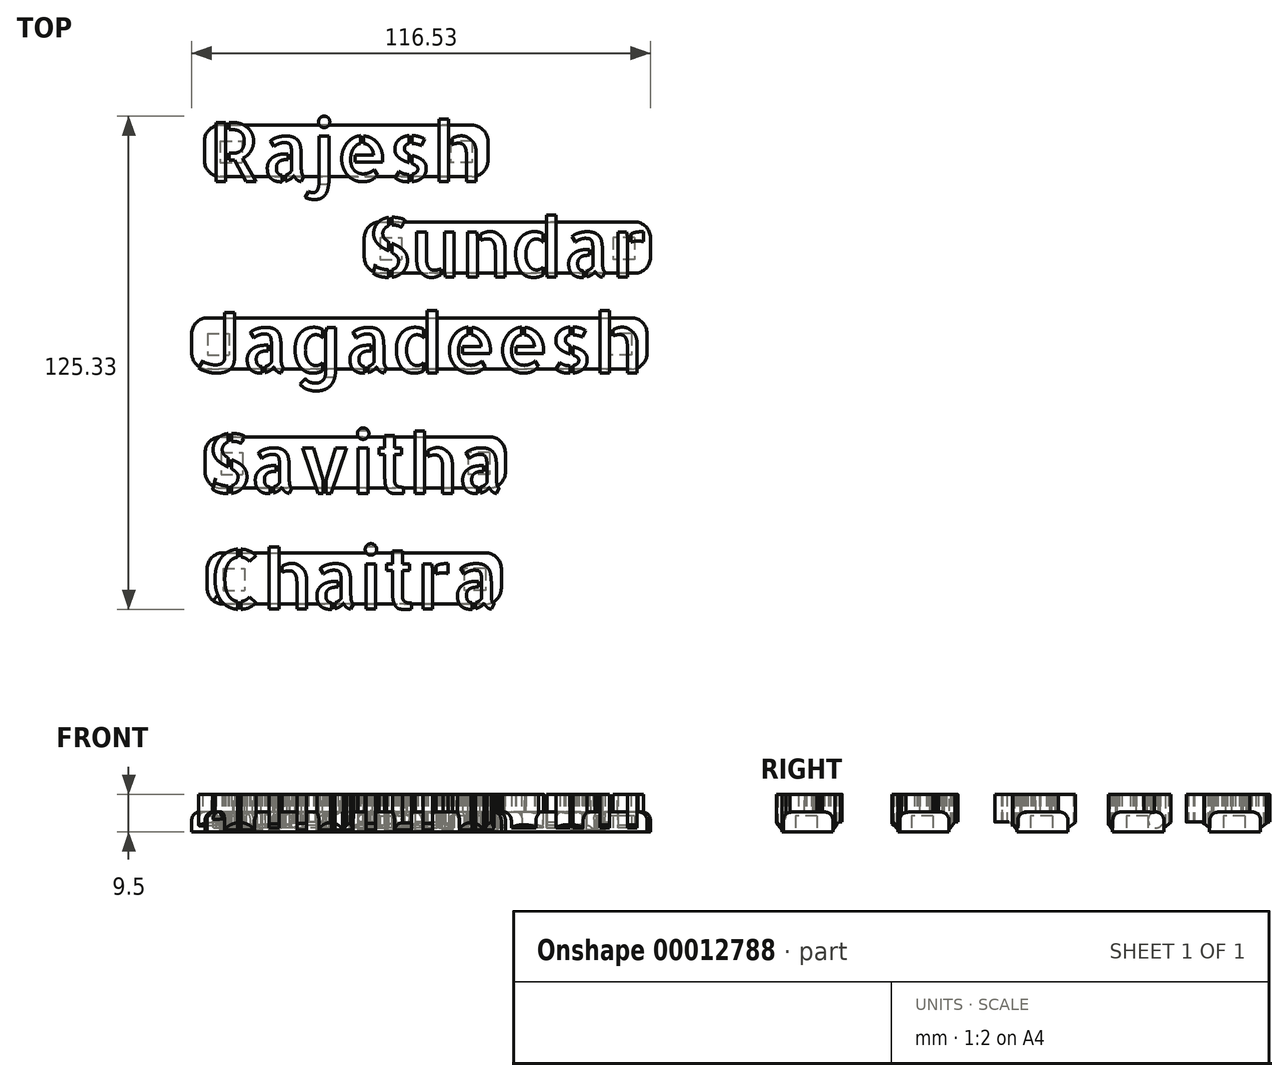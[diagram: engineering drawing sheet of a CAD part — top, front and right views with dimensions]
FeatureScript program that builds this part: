
annotation { "Feature Type Name" : "Feature", "Feature Type Description" : "" }
export const myFeature = defineFeature(function(context is Context, id is Id, definition is map)
    precondition{}
    {
        {
            var Q0;
            Q0=qCreatedBy(makeId("Top.planeOp"),FACE);
            var sketch = newSketch(context, id + "F0", { "sketchPlane" : qUnion([Q0])});
            skText(sketch, "E0", { "text": "Rajesh", "fontName": "AllertaStencil-Regular.ttf"});
            skText(sketch, "E1", { "text": "Sundar", "fontName": "AllertaStencil-Regular.ttf"});
            skText(sketch, "E2", { "text": "Jagadeesh", "fontName": "AllertaStencil-Regular.ttf"});
            skText(sketch, "E3", { "text": "Savitha", "fontName": "AllertaStencil-Regular.ttf"});
            skText(sketch, "E4", { "text": "Chaitra", "fontName": "AllertaStencil-Regular.ttf"});
            const initialGuessF0  = {"E0": [-0.06447, 0.04937, 1, 0, 0.015], "E1": [-0.02434, 0.02506, 1, 0, 0.015], "E2": [-0.06765, 0.00075, 1, 0, 0.015], "E3": [-0.06512, -0.02985, 1, 0, 0.015], "E4": [-0.0645, -0.05926, 1, 0, 0.015]};
            skSetInitialGuess(sketch, initialGuessF0);
            skSolve(sketch);
        }
        {
            var Q0;
            Q0 = qSketchRegion(id + "F0", true);
            extrude(context, id + "F1", {"entities" : qUnion([Q0]), "depth" : 7 * mm});
        }
        {
            var Q0;
            Q0=qCreatedBy(makeId("Top.planeOp"),FACE);
            var sketch = newSketch(context, id + "F2", { "sketchPlane" : qUnion([Q0])});
            skLineSegment(sketch, "E5.bottom", {"start": v(-65.56, 63.64) * mm, "end": v(6.44, 63.64) * mm});
            skLineSegment(sketch, "E5.top", {"start": v(-65.56, 50.64) * mm, "end": v(6.44, 50.64) * mm});
            skLineSegment(sketch, "E5.left", {"start": v(-65.56, 63.64) * mm, "end": v(-65.56, 50.64) * mm});
            skLineSegment(sketch, "E5.right", {"start": v(6.44, 63.64) * mm, "end": v(6.44, 50.64) * mm});
            skLineSegment(sketch, "E6.bottom", {"start": v(-24.95, 39.07) * mm, "end": v(47.73, 39.07) * mm});
            skLineSegment(sketch, "E6.top", {"start": v(-24.95, 26.07) * mm, "end": v(47.73, 26.07) * mm});
            skLineSegment(sketch, "E6.left", {"start": v(-24.95, 39.07) * mm, "end": v(-24.95, 26.07) * mm});
            skLineSegment(sketch, "E6.right", {"start": v(47.73, 39.07) * mm, "end": v(47.73, 26.07) * mm});
            skLineSegment(sketch, "E7.bottom", {"start": v(-68.8, 14.71) * mm, "end": v(46.87, 14.71) * mm});
            skLineSegment(sketch, "E7.top", {"start": v(-68.8, 1.71) * mm, "end": v(46.87, 1.71) * mm});
            skLineSegment(sketch, "E7.left", {"start": v(-68.8, 14.71) * mm, "end": v(-68.8, 1.71) * mm});
            skLineSegment(sketch, "E7.right", {"start": v(46.87, 14.71) * mm, "end": v(46.87, 1.71) * mm});
            skLineSegment(sketch, "E8.bottom", {"start": v(-65.39, -15.52) * mm, "end": v(10.87, -15.52) * mm});
            skLineSegment(sketch, "E8.top", {"start": v(-65.39, -28.52) * mm, "end": v(10.87, -28.52) * mm});
            skLineSegment(sketch, "E8.left", {"start": v(-65.39, -15.52) * mm, "end": v(-65.39, -28.52) * mm});
            skLineSegment(sketch, "E8.right", {"start": v(10.87, -15.52) * mm, "end": v(10.87, -28.52) * mm});
            skLineSegment(sketch, "E9.bottom", {"start": v(-64.88, -45) * mm, "end": v(9.85, -45) * mm});
            skLineSegment(sketch, "E9.top", {"start": v(-64.88, -58) * mm, "end": v(9.85, -58) * mm});
            skLineSegment(sketch, "E9.left", {"start": v(-64.88, -45) * mm, "end": v(-64.88, -58) * mm});
            skLineSegment(sketch, "E9.right", {"start": v(9.85, -45) * mm, "end": v(9.85, -58) * mm});
            skSolve(sketch);
        }
        {
            var Q0;
            Q0=qCreatedBy(makeId("Top.planeOp"),FACE);
            cPlane(context, id + "F3", {"entities" : qUnion([Q0]), "cplaneType" : CPlaneType.OFFSET, "offset" : 2.5 * mm, "width" : 150 * mm, "height" : 150 * mm});
        }
        {
            var Q0;
            Q0=qCreatedBy(id+"F3.planeOp",FACE);
            var sketch = newSketch(context, id + "F4", { "sketchPlane" : qUnion([Q0])});
            skLineSegment(sketch, "E10.0.0", {"start": v(6.44, 63.64) * mm, "end": v(-65.56, 63.64) * mm});
            skLineSegment(sketch, "E10.0.1", {"start": v(-65.56, 63.64) * mm, "end": v(-65.56, 50.64) * mm});
            skLineSegment(sketch, "E10.0.2", {"start": v(-65.56, 50.64) * mm, "end": v(6.44, 50.64) * mm});
            skLineSegment(sketch, "E10.0.3", {"start": v(6.44, 50.64) * mm, "end": v(6.44, 63.64) * mm});
            skLineSegment(sketch, "E11.0.0", {"start": v(47.73, 39.07) * mm, "end": v(-24.95, 39.07) * mm});
            skLineSegment(sketch, "E11.0.1", {"start": v(-24.95, 39.07) * mm, "end": v(-24.95, 26.07) * mm});
            skLineSegment(sketch, "E11.0.2", {"start": v(-24.95, 26.07) * mm, "end": v(47.73, 26.07) * mm});
            skLineSegment(sketch, "E11.0.3", {"start": v(47.73, 26.07) * mm, "end": v(47.73, 39.07) * mm});
            skLineSegment(sketch, "E12.0.0", {"start": v(46.87, 14.71) * mm, "end": v(-68.8, 14.71) * mm});
            skLineSegment(sketch, "E12.0.1", {"start": v(-68.8, 14.71) * mm, "end": v(-68.8, 1.71) * mm});
            skLineSegment(sketch, "E12.0.2", {"start": v(-68.8, 1.71) * mm, "end": v(46.87, 1.71) * mm});
            skLineSegment(sketch, "E12.0.3", {"start": v(46.87, 1.71) * mm, "end": v(46.87, 14.71) * mm});
            skLineSegment(sketch, "E13.0.0", {"start": v(10.87, -15.52) * mm, "end": v(-65.39, -15.52) * mm});
            skLineSegment(sketch, "E13.0.1", {"start": v(-65.39, -15.52) * mm, "end": v(-65.39, -28.52) * mm});
            skLineSegment(sketch, "E13.0.2", {"start": v(-65.39, -28.52) * mm, "end": v(10.87, -28.52) * mm});
            skLineSegment(sketch, "E13.0.3", {"start": v(10.87, -28.52) * mm, "end": v(10.87, -15.52) * mm});
            skLineSegment(sketch, "E14.0.0", {"start": v(9.85, -45) * mm, "end": v(-64.88, -45) * mm});
            skLineSegment(sketch, "E14.0.1", {"start": v(-64.88, -45) * mm, "end": v(-64.88, -58) * mm});
            skLineSegment(sketch, "E14.0.2", {"start": v(-64.88, -58) * mm, "end": v(9.85, -58) * mm});
            skLineSegment(sketch, "E14.0.3", {"start": v(9.85, -58) * mm, "end": v(9.85, -45) * mm});
            skSolve(sketch);
        }
        {
            var Q0;
            Q0 = qSketchRegion(id + "F4", true);
            extrude(context, id + "F5", {"entities" : qUnion([Q0]), "oppositeDirection" : true, "depth" : 5 * mm});
        }
        {
            var Q0;
            Q0=makeQuery(id+"F5.opExtrude","SWEPT_EDGE",EDGE,{"disambiguationData":[OSD([sQuery(id+"F4.wireOp",EDGE,"E10.0.0"),sQuery(id+"F4.wireOp",EDGE,"E10.0.3")])]});
            var Q1;
            Q1=makeQuery(id+"F5.opExtrude","SWEPT_EDGE",EDGE,{"disambiguationData":[OSD([sQuery(id+"F4.wireOp",EDGE,"E10.0.2"),sQuery(id+"F4.wireOp",EDGE,"E10.0.3")])]});
            var Q2;
            Q2=makeQuery(id+"F5.opExtrude","SWEPT_EDGE",EDGE,{"disambiguationData":[OSD([sQuery(id+"F4.wireOp",EDGE,"E11.0.0"),sQuery(id+"F4.wireOp",EDGE,"E11.0.3")])]});
            var Q3;
            Q3=makeQuery(id+"F5.opExtrude","SWEPT_EDGE",EDGE,{"disambiguationData":[OSD([sQuery(id+"F4.wireOp",EDGE,"E12.0.0"),sQuery(id+"F4.wireOp",EDGE,"E12.0.3")])]});
            var Q4;
            Q4=makeQuery(id+"F5.opExtrude","SWEPT_EDGE",EDGE,{"disambiguationData":[OSD([sQuery(id+"F4.wireOp",EDGE,"E12.0.2"),sQuery(id+"F4.wireOp",EDGE,"E12.0.3")])]});
            var Q5;
            Q5=makeQuery(id+"F5.opExtrude","SWEPT_EDGE",EDGE,{"disambiguationData":[OSD([sQuery(id+"F4.wireOp",EDGE,"E13.0.0"),sQuery(id+"F4.wireOp",EDGE,"E13.0.3")])]});
            var Q6;
            Q6=makeQuery(id+"F5.opExtrude","SWEPT_EDGE",EDGE,{"disambiguationData":[OSD([sQuery(id+"F4.wireOp",EDGE,"E13.0.2"),sQuery(id+"F4.wireOp",EDGE,"E13.0.3")])]});
            var Q7;
            Q7=makeQuery(id+"F5.opExtrude","SWEPT_EDGE",EDGE,{"disambiguationData":[OSD([sQuery(id+"F4.wireOp",EDGE,"E14.0.0"),sQuery(id+"F4.wireOp",EDGE,"E14.0.3")])]});
            var Q8;
            Q8=makeQuery(id+"F5.opExtrude","SWEPT_EDGE",EDGE,{"disambiguationData":[OSD([sQuery(id+"F4.wireOp",EDGE,"E14.0.2"),sQuery(id+"F4.wireOp",EDGE,"E14.0.3")])]});
            var Q9;
            Q9=makeQuery(id+"F5.opExtrude","SWEPT_EDGE",EDGE,{"disambiguationData":[OSD([sQuery(id+"F4.wireOp",EDGE,"E14.0.1"),sQuery(id+"F4.wireOp",EDGE,"E14.0.2")])]});
            var Q10;
            Q10=makeQuery(id+"F5.opExtrude","SWEPT_EDGE",EDGE,{"disambiguationData":[OSD([sQuery(id+"F4.wireOp",EDGE,"E13.0.1"),sQuery(id+"F4.wireOp",EDGE,"E13.0.2")])]});
            var Q11;
            Q11=makeQuery(id+"F5.opExtrude","SWEPT_EDGE",EDGE,{"disambiguationData":[OSD([sQuery(id+"F4.wireOp",EDGE,"E13.0.0"),sQuery(id+"F4.wireOp",EDGE,"E13.0.1")])]});
            var Q12;
            Q12=makeQuery(id+"F5.opExtrude","SWEPT_EDGE",EDGE,{"disambiguationData":[OSD([sQuery(id+"F4.wireOp",EDGE,"E14.0.0"),sQuery(id+"F4.wireOp",EDGE,"E14.0.1")])]});
            var Q13;
            Q13=makeQuery(id+"F5.opExtrude","SWEPT_EDGE",EDGE,{"disambiguationData":[OSD([sQuery(id+"F4.wireOp",EDGE,"E12.0.1"),sQuery(id+"F4.wireOp",EDGE,"E12.0.2")])]});
            var Q14;
            Q14=makeQuery(id+"F5.opExtrude","SWEPT_EDGE",EDGE,{"disambiguationData":[OSD([sQuery(id+"F4.wireOp",EDGE,"E12.0.0"),sQuery(id+"F4.wireOp",EDGE,"E12.0.1")])]});
            var Q15;
            Q15=makeQuery(id+"F5.opExtrude","SWEPT_EDGE",EDGE,{"disambiguationData":[OSD([sQuery(id+"F4.wireOp",EDGE,"E10.0.1"),sQuery(id+"F4.wireOp",EDGE,"E10.0.2")])]});
            var Q16;
            Q16=makeQuery(id+"F5.opExtrude","SWEPT_EDGE",EDGE,{"disambiguationData":[OSD([sQuery(id+"F4.wireOp",EDGE,"E10.0.0"),sQuery(id+"F4.wireOp",EDGE,"E10.0.1")])]});
            var Q17;
            Q17=makeQuery(id+"F5.opExtrude","SWEPT_EDGE",EDGE,{"disambiguationData":[OSD([sQuery(id+"F4.wireOp",EDGE,"E11.0.1"),sQuery(id+"F4.wireOp",EDGE,"E11.0.2")])]});
            var Q18;
            Q18=makeQuery(id+"F5.opExtrude","SWEPT_EDGE",EDGE,{"disambiguationData":[OSD([sQuery(id+"F4.wireOp",EDGE,"E11.0.0"),sQuery(id+"F4.wireOp",EDGE,"E11.0.1")])]});
            var Q19;
            Q19=makeQuery(id+"F5.opExtrude","SWEPT_EDGE",EDGE,{"disambiguationData":[OSD([sQuery(id+"F4.wireOp",EDGE,"E11.0.2"),sQuery(id+"F4.wireOp",EDGE,"E11.0.3")])]});
            fillet(context, id + "F6", {"entities" : qUnion([Q0, Q1, Q2, Q3, Q4, Q5, Q6, Q7, Q8, Q9, Q10, Q11, Q12, Q13, Q14, Q15, Q16, Q17, Q18, Q19]), "radius" : 4 * mm, "tangentPropagation" : true, "allowEdgeOverflow" : false});
        }
        {
            var Q0;
            Q0=makeQuery(id+"F5.opExtrude","SWEPT_BODY",BODY,{"disambiguationData":[OSD([sQuery(id+"F4.wireOp",EDGE,"E10.0.0"),sQuery(id+"F4.wireOp",EDGE,"E10.0.1"),sQuery(id+"F4.wireOp",EDGE,"E10.0.2"),sQuery(id+"F4.wireOp",EDGE,"E10.0.3")])]});
            var Q1;
            Q1=makeQuery(id+"F1.opExtrude","SWEPT_BODY",BODY,{"disambiguationData":[OSD([sQuery(id+"F0.wireOp",EDGE,"E0.sketch_text.stroke-0"),sQuery(id+"F0.wireOp",EDGE,"E0.sketch_text.stroke-1"),sQuery(id+"F0.wireOp",EDGE,"E0.sketch_text.stroke-2"),sQuery(id+"F0.wireOp",EDGE,"E0.sketch_text.stroke-3")])]});
            var Q2;
            Q2=makeQuery(id+"F1.opExtrude","SWEPT_BODY",BODY,{"disambiguationData":[OSD([sQuery(id+"F0.wireOp",EDGE,"E0.sketch_text.stroke-4"),sQuery(id+"F0.wireOp",EDGE,"E0.sketch_text.stroke-5"),sQuery(id+"F0.wireOp",EDGE,"E0.sketch_text.stroke-6"),sQuery(id+"F0.wireOp",EDGE,"E0.sketch_text.stroke-7"),sQuery(id+"F0.wireOp",EDGE,"E0.sketch_text.stroke-8"),sQuery(id+"F0.wireOp",EDGE,"E0.sketch_text.stroke-9"),sQuery(id+"F0.wireOp",EDGE,"E0.sketch_text.stroke-10"),sQuery(id+"F0.wireOp",EDGE,"E0.sketch_text.stroke-11"),sQuery(id+"F0.wireOp",EDGE,"E0.sketch_text.stroke-12"),sQuery(id+"F0.wireOp",EDGE,"E0.sketch_text.stroke-13"),sQuery(id+"F0.wireOp",EDGE,"E0.sketch_text.stroke-14"),sQuery(id+"F0.wireOp",EDGE,"E0.sketch_text.stroke-15"),sQuery(id+"F0.wireOp",EDGE,"E0.sketch_text.stroke-16"),sQuery(id+"F0.wireOp",EDGE,"E0.sketch_text.stroke-17"),sQuery(id+"F0.wireOp",EDGE,"E0.sketch_text.stroke-18"),sQuery(id+"F0.wireOp",EDGE,"E0.sketch_text.stroke-19"),sQuery(id+"F0.wireOp",EDGE,"E0.sketch_text.stroke-20"),sQuery(id+"F0.wireOp",EDGE,"E0.sketch_text.stroke-21"),sQuery(id+"F0.wireOp",EDGE,"E0.sketch_text.stroke-22"),sQuery(id+"F0.wireOp",EDGE,"E0.sketch_text.stroke-23"),sQuery(id+"F0.wireOp",EDGE,"E0.sketch_text.stroke-24"),sQuery(id+"F0.wireOp",EDGE,"E0.sketch_text.stroke-25"),sQuery(id+"F0.wireOp",EDGE,"E0.sketch_text.stroke-26"),sQuery(id+"F0.wireOp",EDGE,"E0.sketch_text.stroke-27"),sQuery(id+"F0.wireOp",EDGE,"E0.sketch_text.stroke-28"),sQuery(id+"F0.wireOp",EDGE,"E0.sketch_text.stroke-29")])]});
            var Q3;
            Q3=makeQuery(id+"F1.opExtrude","SWEPT_BODY",BODY,{"disambiguationData":[OSD([sQuery(id+"F0.wireOp",EDGE,"E0.sketch_text.stroke-124"),sQuery(id+"F0.wireOp",EDGE,"E0.sketch_text.stroke-125"),sQuery(id+"F0.wireOp",EDGE,"E0.sketch_text.stroke-126"),sQuery(id+"F0.wireOp",EDGE,"E0.sketch_text.stroke-127"),sQuery(id+"F0.wireOp",EDGE,"E0.sketch_text.stroke-128"),sQuery(id+"F0.wireOp",EDGE,"E0.sketch_text.stroke-129"),sQuery(id+"F0.wireOp",EDGE,"E0.sketch_text.stroke-130"),sQuery(id+"F0.wireOp",EDGE,"E0.sketch_text.stroke-131"),sQuery(id+"F0.wireOp",EDGE,"E0.sketch_text.stroke-132"),sQuery(id+"F0.wireOp",EDGE,"E0.sketch_text.stroke-133"),sQuery(id+"F0.wireOp",EDGE,"E0.sketch_text.stroke-134"),sQuery(id+"F0.wireOp",EDGE,"E0.sketch_text.stroke-135"),sQuery(id+"F0.wireOp",EDGE,"E0.sketch_text.stroke-136"),sQuery(id+"F0.wireOp",EDGE,"E0.sketch_text.stroke-137"),sQuery(id+"F0.wireOp",EDGE,"E0.sketch_text.stroke-138"),sQuery(id+"F0.wireOp",EDGE,"E0.sketch_text.stroke-139"),sQuery(id+"F0.wireOp",EDGE,"E0.sketch_text.stroke-140"),sQuery(id+"F0.wireOp",EDGE,"E0.sketch_text.stroke-141"),sQuery(id+"F0.wireOp",EDGE,"E0.sketch_text.stroke-142"),sQuery(id+"F0.wireOp",EDGE,"E0.sketch_text.stroke-143"),sQuery(id+"F0.wireOp",EDGE,"E0.sketch_text.stroke-144"),sQuery(id+"F0.wireOp",EDGE,"E0.sketch_text.stroke-145"),sQuery(id+"F0.wireOp",EDGE,"E0.sketch_text.stroke-146"),sQuery(id+"F0.wireOp",EDGE,"E0.sketch_text.stroke-147")])]});
            var Q4;
            Q4=makeQuery(id+"F1.opExtrude","SWEPT_BODY",BODY,{"disambiguationData":[OSD([sQuery(id+"F0.wireOp",EDGE,"E0.sketch_text.stroke-148"),sQuery(id+"F0.wireOp",EDGE,"E0.sketch_text.stroke-149"),sQuery(id+"F0.wireOp",EDGE,"E0.sketch_text.stroke-150"),sQuery(id+"F0.wireOp",EDGE,"E0.sketch_text.stroke-151"),sQuery(id+"F0.wireOp",EDGE,"E0.sketch_text.stroke-152"),sQuery(id+"F0.wireOp",EDGE,"E0.sketch_text.stroke-153"),sQuery(id+"F0.wireOp",EDGE,"E0.sketch_text.stroke-154"),sQuery(id+"F0.wireOp",EDGE,"E0.sketch_text.stroke-155"),sQuery(id+"F0.wireOp",EDGE,"E0.sketch_text.stroke-156"),sQuery(id+"F0.wireOp",EDGE,"E0.sketch_text.stroke-157"),sQuery(id+"F0.wireOp",EDGE,"E0.sketch_text.stroke-158"),sQuery(id+"F0.wireOp",EDGE,"E0.sketch_text.stroke-159"),sQuery(id+"F0.wireOp",EDGE,"E0.sketch_text.stroke-160"),sQuery(id+"F0.wireOp",EDGE,"E0.sketch_text.stroke-161")])]});
            var Q5;
            Q5=makeQuery(id+"F1.opExtrude","SWEPT_BODY",BODY,{"disambiguationData":[OSD([sQuery(id+"F0.wireOp",EDGE,"E0.sketch_text.stroke-111"),sQuery(id+"F0.wireOp",EDGE,"E0.sketch_text.stroke-112"),sQuery(id+"F0.wireOp",EDGE,"E0.sketch_text.stroke-113"),sQuery(id+"F0.wireOp",EDGE,"E0.sketch_text.stroke-114"),sQuery(id+"F0.wireOp",EDGE,"E0.sketch_text.stroke-115"),sQuery(id+"F0.wireOp",EDGE,"E0.sketch_text.stroke-116"),sQuery(id+"F0.wireOp",EDGE,"E0.sketch_text.stroke-117"),sQuery(id+"F0.wireOp",EDGE,"E0.sketch_text.stroke-118"),sQuery(id+"F0.wireOp",EDGE,"E0.sketch_text.stroke-119"),sQuery(id+"F0.wireOp",EDGE,"E0.sketch_text.stroke-120"),sQuery(id+"F0.wireOp",EDGE,"E0.sketch_text.stroke-121"),sQuery(id+"F0.wireOp",EDGE,"E0.sketch_text.stroke-122"),sQuery(id+"F0.wireOp",EDGE,"E0.sketch_text.stroke-123")])]});
            var Q6;
            Q6=makeQuery(id+"F1.opExtrude","SWEPT_BODY",BODY,{"disambiguationData":[OSD([sQuery(id+"F0.wireOp",EDGE,"E0.sketch_text.stroke-191"),sQuery(id+"F0.wireOp",EDGE,"E0.sketch_text.stroke-192"),sQuery(id+"F0.wireOp",EDGE,"E0.sketch_text.stroke-193"),sQuery(id+"F0.wireOp",EDGE,"E0.sketch_text.stroke-194")])]});
            var Q7;
            Q7=makeQuery(id+"F1.opExtrude","SWEPT_BODY",BODY,{"disambiguationData":[OSD([sQuery(id+"F0.wireOp",EDGE,"E0.sketch_text.stroke-30"),sQuery(id+"F0.wireOp",EDGE,"E0.sketch_text.stroke-31"),sQuery(id+"F0.wireOp",EDGE,"E0.sketch_text.stroke-32"),sQuery(id+"F0.wireOp",EDGE,"E0.sketch_text.stroke-33"),sQuery(id+"F0.wireOp",EDGE,"E0.sketch_text.stroke-34"),sQuery(id+"F0.wireOp",EDGE,"E0.sketch_text.stroke-35"),sQuery(id+"F0.wireOp",EDGE,"E0.sketch_text.stroke-36"),sQuery(id+"F0.wireOp",EDGE,"E0.sketch_text.stroke-37"),sQuery(id+"F0.wireOp",EDGE,"E0.sketch_text.stroke-38"),sQuery(id+"F0.wireOp",EDGE,"E0.sketch_text.stroke-39"),sQuery(id+"F0.wireOp",EDGE,"E0.sketch_text.stroke-40"),sQuery(id+"F0.wireOp",EDGE,"E0.sketch_text.stroke-41"),sQuery(id+"F0.wireOp",EDGE,"E0.sketch_text.stroke-42"),sQuery(id+"F0.wireOp",EDGE,"E0.sketch_text.stroke-43"),sQuery(id+"F0.wireOp",EDGE,"E0.sketch_text.stroke-44"),sQuery(id+"F0.wireOp",EDGE,"E0.sketch_text.stroke-45"),sQuery(id+"F0.wireOp",EDGE,"E0.sketch_text.stroke-46"),sQuery(id+"F0.wireOp",EDGE,"E0.sketch_text.stroke-47"),sQuery(id+"F0.wireOp",EDGE,"E0.sketch_text.stroke-48")])]});
            var Q8;
            Q8=makeQuery(id+"F1.opExtrude","SWEPT_BODY",BODY,{"disambiguationData":[OSD([sQuery(id+"F0.wireOp",EDGE,"E0.sketch_text.stroke-49"),sQuery(id+"F0.wireOp",EDGE,"E0.sketch_text.stroke-50"),sQuery(id+"F0.wireOp",EDGE,"E0.sketch_text.stroke-51"),sQuery(id+"F0.wireOp",EDGE,"E0.sketch_text.stroke-52"),sQuery(id+"F0.wireOp",EDGE,"E0.sketch_text.stroke-53"),sQuery(id+"F0.wireOp",EDGE,"E0.sketch_text.stroke-54"),sQuery(id+"F0.wireOp",EDGE,"E0.sketch_text.stroke-55"),sQuery(id+"F0.wireOp",EDGE,"E0.sketch_text.stroke-56"),sQuery(id+"F0.wireOp",EDGE,"E0.sketch_text.stroke-57"),sQuery(id+"F0.wireOp",EDGE,"E0.sketch_text.stroke-58"),sQuery(id+"F0.wireOp",EDGE,"E0.sketch_text.stroke-59"),sQuery(id+"F0.wireOp",EDGE,"E0.sketch_text.stroke-60"),sQuery(id+"F0.wireOp",EDGE,"E0.sketch_text.stroke-61"),sQuery(id+"F0.wireOp",EDGE,"E0.sketch_text.stroke-62"),sQuery(id+"F0.wireOp",EDGE,"E0.sketch_text.stroke-63"),sQuery(id+"F0.wireOp",EDGE,"E0.sketch_text.stroke-64"),sQuery(id+"F0.wireOp",EDGE,"E0.sketch_text.stroke-65"),sQuery(id+"F0.wireOp",EDGE,"E0.sketch_text.stroke-66"),sQuery(id+"F0.wireOp",EDGE,"E0.sketch_text.stroke-67"),sQuery(id+"F0.wireOp",EDGE,"E0.sketch_text.stroke-68"),sQuery(id+"F0.wireOp",EDGE,"E0.sketch_text.stroke-69"),sQuery(id+"F0.wireOp",EDGE,"E0.sketch_text.stroke-70"),sQuery(id+"F0.wireOp",EDGE,"E0.sketch_text.stroke-71"),sQuery(id+"F0.wireOp",EDGE,"E0.sketch_text.stroke-72"),sQuery(id+"F0.wireOp",EDGE,"E0.sketch_text.stroke-73"),sQuery(id+"F0.wireOp",EDGE,"E0.sketch_text.stroke-74"),sQuery(id+"F0.wireOp",EDGE,"E0.sketch_text.stroke-75"),sQuery(id+"F0.wireOp",EDGE,"E0.sketch_text.stroke-76"),sQuery(id+"F0.wireOp",EDGE,"E0.sketch_text.stroke-77"),sQuery(id+"F0.wireOp",EDGE,"E0.sketch_text.stroke-78"),sQuery(id+"F0.wireOp",EDGE,"E0.sketch_text.stroke-79"),sQuery(id+"F0.wireOp",EDGE,"E0.sketch_text.stroke-80"),sQuery(id+"F0.wireOp",EDGE,"E0.sketch_text.stroke-81"),sQuery(id+"F0.wireOp",EDGE,"E0.sketch_text.stroke-82"),sQuery(id+"F0.wireOp",EDGE,"E0.sketch_text.stroke-83"),sQuery(id+"F0.wireOp",EDGE,"E0.sketch_text.stroke-84")])]});
            var Q9;
            Q9=makeQuery(id+"F1.opExtrude","SWEPT_BODY",BODY,{"disambiguationData":[OSD([sQuery(id+"F0.wireOp",EDGE,"E0.sketch_text.stroke-162"),sQuery(id+"F0.wireOp",EDGE,"E0.sketch_text.stroke-163"),sQuery(id+"F0.wireOp",EDGE,"E0.sketch_text.stroke-164"),sQuery(id+"F0.wireOp",EDGE,"E0.sketch_text.stroke-165"),sQuery(id+"F0.wireOp",EDGE,"E0.sketch_text.stroke-166"),sQuery(id+"F0.wireOp",EDGE,"E0.sketch_text.stroke-167")])]});
            var Q10;
            Q10=makeQuery(id+"F1.opExtrude","SWEPT_BODY",BODY,{"disambiguationData":[OSD([sQuery(id+"F0.wireOp",EDGE,"E0.sketch_text.stroke-177"),sQuery(id+"F0.wireOp",EDGE,"E0.sketch_text.stroke-178"),sQuery(id+"F0.wireOp",EDGE,"E0.sketch_text.stroke-179"),sQuery(id+"F0.wireOp",EDGE,"E0.sketch_text.stroke-180"),sQuery(id+"F0.wireOp",EDGE,"E0.sketch_text.stroke-181"),sQuery(id+"F0.wireOp",EDGE,"E0.sketch_text.stroke-182"),sQuery(id+"F0.wireOp",EDGE,"E0.sketch_text.stroke-183"),sQuery(id+"F0.wireOp",EDGE,"E0.sketch_text.stroke-184"),sQuery(id+"F0.wireOp",EDGE,"E0.sketch_text.stroke-185"),sQuery(id+"F0.wireOp",EDGE,"E0.sketch_text.stroke-186"),sQuery(id+"F0.wireOp",EDGE,"E0.sketch_text.stroke-187"),sQuery(id+"F0.wireOp",EDGE,"E0.sketch_text.stroke-188"),sQuery(id+"F0.wireOp",EDGE,"E0.sketch_text.stroke-189"),sQuery(id+"F0.wireOp",EDGE,"E0.sketch_text.stroke-190")])]});
            var Q11;
            Q11=makeQuery(id+"F1.opExtrude","SWEPT_BODY",BODY,{"disambiguationData":[OSD([sQuery(id+"F0.wireOp",EDGE,"E0.sketch_text.stroke-85"),sQuery(id+"F0.wireOp",EDGE,"E0.sketch_text.stroke-86"),sQuery(id+"F0.wireOp",EDGE,"E0.sketch_text.stroke-87"),sQuery(id+"F0.wireOp",EDGE,"E0.sketch_text.stroke-88"),sQuery(id+"F0.wireOp",EDGE,"E0.sketch_text.stroke-89"),sQuery(id+"F0.wireOp",EDGE,"E0.sketch_text.stroke-90"),sQuery(id+"F0.wireOp",EDGE,"E0.sketch_text.stroke-91"),sQuery(id+"F0.wireOp",EDGE,"E0.sketch_text.stroke-92"),sQuery(id+"F0.wireOp",EDGE,"E0.sketch_text.stroke-93"),sQuery(id+"F0.wireOp",EDGE,"E0.sketch_text.stroke-94"),sQuery(id+"F0.wireOp",EDGE,"E0.sketch_text.stroke-95"),sQuery(id+"F0.wireOp",EDGE,"E0.sketch_text.stroke-96"),sQuery(id+"F0.wireOp",EDGE,"E0.sketch_text.stroke-97"),sQuery(id+"F0.wireOp",EDGE,"E0.sketch_text.stroke-98"),sQuery(id+"F0.wireOp",EDGE,"E0.sketch_text.stroke-99"),sQuery(id+"F0.wireOp",EDGE,"E0.sketch_text.stroke-100"),sQuery(id+"F0.wireOp",EDGE,"E0.sketch_text.stroke-101"),sQuery(id+"F0.wireOp",EDGE,"E0.sketch_text.stroke-102")])]});
            var Q12;
            Q12=makeQuery(id+"F1.opExtrude","SWEPT_BODY",BODY,{"disambiguationData":[OSD([sQuery(id+"F0.wireOp",EDGE,"E0.sketch_text.stroke-195"),sQuery(id+"F0.wireOp",EDGE,"E0.sketch_text.stroke-196"),sQuery(id+"F0.wireOp",EDGE,"E0.sketch_text.stroke-197"),sQuery(id+"F0.wireOp",EDGE,"E0.sketch_text.stroke-198"),sQuery(id+"F0.wireOp",EDGE,"E0.sketch_text.stroke-199"),sQuery(id+"F0.wireOp",EDGE,"E0.sketch_text.stroke-200"),sQuery(id+"F0.wireOp",EDGE,"E0.sketch_text.stroke-201"),sQuery(id+"F0.wireOp",EDGE,"E0.sketch_text.stroke-202"),sQuery(id+"F0.wireOp",EDGE,"E0.sketch_text.stroke-203"),sQuery(id+"F0.wireOp",EDGE,"E0.sketch_text.stroke-204"),sQuery(id+"F0.wireOp",EDGE,"E0.sketch_text.stroke-205"),sQuery(id+"F0.wireOp",EDGE,"E0.sketch_text.stroke-206"),sQuery(id+"F0.wireOp",EDGE,"E0.sketch_text.stroke-207"),sQuery(id+"F0.wireOp",EDGE,"E0.sketch_text.stroke-208"),sQuery(id+"F0.wireOp",EDGE,"E0.sketch_text.stroke-209"),sQuery(id+"F0.wireOp",EDGE,"E0.sketch_text.stroke-210"),sQuery(id+"F0.wireOp",EDGE,"E0.sketch_text.stroke-211"),sQuery(id+"F0.wireOp",EDGE,"E0.sketch_text.stroke-212"),sQuery(id+"F0.wireOp",EDGE,"E0.sketch_text.stroke-213")])]});
            var Q13;
            Q13=makeQuery(id+"F1.opExtrude","SWEPT_BODY",BODY,{"disambiguationData":[OSD([sQuery(id+"F0.wireOp",EDGE,"E0.sketch_text.stroke-168"),sQuery(id+"F0.wireOp",EDGE,"E0.sketch_text.stroke-169"),sQuery(id+"F0.wireOp",EDGE,"E0.sketch_text.stroke-170"),sQuery(id+"F0.wireOp",EDGE,"E0.sketch_text.stroke-171"),sQuery(id+"F0.wireOp",EDGE,"E0.sketch_text.stroke-172"),sQuery(id+"F0.wireOp",EDGE,"E0.sketch_text.stroke-173"),sQuery(id+"F0.wireOp",EDGE,"E0.sketch_text.stroke-174"),sQuery(id+"F0.wireOp",EDGE,"E0.sketch_text.stroke-175"),sQuery(id+"F0.wireOp",EDGE,"E0.sketch_text.stroke-176")])]});
            var Q14;
            Q14=makeQuery(id+"F1.opExtrude","SWEPT_BODY",BODY,{"disambiguationData":[OSD([sQuery(id+"F0.wireOp",EDGE,"E0.sketch_text.stroke-103"),sQuery(id+"F0.wireOp",EDGE,"E0.sketch_text.stroke-104"),sQuery(id+"F0.wireOp",EDGE,"E0.sketch_text.stroke-105"),sQuery(id+"F0.wireOp",EDGE,"E0.sketch_text.stroke-106"),sQuery(id+"F0.wireOp",EDGE,"E0.sketch_text.stroke-107"),sQuery(id+"F0.wireOp",EDGE,"E0.sketch_text.stroke-108"),sQuery(id+"F0.wireOp",EDGE,"E0.sketch_text.stroke-109"),sQuery(id+"F0.wireOp",EDGE,"E0.sketch_text.stroke-110")])]});
            booleanBodies(context, id + "F7", {"operationType" : BooleanOperationType.UNION, "tools" : qUnion([Q0, Q1, Q2, Q3, Q4, Q5, Q6, Q7, Q8, Q9, Q10, Q11, Q12, Q13, Q14])});
        }
        {
            var Q0;
            Q0=makeQuery(id+"F1.opExtrude","SWEPT_BODY",BODY,{"disambiguationData":[OSD([sQuery(id+"F0.wireOp",EDGE,"E1.sketch_text.stroke-129"),sQuery(id+"F0.wireOp",EDGE,"E1.sketch_text.stroke-130"),sQuery(id+"F0.wireOp",EDGE,"E1.sketch_text.stroke-131"),sQuery(id+"F0.wireOp",EDGE,"E1.sketch_text.stroke-132"),sQuery(id+"F0.wireOp",EDGE,"E1.sketch_text.stroke-133"),sQuery(id+"F0.wireOp",EDGE,"E1.sketch_text.stroke-134"),sQuery(id+"F0.wireOp",EDGE,"E1.sketch_text.stroke-135"),sQuery(id+"F0.wireOp",EDGE,"E1.sketch_text.stroke-136"),sQuery(id+"F0.wireOp",EDGE,"E1.sketch_text.stroke-137"),sQuery(id+"F0.wireOp",EDGE,"E1.sketch_text.stroke-138"),sQuery(id+"F0.wireOp",EDGE,"E1.sketch_text.stroke-139"),sQuery(id+"F0.wireOp",EDGE,"E1.sketch_text.stroke-140"),sQuery(id+"F0.wireOp",EDGE,"E1.sketch_text.stroke-141"),sQuery(id+"F0.wireOp",EDGE,"E1.sketch_text.stroke-142"),sQuery(id+"F0.wireOp",EDGE,"E1.sketch_text.stroke-143"),sQuery(id+"F0.wireOp",EDGE,"E1.sketch_text.stroke-144"),sQuery(id+"F0.wireOp",EDGE,"E1.sketch_text.stroke-145"),sQuery(id+"F0.wireOp",EDGE,"E1.sketch_text.stroke-146"),sQuery(id+"F0.wireOp",EDGE,"E1.sketch_text.stroke-147")])]});
            var Q1;
            Q1=makeQuery(id+"F1.opExtrude","SWEPT_BODY",BODY,{"disambiguationData":[OSD([sQuery(id+"F0.wireOp",EDGE,"E1.sketch_text.stroke-148"),sQuery(id+"F0.wireOp",EDGE,"E1.sketch_text.stroke-149"),sQuery(id+"F0.wireOp",EDGE,"E1.sketch_text.stroke-150"),sQuery(id+"F0.wireOp",EDGE,"E1.sketch_text.stroke-151"),sQuery(id+"F0.wireOp",EDGE,"E1.sketch_text.stroke-152"),sQuery(id+"F0.wireOp",EDGE,"E1.sketch_text.stroke-153"),sQuery(id+"F0.wireOp",EDGE,"E1.sketch_text.stroke-154"),sQuery(id+"F0.wireOp",EDGE,"E1.sketch_text.stroke-155"),sQuery(id+"F0.wireOp",EDGE,"E1.sketch_text.stroke-156"),sQuery(id+"F0.wireOp",EDGE,"E1.sketch_text.stroke-157"),sQuery(id+"F0.wireOp",EDGE,"E1.sketch_text.stroke-158"),sQuery(id+"F0.wireOp",EDGE,"E1.sketch_text.stroke-159"),sQuery(id+"F0.wireOp",EDGE,"E1.sketch_text.stroke-160"),sQuery(id+"F0.wireOp",EDGE,"E1.sketch_text.stroke-161"),sQuery(id+"F0.wireOp",EDGE,"E1.sketch_text.stroke-162"),sQuery(id+"F0.wireOp",EDGE,"E1.sketch_text.stroke-163"),sQuery(id+"F0.wireOp",EDGE,"E1.sketch_text.stroke-164"),sQuery(id+"F0.wireOp",EDGE,"E1.sketch_text.stroke-165"),sQuery(id+"F0.wireOp",EDGE,"E1.sketch_text.stroke-166"),sQuery(id+"F0.wireOp",EDGE,"E1.sketch_text.stroke-167"),sQuery(id+"F0.wireOp",EDGE,"E1.sketch_text.stroke-168"),sQuery(id+"F0.wireOp",EDGE,"E1.sketch_text.stroke-169"),sQuery(id+"F0.wireOp",EDGE,"E1.sketch_text.stroke-170"),sQuery(id+"F0.wireOp",EDGE,"E1.sketch_text.stroke-171"),sQuery(id+"F0.wireOp",EDGE,"E1.sketch_text.stroke-172"),sQuery(id+"F0.wireOp",EDGE,"E1.sketch_text.stroke-173"),sQuery(id+"F0.wireOp",EDGE,"E1.sketch_text.stroke-174"),sQuery(id+"F0.wireOp",EDGE,"E1.sketch_text.stroke-175"),sQuery(id+"F0.wireOp",EDGE,"E1.sketch_text.stroke-176"),sQuery(id+"F0.wireOp",EDGE,"E1.sketch_text.stroke-177"),sQuery(id+"F0.wireOp",EDGE,"E1.sketch_text.stroke-178"),sQuery(id+"F0.wireOp",EDGE,"E1.sketch_text.stroke-179"),sQuery(id+"F0.wireOp",EDGE,"E1.sketch_text.stroke-180"),sQuery(id+"F0.wireOp",EDGE,"E1.sketch_text.stroke-181"),sQuery(id+"F0.wireOp",EDGE,"E1.sketch_text.stroke-182"),sQuery(id+"F0.wireOp",EDGE,"E1.sketch_text.stroke-183")])]});
            var Q2;
            Q2=makeQuery(id+"F1.opExtrude","SWEPT_BODY",BODY,{"disambiguationData":[OSD([sQuery(id+"F0.wireOp",EDGE,"E1.sketch_text.stroke-191"),sQuery(id+"F0.wireOp",EDGE,"E1.sketch_text.stroke-192"),sQuery(id+"F0.wireOp",EDGE,"E1.sketch_text.stroke-193"),sQuery(id+"F0.wireOp",EDGE,"E1.sketch_text.stroke-194"),sQuery(id+"F0.wireOp",EDGE,"E1.sketch_text.stroke-195"),sQuery(id+"F0.wireOp",EDGE,"E1.sketch_text.stroke-196"),sQuery(id+"F0.wireOp",EDGE,"E1.sketch_text.stroke-197")])]});
            var Q3;
            Q3=makeQuery(id+"F5.opExtrude","SWEPT_BODY",BODY,{"disambiguationData":[OSD([sQuery(id+"F4.wireOp",EDGE,"E11.0.0"),sQuery(id+"F4.wireOp",EDGE,"E11.0.1"),sQuery(id+"F4.wireOp",EDGE,"E11.0.2"),sQuery(id+"F4.wireOp",EDGE,"E11.0.3")])]});
            var Q4;
            Q4=makeQuery(id+"F1.opExtrude","SWEPT_BODY",BODY,{"disambiguationData":[OSD([sQuery(id+"F0.wireOp",EDGE,"E1.sketch_text.stroke-37"),sQuery(id+"F0.wireOp",EDGE,"E1.sketch_text.stroke-38"),sQuery(id+"F0.wireOp",EDGE,"E1.sketch_text.stroke-39"),sQuery(id+"F0.wireOp",EDGE,"E1.sketch_text.stroke-40"),sQuery(id+"F0.wireOp",EDGE,"E1.sketch_text.stroke-41"),sQuery(id+"F0.wireOp",EDGE,"E1.sketch_text.stroke-42"),sQuery(id+"F0.wireOp",EDGE,"E1.sketch_text.stroke-43"),sQuery(id+"F0.wireOp",EDGE,"E1.sketch_text.stroke-44"),sQuery(id+"F0.wireOp",EDGE,"E1.sketch_text.stroke-45"),sQuery(id+"F0.wireOp",EDGE,"E1.sketch_text.stroke-46"),sQuery(id+"F0.wireOp",EDGE,"E1.sketch_text.stroke-47"),sQuery(id+"F0.wireOp",EDGE,"E1.sketch_text.stroke-48"),sQuery(id+"F0.wireOp",EDGE,"E1.sketch_text.stroke-49")])]});
            var Q5;
            Q5=makeQuery(id+"F1.opExtrude","SWEPT_BODY",BODY,{"disambiguationData":[OSD([sQuery(id+"F0.wireOp",EDGE,"E1.sketch_text.stroke-50"),sQuery(id+"F0.wireOp",EDGE,"E1.sketch_text.stroke-51"),sQuery(id+"F0.wireOp",EDGE,"E1.sketch_text.stroke-52"),sQuery(id+"F0.wireOp",EDGE,"E1.sketch_text.stroke-53"),sQuery(id+"F0.wireOp",EDGE,"E1.sketch_text.stroke-54"),sQuery(id+"F0.wireOp",EDGE,"E1.sketch_text.stroke-55"),sQuery(id+"F0.wireOp",EDGE,"E1.sketch_text.stroke-56"),sQuery(id+"F0.wireOp",EDGE,"E1.sketch_text.stroke-57"),sQuery(id+"F0.wireOp",EDGE,"E1.sketch_text.stroke-58"),sQuery(id+"F0.wireOp",EDGE,"E1.sketch_text.stroke-59"),sQuery(id+"F0.wireOp",EDGE,"E1.sketch_text.stroke-60"),sQuery(id+"F0.wireOp",EDGE,"E1.sketch_text.stroke-61"),sQuery(id+"F0.wireOp",EDGE,"E1.sketch_text.stroke-62"),sQuery(id+"F0.wireOp",EDGE,"E1.sketch_text.stroke-63"),sQuery(id+"F0.wireOp",EDGE,"E1.sketch_text.stroke-64"),sQuery(id+"F0.wireOp",EDGE,"E1.sketch_text.stroke-65"),sQuery(id+"F0.wireOp",EDGE,"E1.sketch_text.stroke-66"),sQuery(id+"F0.wireOp",EDGE,"E1.sketch_text.stroke-67"),sQuery(id+"F0.wireOp",EDGE,"E1.sketch_text.stroke-68"),sQuery(id+"F0.wireOp",EDGE,"E1.sketch_text.stroke-69")])]});
            var Q6;
            Q6=makeQuery(id+"F1.opExtrude","SWEPT_BODY",BODY,{"disambiguationData":[OSD([sQuery(id+"F0.wireOp",EDGE,"E1.sketch_text.stroke-75"),sQuery(id+"F0.wireOp",EDGE,"E1.sketch_text.stroke-76"),sQuery(id+"F0.wireOp",EDGE,"E1.sketch_text.stroke-77"),sQuery(id+"F0.wireOp",EDGE,"E1.sketch_text.stroke-78"),sQuery(id+"F0.wireOp",EDGE,"E1.sketch_text.stroke-79")])]});
            var Q7;
            Q7=makeQuery(id+"F1.opExtrude","SWEPT_BODY",BODY,{"disambiguationData":[OSD([sQuery(id+"F0.wireOp",EDGE,"E1.sketch_text.stroke-11"),sQuery(id+"F0.wireOp",EDGE,"E1.sketch_text.stroke-12"),sQuery(id+"F0.wireOp",EDGE,"E1.sketch_text.stroke-13"),sQuery(id+"F0.wireOp",EDGE,"E1.sketch_text.stroke-14"),sQuery(id+"F0.wireOp",EDGE,"E1.sketch_text.stroke-15"),sQuery(id+"F0.wireOp",EDGE,"E1.sketch_text.stroke-16"),sQuery(id+"F0.wireOp",EDGE,"E1.sketch_text.stroke-17"),sQuery(id+"F0.wireOp",EDGE,"E1.sketch_text.stroke-18"),sQuery(id+"F0.wireOp",EDGE,"E1.sketch_text.stroke-19"),sQuery(id+"F0.wireOp",EDGE,"E1.sketch_text.stroke-20"),sQuery(id+"F0.wireOp",EDGE,"E1.sketch_text.stroke-21"),sQuery(id+"F0.wireOp",EDGE,"E1.sketch_text.stroke-22"),sQuery(id+"F0.wireOp",EDGE,"E1.sketch_text.stroke-23"),sQuery(id+"F0.wireOp",EDGE,"E1.sketch_text.stroke-24")])]});
            var Q8;
            Q8=makeQuery(id+"F1.opExtrude","SWEPT_BODY",BODY,{"disambiguationData":[OSD([sQuery(id+"F0.wireOp",EDGE,"E1.sketch_text.stroke-70"),sQuery(id+"F0.wireOp",EDGE,"E1.sketch_text.stroke-71"),sQuery(id+"F0.wireOp",EDGE,"E1.sketch_text.stroke-72"),sQuery(id+"F0.wireOp",EDGE,"E1.sketch_text.stroke-73"),sQuery(id+"F0.wireOp",EDGE,"E1.sketch_text.stroke-74")])]});
            var Q9;
            Q9=makeQuery(id+"F1.opExtrude","SWEPT_BODY",BODY,{"disambiguationData":[OSD([sQuery(id+"F0.wireOp",EDGE,"E1.sketch_text.stroke-80"),sQuery(id+"F0.wireOp",EDGE,"E1.sketch_text.stroke-81"),sQuery(id+"F0.wireOp",EDGE,"E1.sketch_text.stroke-82"),sQuery(id+"F0.wireOp",EDGE,"E1.sketch_text.stroke-83"),sQuery(id+"F0.wireOp",EDGE,"E1.sketch_text.stroke-84"),sQuery(id+"F0.wireOp",EDGE,"E1.sketch_text.stroke-85"),sQuery(id+"F0.wireOp",EDGE,"E1.sketch_text.stroke-86"),sQuery(id+"F0.wireOp",EDGE,"E1.sketch_text.stroke-87"),sQuery(id+"F0.wireOp",EDGE,"E1.sketch_text.stroke-88"),sQuery(id+"F0.wireOp",EDGE,"E1.sketch_text.stroke-89"),sQuery(id+"F0.wireOp",EDGE,"E1.sketch_text.stroke-90"),sQuery(id+"F0.wireOp",EDGE,"E1.sketch_text.stroke-91"),sQuery(id+"F0.wireOp",EDGE,"E1.sketch_text.stroke-92"),sQuery(id+"F0.wireOp",EDGE,"E1.sketch_text.stroke-93"),sQuery(id+"F0.wireOp",EDGE,"E1.sketch_text.stroke-94"),sQuery(id+"F0.wireOp",EDGE,"E1.sketch_text.stroke-95"),sQuery(id+"F0.wireOp",EDGE,"E1.sketch_text.stroke-96"),sQuery(id+"F0.wireOp",EDGE,"E1.sketch_text.stroke-97"),sQuery(id+"F0.wireOp",EDGE,"E1.sketch_text.stroke-98")])]});
            var Q10;
            Q10=makeQuery(id+"F1.opExtrude","SWEPT_BODY",BODY,{"disambiguationData":[OSD([sQuery(id+"F0.wireOp",EDGE,"E1.sketch_text.stroke-104"),sQuery(id+"F0.wireOp",EDGE,"E1.sketch_text.stroke-105"),sQuery(id+"F0.wireOp",EDGE,"E1.sketch_text.stroke-106"),sQuery(id+"F0.wireOp",EDGE,"E1.sketch_text.stroke-107"),sQuery(id+"F0.wireOp",EDGE,"E1.sketch_text.stroke-108"),sQuery(id+"F0.wireOp",EDGE,"E1.sketch_text.stroke-109"),sQuery(id+"F0.wireOp",EDGE,"E1.sketch_text.stroke-110"),sQuery(id+"F0.wireOp",EDGE,"E1.sketch_text.stroke-111"),sQuery(id+"F0.wireOp",EDGE,"E1.sketch_text.stroke-112"),sQuery(id+"F0.wireOp",EDGE,"E1.sketch_text.stroke-113"),sQuery(id+"F0.wireOp",EDGE,"E1.sketch_text.stroke-114"),sQuery(id+"F0.wireOp",EDGE,"E1.sketch_text.stroke-115"),sQuery(id+"F0.wireOp",EDGE,"E1.sketch_text.stroke-116"),sQuery(id+"F0.wireOp",EDGE,"E1.sketch_text.stroke-117"),sQuery(id+"F0.wireOp",EDGE,"E1.sketch_text.stroke-118"),sQuery(id+"F0.wireOp",EDGE,"E1.sketch_text.stroke-119"),sQuery(id+"F0.wireOp",EDGE,"E1.sketch_text.stroke-120"),sQuery(id+"F0.wireOp",EDGE,"E1.sketch_text.stroke-121"),sQuery(id+"F0.wireOp",EDGE,"E1.sketch_text.stroke-122"),sQuery(id+"F0.wireOp",EDGE,"E1.sketch_text.stroke-123"),sQuery(id+"F0.wireOp",EDGE,"E1.sketch_text.stroke-124"),sQuery(id+"F0.wireOp",EDGE,"E1.sketch_text.stroke-125"),sQuery(id+"F0.wireOp",EDGE,"E1.sketch_text.stroke-126"),sQuery(id+"F0.wireOp",EDGE,"E1.sketch_text.stroke-127"),sQuery(id+"F0.wireOp",EDGE,"E1.sketch_text.stroke-128")])]});
            var Q11;
            Q11=makeQuery(id+"F1.opExtrude","SWEPT_BODY",BODY,{"disambiguationData":[OSD([sQuery(id+"F0.wireOp",EDGE,"E1.sketch_text.stroke-99"),sQuery(id+"F0.wireOp",EDGE,"E1.sketch_text.stroke-100"),sQuery(id+"F0.wireOp",EDGE,"E1.sketch_text.stroke-101"),sQuery(id+"F0.wireOp",EDGE,"E1.sketch_text.stroke-102"),sQuery(id+"F0.wireOp",EDGE,"E1.sketch_text.stroke-103")])]});
            var Q12;
            Q12=makeQuery(id+"F1.opExtrude","SWEPT_BODY",BODY,{"disambiguationData":[OSD([sQuery(id+"F0.wireOp",EDGE,"E1.sketch_text.stroke-184"),sQuery(id+"F0.wireOp",EDGE,"E1.sketch_text.stroke-185"),sQuery(id+"F0.wireOp",EDGE,"E1.sketch_text.stroke-186"),sQuery(id+"F0.wireOp",EDGE,"E1.sketch_text.stroke-187"),sQuery(id+"F0.wireOp",EDGE,"E1.sketch_text.stroke-188"),sQuery(id+"F0.wireOp",EDGE,"E1.sketch_text.stroke-189"),sQuery(id+"F0.wireOp",EDGE,"E1.sketch_text.stroke-190")])]});
            var Q13;
            Q13=makeQuery(id+"F1.opExtrude","SWEPT_BODY",BODY,{"disambiguationData":[OSD([sQuery(id+"F0.wireOp",EDGE,"E1.sketch_text.stroke-25"),sQuery(id+"F0.wireOp",EDGE,"E1.sketch_text.stroke-26"),sQuery(id+"F0.wireOp",EDGE,"E1.sketch_text.stroke-27"),sQuery(id+"F0.wireOp",EDGE,"E1.sketch_text.stroke-28"),sQuery(id+"F0.wireOp",EDGE,"E1.sketch_text.stroke-29"),sQuery(id+"F0.wireOp",EDGE,"E1.sketch_text.stroke-30"),sQuery(id+"F0.wireOp",EDGE,"E1.sketch_text.stroke-31"),sQuery(id+"F0.wireOp",EDGE,"E1.sketch_text.stroke-32"),sQuery(id+"F0.wireOp",EDGE,"E1.sketch_text.stroke-33"),sQuery(id+"F0.wireOp",EDGE,"E1.sketch_text.stroke-34"),sQuery(id+"F0.wireOp",EDGE,"E1.sketch_text.stroke-35"),sQuery(id+"F0.wireOp",EDGE,"E1.sketch_text.stroke-36")])]});
            var Q14;
            Q14=makeQuery(id+"F1.opExtrude","SWEPT_BODY",BODY,{"disambiguationData":[OSD([sQuery(id+"F0.wireOp",EDGE,"E1.sketch_text.stroke-0"),sQuery(id+"F0.wireOp",EDGE,"E1.sketch_text.stroke-1"),sQuery(id+"F0.wireOp",EDGE,"E1.sketch_text.stroke-2"),sQuery(id+"F0.wireOp",EDGE,"E1.sketch_text.stroke-3"),sQuery(id+"F0.wireOp",EDGE,"E1.sketch_text.stroke-4"),sQuery(id+"F0.wireOp",EDGE,"E1.sketch_text.stroke-5"),sQuery(id+"F0.wireOp",EDGE,"E1.sketch_text.stroke-6"),sQuery(id+"F0.wireOp",EDGE,"E1.sketch_text.stroke-7"),sQuery(id+"F0.wireOp",EDGE,"E1.sketch_text.stroke-8"),sQuery(id+"F0.wireOp",EDGE,"E1.sketch_text.stroke-9"),sQuery(id+"F0.wireOp",EDGE,"E1.sketch_text.stroke-10")])]});
            booleanBodies(context, id + "F8", {"operationType" : BooleanOperationType.UNION, "tools" : qUnion([Q0, Q1, Q2, Q3, Q4, Q5, Q6, Q7, Q8, Q9, Q10, Q11, Q12, Q13, Q14])});
        }
        {
            var Q0;
            Q0=makeQuery(id+"F1.opExtrude","SWEPT_BODY",BODY,{"disambiguationData":[OSD([sQuery(id+"F0.wireOp",EDGE,"E2.sketch_text.stroke-0"),sQuery(id+"F0.wireOp",EDGE,"E2.sketch_text.stroke-1"),sQuery(id+"F0.wireOp",EDGE,"E2.sketch_text.stroke-2"),sQuery(id+"F0.wireOp",EDGE,"E2.sketch_text.stroke-3"),sQuery(id+"F0.wireOp",EDGE,"E2.sketch_text.stroke-4"),sQuery(id+"F0.wireOp",EDGE,"E2.sketch_text.stroke-5"),sQuery(id+"F0.wireOp",EDGE,"E2.sketch_text.stroke-6"),sQuery(id+"F0.wireOp",EDGE,"E2.sketch_text.stroke-7"),sQuery(id+"F0.wireOp",EDGE,"E2.sketch_text.stroke-8"),sQuery(id+"F0.wireOp",EDGE,"E2.sketch_text.stroke-9"),sQuery(id+"F0.wireOp",EDGE,"E2.sketch_text.stroke-10"),sQuery(id+"F0.wireOp",EDGE,"E2.sketch_text.stroke-11"),sQuery(id+"F0.wireOp",EDGE,"E2.sketch_text.stroke-12"),sQuery(id+"F0.wireOp",EDGE,"E2.sketch_text.stroke-13"),sQuery(id+"F0.wireOp",EDGE,"E2.sketch_text.stroke-14"),sQuery(id+"F0.wireOp",EDGE,"E2.sketch_text.stroke-15"),sQuery(id+"F0.wireOp",EDGE,"E2.sketch_text.stroke-16"),sQuery(id+"F0.wireOp",EDGE,"E2.sketch_text.stroke-17")])]});
            var Q1;
            Q1=makeQuery(id+"F1.opExtrude","SWEPT_BODY",BODY,{"disambiguationData":[OSD([sQuery(id+"F0.wireOp",EDGE,"E2.sketch_text.stroke-18"),sQuery(id+"F0.wireOp",EDGE,"E2.sketch_text.stroke-19"),sQuery(id+"F0.wireOp",EDGE,"E2.sketch_text.stroke-20"),sQuery(id+"F0.wireOp",EDGE,"E2.sketch_text.stroke-21"),sQuery(id+"F0.wireOp",EDGE,"E2.sketch_text.stroke-22"),sQuery(id+"F0.wireOp",EDGE,"E2.sketch_text.stroke-23"),sQuery(id+"F0.wireOp",EDGE,"E2.sketch_text.stroke-24"),sQuery(id+"F0.wireOp",EDGE,"E2.sketch_text.stroke-25"),sQuery(id+"F0.wireOp",EDGE,"E2.sketch_text.stroke-26"),sQuery(id+"F0.wireOp",EDGE,"E2.sketch_text.stroke-27"),sQuery(id+"F0.wireOp",EDGE,"E2.sketch_text.stroke-28"),sQuery(id+"F0.wireOp",EDGE,"E2.sketch_text.stroke-29"),sQuery(id+"F0.wireOp",EDGE,"E2.sketch_text.stroke-30"),sQuery(id+"F0.wireOp",EDGE,"E2.sketch_text.stroke-31"),sQuery(id+"F0.wireOp",EDGE,"E2.sketch_text.stroke-32"),sQuery(id+"F0.wireOp",EDGE,"E2.sketch_text.stroke-33"),sQuery(id+"F0.wireOp",EDGE,"E2.sketch_text.stroke-34"),sQuery(id+"F0.wireOp",EDGE,"E2.sketch_text.stroke-35"),sQuery(id+"F0.wireOp",EDGE,"E2.sketch_text.stroke-36")])]});
            var Q2;
            Q2=makeQuery(id+"F5.opExtrude","SWEPT_BODY",BODY,{"disambiguationData":[OSD([sQuery(id+"F4.wireOp",EDGE,"E12.0.0"),sQuery(id+"F4.wireOp",EDGE,"E12.0.1"),sQuery(id+"F4.wireOp",EDGE,"E12.0.2"),sQuery(id+"F4.wireOp",EDGE,"E12.0.3")])]});
            var Q3;
            Q3=makeQuery(id+"F1.opExtrude","SWEPT_BODY",BODY,{"disambiguationData":[OSD([sQuery(id+"F0.wireOp",EDGE,"E2.sketch_text.stroke-238"),sQuery(id+"F0.wireOp",EDGE,"E2.sketch_text.stroke-239"),sQuery(id+"F0.wireOp",EDGE,"E2.sketch_text.stroke-240"),sQuery(id+"F0.wireOp",EDGE,"E2.sketch_text.stroke-241"),sQuery(id+"F0.wireOp",EDGE,"E2.sketch_text.stroke-242"),sQuery(id+"F0.wireOp",EDGE,"E2.sketch_text.stroke-243"),sQuery(id+"F0.wireOp",EDGE,"E2.sketch_text.stroke-244"),sQuery(id+"F0.wireOp",EDGE,"E2.sketch_text.stroke-245"),sQuery(id+"F0.wireOp",EDGE,"E2.sketch_text.stroke-246"),sQuery(id+"F0.wireOp",EDGE,"E2.sketch_text.stroke-247"),sQuery(id+"F0.wireOp",EDGE,"E2.sketch_text.stroke-248"),sQuery(id+"F0.wireOp",EDGE,"E2.sketch_text.stroke-249"),sQuery(id+"F0.wireOp",EDGE,"E2.sketch_text.stroke-250")])]});
            var Q4;
            Q4=makeQuery(id+"F1.opExtrude","SWEPT_BODY",BODY,{"disambiguationData":[OSD([sQuery(id+"F0.wireOp",EDGE,"E2.sketch_text.stroke-251"),sQuery(id+"F0.wireOp",EDGE,"E2.sketch_text.stroke-252"),sQuery(id+"F0.wireOp",EDGE,"E2.sketch_text.stroke-253"),sQuery(id+"F0.wireOp",EDGE,"E2.sketch_text.stroke-254"),sQuery(id+"F0.wireOp",EDGE,"E2.sketch_text.stroke-255"),sQuery(id+"F0.wireOp",EDGE,"E2.sketch_text.stroke-256"),sQuery(id+"F0.wireOp",EDGE,"E2.sketch_text.stroke-257"),sQuery(id+"F0.wireOp",EDGE,"E2.sketch_text.stroke-258"),sQuery(id+"F0.wireOp",EDGE,"E2.sketch_text.stroke-259"),sQuery(id+"F0.wireOp",EDGE,"E2.sketch_text.stroke-260"),sQuery(id+"F0.wireOp",EDGE,"E2.sketch_text.stroke-261"),sQuery(id+"F0.wireOp",EDGE,"E2.sketch_text.stroke-262"),sQuery(id+"F0.wireOp",EDGE,"E2.sketch_text.stroke-263"),sQuery(id+"F0.wireOp",EDGE,"E2.sketch_text.stroke-264"),sQuery(id+"F0.wireOp",EDGE,"E2.sketch_text.stroke-265"),sQuery(id+"F0.wireOp",EDGE,"E2.sketch_text.stroke-266"),sQuery(id+"F0.wireOp",EDGE,"E2.sketch_text.stroke-267"),sQuery(id+"F0.wireOp",EDGE,"E2.sketch_text.stroke-268"),sQuery(id+"F0.wireOp",EDGE,"E2.sketch_text.stroke-269"),sQuery(id+"F0.wireOp",EDGE,"E2.sketch_text.stroke-270"),sQuery(id+"F0.wireOp",EDGE,"E2.sketch_text.stroke-271"),sQuery(id+"F0.wireOp",EDGE,"E2.sketch_text.stroke-272"),sQuery(id+"F0.wireOp",EDGE,"E2.sketch_text.stroke-273"),sQuery(id+"F0.wireOp",EDGE,"E2.sketch_text.stroke-274")])]});
            var Q5;
            Q5=makeQuery(id+"F1.opExtrude","SWEPT_BODY",BODY,{"disambiguationData":[OSD([sQuery(id+"F0.wireOp",EDGE,"E2.sketch_text.stroke-275"),sQuery(id+"F0.wireOp",EDGE,"E2.sketch_text.stroke-276"),sQuery(id+"F0.wireOp",EDGE,"E2.sketch_text.stroke-277"),sQuery(id+"F0.wireOp",EDGE,"E2.sketch_text.stroke-278"),sQuery(id+"F0.wireOp",EDGE,"E2.sketch_text.stroke-279"),sQuery(id+"F0.wireOp",EDGE,"E2.sketch_text.stroke-280"),sQuery(id+"F0.wireOp",EDGE,"E2.sketch_text.stroke-281"),sQuery(id+"F0.wireOp",EDGE,"E2.sketch_text.stroke-282"),sQuery(id+"F0.wireOp",EDGE,"E2.sketch_text.stroke-283"),sQuery(id+"F0.wireOp",EDGE,"E2.sketch_text.stroke-284"),sQuery(id+"F0.wireOp",EDGE,"E2.sketch_text.stroke-285"),sQuery(id+"F0.wireOp",EDGE,"E2.sketch_text.stroke-286"),sQuery(id+"F0.wireOp",EDGE,"E2.sketch_text.stroke-287"),sQuery(id+"F0.wireOp",EDGE,"E2.sketch_text.stroke-288")])]});
            var Q6;
            Q6=makeQuery(id+"F1.opExtrude","SWEPT_BODY",BODY,{"disambiguationData":[OSD([sQuery(id+"F0.wireOp",EDGE,"E2.sketch_text.stroke-201"),sQuery(id+"F0.wireOp",EDGE,"E2.sketch_text.stroke-202"),sQuery(id+"F0.wireOp",EDGE,"E2.sketch_text.stroke-203"),sQuery(id+"F0.wireOp",EDGE,"E2.sketch_text.stroke-204"),sQuery(id+"F0.wireOp",EDGE,"E2.sketch_text.stroke-205"),sQuery(id+"F0.wireOp",EDGE,"E2.sketch_text.stroke-206"),sQuery(id+"F0.wireOp",EDGE,"E2.sketch_text.stroke-207"),sQuery(id+"F0.wireOp",EDGE,"E2.sketch_text.stroke-208"),sQuery(id+"F0.wireOp",EDGE,"E2.sketch_text.stroke-209"),sQuery(id+"F0.wireOp",EDGE,"E2.sketch_text.stroke-210"),sQuery(id+"F0.wireOp",EDGE,"E2.sketch_text.stroke-211"),sQuery(id+"F0.wireOp",EDGE,"E2.sketch_text.stroke-212"),sQuery(id+"F0.wireOp",EDGE,"E2.sketch_text.stroke-213")])]});
            var Q7;
            Q7=makeQuery(id+"F1.opExtrude","SWEPT_BODY",BODY,{"disambiguationData":[OSD([sQuery(id+"F0.wireOp",EDGE,"E2.sketch_text.stroke-214"),sQuery(id+"F0.wireOp",EDGE,"E2.sketch_text.stroke-215"),sQuery(id+"F0.wireOp",EDGE,"E2.sketch_text.stroke-216"),sQuery(id+"F0.wireOp",EDGE,"E2.sketch_text.stroke-217"),sQuery(id+"F0.wireOp",EDGE,"E2.sketch_text.stroke-218"),sQuery(id+"F0.wireOp",EDGE,"E2.sketch_text.stroke-219"),sQuery(id+"F0.wireOp",EDGE,"E2.sketch_text.stroke-220"),sQuery(id+"F0.wireOp",EDGE,"E2.sketch_text.stroke-221"),sQuery(id+"F0.wireOp",EDGE,"E2.sketch_text.stroke-222"),sQuery(id+"F0.wireOp",EDGE,"E2.sketch_text.stroke-223"),sQuery(id+"F0.wireOp",EDGE,"E2.sketch_text.stroke-224"),sQuery(id+"F0.wireOp",EDGE,"E2.sketch_text.stroke-225"),sQuery(id+"F0.wireOp",EDGE,"E2.sketch_text.stroke-226"),sQuery(id+"F0.wireOp",EDGE,"E2.sketch_text.stroke-227"),sQuery(id+"F0.wireOp",EDGE,"E2.sketch_text.stroke-228"),sQuery(id+"F0.wireOp",EDGE,"E2.sketch_text.stroke-229"),sQuery(id+"F0.wireOp",EDGE,"E2.sketch_text.stroke-230"),sQuery(id+"F0.wireOp",EDGE,"E2.sketch_text.stroke-231"),sQuery(id+"F0.wireOp",EDGE,"E2.sketch_text.stroke-232"),sQuery(id+"F0.wireOp",EDGE,"E2.sketch_text.stroke-233"),sQuery(id+"F0.wireOp",EDGE,"E2.sketch_text.stroke-234"),sQuery(id+"F0.wireOp",EDGE,"E2.sketch_text.stroke-235"),sQuery(id+"F0.wireOp",EDGE,"E2.sketch_text.stroke-236"),sQuery(id+"F0.wireOp",EDGE,"E2.sketch_text.stroke-237")])]});
            var Q8;
            Q8=makeQuery(id+"F1.opExtrude","SWEPT_BODY",BODY,{"disambiguationData":[OSD([sQuery(id+"F0.wireOp",EDGE,"E2.sketch_text.stroke-322"),sQuery(id+"F0.wireOp",EDGE,"E2.sketch_text.stroke-323"),sQuery(id+"F0.wireOp",EDGE,"E2.sketch_text.stroke-324"),sQuery(id+"F0.wireOp",EDGE,"E2.sketch_text.stroke-325"),sQuery(id+"F0.wireOp",EDGE,"E2.sketch_text.stroke-326"),sQuery(id+"F0.wireOp",EDGE,"E2.sketch_text.stroke-327"),sQuery(id+"F0.wireOp",EDGE,"E2.sketch_text.stroke-328"),sQuery(id+"F0.wireOp",EDGE,"E2.sketch_text.stroke-329"),sQuery(id+"F0.wireOp",EDGE,"E2.sketch_text.stroke-330"),sQuery(id+"F0.wireOp",EDGE,"E2.sketch_text.stroke-331"),sQuery(id+"F0.wireOp",EDGE,"E2.sketch_text.stroke-332"),sQuery(id+"F0.wireOp",EDGE,"E2.sketch_text.stroke-333"),sQuery(id+"F0.wireOp",EDGE,"E2.sketch_text.stroke-334"),sQuery(id+"F0.wireOp",EDGE,"E2.sketch_text.stroke-335"),sQuery(id+"F0.wireOp",EDGE,"E2.sketch_text.stroke-336"),sQuery(id+"F0.wireOp",EDGE,"E2.sketch_text.stroke-337"),sQuery(id+"F0.wireOp",EDGE,"E2.sketch_text.stroke-338"),sQuery(id+"F0.wireOp",EDGE,"E2.sketch_text.stroke-339"),sQuery(id+"F0.wireOp",EDGE,"E2.sketch_text.stroke-340")])]});
            var Q9;
            Q9=makeQuery(id+"F1.opExtrude","SWEPT_BODY",BODY,{"disambiguationData":[OSD([sQuery(id+"F0.wireOp",EDGE,"E2.sketch_text.stroke-37"),sQuery(id+"F0.wireOp",EDGE,"E2.sketch_text.stroke-38"),sQuery(id+"F0.wireOp",EDGE,"E2.sketch_text.stroke-39"),sQuery(id+"F0.wireOp",EDGE,"E2.sketch_text.stroke-40"),sQuery(id+"F0.wireOp",EDGE,"E2.sketch_text.stroke-41"),sQuery(id+"F0.wireOp",EDGE,"E2.sketch_text.stroke-42"),sQuery(id+"F0.wireOp",EDGE,"E2.sketch_text.stroke-43"),sQuery(id+"F0.wireOp",EDGE,"E2.sketch_text.stroke-44"),sQuery(id+"F0.wireOp",EDGE,"E2.sketch_text.stroke-45"),sQuery(id+"F0.wireOp",EDGE,"E2.sketch_text.stroke-46"),sQuery(id+"F0.wireOp",EDGE,"E2.sketch_text.stroke-47"),sQuery(id+"F0.wireOp",EDGE,"E2.sketch_text.stroke-48"),sQuery(id+"F0.wireOp",EDGE,"E2.sketch_text.stroke-49"),sQuery(id+"F0.wireOp",EDGE,"E2.sketch_text.stroke-50"),sQuery(id+"F0.wireOp",EDGE,"E2.sketch_text.stroke-51"),sQuery(id+"F0.wireOp",EDGE,"E2.sketch_text.stroke-52"),sQuery(id+"F0.wireOp",EDGE,"E2.sketch_text.stroke-53"),sQuery(id+"F0.wireOp",EDGE,"E2.sketch_text.stroke-54"),sQuery(id+"F0.wireOp",EDGE,"E2.sketch_text.stroke-55"),sQuery(id+"F0.wireOp",EDGE,"E2.sketch_text.stroke-56"),sQuery(id+"F0.wireOp",EDGE,"E2.sketch_text.stroke-57"),sQuery(id+"F0.wireOp",EDGE,"E2.sketch_text.stroke-58"),sQuery(id+"F0.wireOp",EDGE,"E2.sketch_text.stroke-59"),sQuery(id+"F0.wireOp",EDGE,"E2.sketch_text.stroke-60"),sQuery(id+"F0.wireOp",EDGE,"E2.sketch_text.stroke-61"),sQuery(id+"F0.wireOp",EDGE,"E2.sketch_text.stroke-62"),sQuery(id+"F0.wireOp",EDGE,"E2.sketch_text.stroke-63"),sQuery(id+"F0.wireOp",EDGE,"E2.sketch_text.stroke-64"),sQuery(id+"F0.wireOp",EDGE,"E2.sketch_text.stroke-65"),sQuery(id+"F0.wireOp",EDGE,"E2.sketch_text.stroke-66"),sQuery(id+"F0.wireOp",EDGE,"E2.sketch_text.stroke-67"),sQuery(id+"F0.wireOp",EDGE,"E2.sketch_text.stroke-68"),sQuery(id+"F0.wireOp",EDGE,"E2.sketch_text.stroke-69"),sQuery(id+"F0.wireOp",EDGE,"E2.sketch_text.stroke-70"),sQuery(id+"F0.wireOp",EDGE,"E2.sketch_text.stroke-71"),sQuery(id+"F0.wireOp",EDGE,"E2.sketch_text.stroke-72")])]});
            var Q10;
            Q10=makeQuery(id+"F1.opExtrude","SWEPT_BODY",BODY,{"disambiguationData":[OSD([sQuery(id+"F0.wireOp",EDGE,"E2.sketch_text.stroke-176"),sQuery(id+"F0.wireOp",EDGE,"E2.sketch_text.stroke-177"),sQuery(id+"F0.wireOp",EDGE,"E2.sketch_text.stroke-178"),sQuery(id+"F0.wireOp",EDGE,"E2.sketch_text.stroke-179"),sQuery(id+"F0.wireOp",EDGE,"E2.sketch_text.stroke-180"),sQuery(id+"F0.wireOp",EDGE,"E2.sketch_text.stroke-181"),sQuery(id+"F0.wireOp",EDGE,"E2.sketch_text.stroke-182"),sQuery(id+"F0.wireOp",EDGE,"E2.sketch_text.stroke-183"),sQuery(id+"F0.wireOp",EDGE,"E2.sketch_text.stroke-184"),sQuery(id+"F0.wireOp",EDGE,"E2.sketch_text.stroke-185"),sQuery(id+"F0.wireOp",EDGE,"E2.sketch_text.stroke-186"),sQuery(id+"F0.wireOp",EDGE,"E2.sketch_text.stroke-187"),sQuery(id+"F0.wireOp",EDGE,"E2.sketch_text.stroke-188"),sQuery(id+"F0.wireOp",EDGE,"E2.sketch_text.stroke-189"),sQuery(id+"F0.wireOp",EDGE,"E2.sketch_text.stroke-190"),sQuery(id+"F0.wireOp",EDGE,"E2.sketch_text.stroke-191"),sQuery(id+"F0.wireOp",EDGE,"E2.sketch_text.stroke-192"),sQuery(id+"F0.wireOp",EDGE,"E2.sketch_text.stroke-193"),sQuery(id+"F0.wireOp",EDGE,"E2.sketch_text.stroke-194"),sQuery(id+"F0.wireOp",EDGE,"E2.sketch_text.stroke-195"),sQuery(id+"F0.wireOp",EDGE,"E2.sketch_text.stroke-196"),sQuery(id+"F0.wireOp",EDGE,"E2.sketch_text.stroke-197"),sQuery(id+"F0.wireOp",EDGE,"E2.sketch_text.stroke-198"),sQuery(id+"F0.wireOp",EDGE,"E2.sketch_text.stroke-199"),sQuery(id+"F0.wireOp",EDGE,"E2.sketch_text.stroke-200")])]});
            var Q11;
            Q11=makeQuery(id+"F1.opExtrude","SWEPT_BODY",BODY,{"disambiguationData":[OSD([sQuery(id+"F0.wireOp",EDGE,"E2.sketch_text.stroke-171"),sQuery(id+"F0.wireOp",EDGE,"E2.sketch_text.stroke-172"),sQuery(id+"F0.wireOp",EDGE,"E2.sketch_text.stroke-173"),sQuery(id+"F0.wireOp",EDGE,"E2.sketch_text.stroke-174"),sQuery(id+"F0.wireOp",EDGE,"E2.sketch_text.stroke-175")])]});
            var Q12;
            Q12=makeQuery(id+"F1.opExtrude","SWEPT_BODY",BODY,{"disambiguationData":[OSD([sQuery(id+"F0.wireOp",EDGE,"E2.sketch_text.stroke-135"),sQuery(id+"F0.wireOp",EDGE,"E2.sketch_text.stroke-136"),sQuery(id+"F0.wireOp",EDGE,"E2.sketch_text.stroke-137"),sQuery(id+"F0.wireOp",EDGE,"E2.sketch_text.stroke-138"),sQuery(id+"F0.wireOp",EDGE,"E2.sketch_text.stroke-139"),sQuery(id+"F0.wireOp",EDGE,"E2.sketch_text.stroke-140"),sQuery(id+"F0.wireOp",EDGE,"E2.sketch_text.stroke-141"),sQuery(id+"F0.wireOp",EDGE,"E2.sketch_text.stroke-142"),sQuery(id+"F0.wireOp",EDGE,"E2.sketch_text.stroke-143"),sQuery(id+"F0.wireOp",EDGE,"E2.sketch_text.stroke-144"),sQuery(id+"F0.wireOp",EDGE,"E2.sketch_text.stroke-145"),sQuery(id+"F0.wireOp",EDGE,"E2.sketch_text.stroke-146"),sQuery(id+"F0.wireOp",EDGE,"E2.sketch_text.stroke-147"),sQuery(id+"F0.wireOp",EDGE,"E2.sketch_text.stroke-148"),sQuery(id+"F0.wireOp",EDGE,"E2.sketch_text.stroke-149"),sQuery(id+"F0.wireOp",EDGE,"E2.sketch_text.stroke-150"),sQuery(id+"F0.wireOp",EDGE,"E2.sketch_text.stroke-151"),sQuery(id+"F0.wireOp",EDGE,"E2.sketch_text.stroke-152"),sQuery(id+"F0.wireOp",EDGE,"E2.sketch_text.stroke-153"),sQuery(id+"F0.wireOp",EDGE,"E2.sketch_text.stroke-154"),sQuery(id+"F0.wireOp",EDGE,"E2.sketch_text.stroke-155"),sQuery(id+"F0.wireOp",EDGE,"E2.sketch_text.stroke-156"),sQuery(id+"F0.wireOp",EDGE,"E2.sketch_text.stroke-157"),sQuery(id+"F0.wireOp",EDGE,"E2.sketch_text.stroke-158"),sQuery(id+"F0.wireOp",EDGE,"E2.sketch_text.stroke-159"),sQuery(id+"F0.wireOp",EDGE,"E2.sketch_text.stroke-160"),sQuery(id+"F0.wireOp",EDGE,"E2.sketch_text.stroke-161"),sQuery(id+"F0.wireOp",EDGE,"E2.sketch_text.stroke-162"),sQuery(id+"F0.wireOp",EDGE,"E2.sketch_text.stroke-163"),sQuery(id+"F0.wireOp",EDGE,"E2.sketch_text.stroke-164"),sQuery(id+"F0.wireOp",EDGE,"E2.sketch_text.stroke-165"),sQuery(id+"F0.wireOp",EDGE,"E2.sketch_text.stroke-166"),sQuery(id+"F0.wireOp",EDGE,"E2.sketch_text.stroke-167"),sQuery(id+"F0.wireOp",EDGE,"E2.sketch_text.stroke-168"),sQuery(id+"F0.wireOp",EDGE,"E2.sketch_text.stroke-169"),sQuery(id+"F0.wireOp",EDGE,"E2.sketch_text.stroke-170")])]});
            var Q13;
            Q13=makeQuery(id+"F1.opExtrude","SWEPT_BODY",BODY,{"disambiguationData":[OSD([sQuery(id+"F0.wireOp",EDGE,"E2.sketch_text.stroke-73"),sQuery(id+"F0.wireOp",EDGE,"E2.sketch_text.stroke-74"),sQuery(id+"F0.wireOp",EDGE,"E2.sketch_text.stroke-75"),sQuery(id+"F0.wireOp",EDGE,"E2.sketch_text.stroke-76"),sQuery(id+"F0.wireOp",EDGE,"E2.sketch_text.stroke-77"),sQuery(id+"F0.wireOp",EDGE,"E2.sketch_text.stroke-78"),sQuery(id+"F0.wireOp",EDGE,"E2.sketch_text.stroke-79"),sQuery(id+"F0.wireOp",EDGE,"E2.sketch_text.stroke-80"),sQuery(id+"F0.wireOp",EDGE,"E2.sketch_text.stroke-81"),sQuery(id+"F0.wireOp",EDGE,"E2.sketch_text.stroke-82"),sQuery(id+"F0.wireOp",EDGE,"E2.sketch_text.stroke-83"),sQuery(id+"F0.wireOp",EDGE,"E2.sketch_text.stroke-84"),sQuery(id+"F0.wireOp",EDGE,"E2.sketch_text.stroke-85"),sQuery(id+"F0.wireOp",EDGE,"E2.sketch_text.stroke-86"),sQuery(id+"F0.wireOp",EDGE,"E2.sketch_text.stroke-87"),sQuery(id+"F0.wireOp",EDGE,"E2.sketch_text.stroke-88"),sQuery(id+"F0.wireOp",EDGE,"E2.sketch_text.stroke-89"),sQuery(id+"F0.wireOp",EDGE,"E2.sketch_text.stroke-90"),sQuery(id+"F0.wireOp",EDGE,"E2.sketch_text.stroke-91"),sQuery(id+"F0.wireOp",EDGE,"E2.sketch_text.stroke-92"),sQuery(id+"F0.wireOp",EDGE,"E2.sketch_text.stroke-93"),sQuery(id+"F0.wireOp",EDGE,"E2.sketch_text.stroke-94"),sQuery(id+"F0.wireOp",EDGE,"E2.sketch_text.stroke-95"),sQuery(id+"F0.wireOp",EDGE,"E2.sketch_text.stroke-96"),sQuery(id+"F0.wireOp",EDGE,"E2.sketch_text.stroke-97"),sQuery(id+"F0.wireOp",EDGE,"E2.sketch_text.stroke-98")])]});
            var Q14;
            Q14=makeQuery(id+"F1.opExtrude","SWEPT_BODY",BODY,{"disambiguationData":[OSD([sQuery(id+"F0.wireOp",EDGE,"E2.sketch_text.stroke-116"),sQuery(id+"F0.wireOp",EDGE,"E2.sketch_text.stroke-117"),sQuery(id+"F0.wireOp",EDGE,"E2.sketch_text.stroke-118"),sQuery(id+"F0.wireOp",EDGE,"E2.sketch_text.stroke-119"),sQuery(id+"F0.wireOp",EDGE,"E2.sketch_text.stroke-120"),sQuery(id+"F0.wireOp",EDGE,"E2.sketch_text.stroke-121"),sQuery(id+"F0.wireOp",EDGE,"E2.sketch_text.stroke-122"),sQuery(id+"F0.wireOp",EDGE,"E2.sketch_text.stroke-123"),sQuery(id+"F0.wireOp",EDGE,"E2.sketch_text.stroke-124"),sQuery(id+"F0.wireOp",EDGE,"E2.sketch_text.stroke-125"),sQuery(id+"F0.wireOp",EDGE,"E2.sketch_text.stroke-126"),sQuery(id+"F0.wireOp",EDGE,"E2.sketch_text.stroke-127"),sQuery(id+"F0.wireOp",EDGE,"E2.sketch_text.stroke-128"),sQuery(id+"F0.wireOp",EDGE,"E2.sketch_text.stroke-129"),sQuery(id+"F0.wireOp",EDGE,"E2.sketch_text.stroke-130"),sQuery(id+"F0.wireOp",EDGE,"E2.sketch_text.stroke-131"),sQuery(id+"F0.wireOp",EDGE,"E2.sketch_text.stroke-132"),sQuery(id+"F0.wireOp",EDGE,"E2.sketch_text.stroke-133"),sQuery(id+"F0.wireOp",EDGE,"E2.sketch_text.stroke-134")])]});
            var Q15;
            Q15=makeQuery(id+"F1.opExtrude","SWEPT_BODY",BODY,{"disambiguationData":[OSD([sQuery(id+"F0.wireOp",EDGE,"E2.sketch_text.stroke-99"),sQuery(id+"F0.wireOp",EDGE,"E2.sketch_text.stroke-100"),sQuery(id+"F0.wireOp",EDGE,"E2.sketch_text.stroke-101"),sQuery(id+"F0.wireOp",EDGE,"E2.sketch_text.stroke-102"),sQuery(id+"F0.wireOp",EDGE,"E2.sketch_text.stroke-103"),sQuery(id+"F0.wireOp",EDGE,"E2.sketch_text.stroke-104"),sQuery(id+"F0.wireOp",EDGE,"E2.sketch_text.stroke-105"),sQuery(id+"F0.wireOp",EDGE,"E2.sketch_text.stroke-106"),sQuery(id+"F0.wireOp",EDGE,"E2.sketch_text.stroke-107"),sQuery(id+"F0.wireOp",EDGE,"E2.sketch_text.stroke-108"),sQuery(id+"F0.wireOp",EDGE,"E2.sketch_text.stroke-109"),sQuery(id+"F0.wireOp",EDGE,"E2.sketch_text.stroke-110"),sQuery(id+"F0.wireOp",EDGE,"E2.sketch_text.stroke-111"),sQuery(id+"F0.wireOp",EDGE,"E2.sketch_text.stroke-112"),sQuery(id+"F0.wireOp",EDGE,"E2.sketch_text.stroke-113"),sQuery(id+"F0.wireOp",EDGE,"E2.sketch_text.stroke-114"),sQuery(id+"F0.wireOp",EDGE,"E2.sketch_text.stroke-115")])]});
            var Q16;
            Q16=makeQuery(id+"F1.opExtrude","SWEPT_BODY",BODY,{"disambiguationData":[OSD([sQuery(id+"F0.wireOp",EDGE,"E2.sketch_text.stroke-318"),sQuery(id+"F0.wireOp",EDGE,"E2.sketch_text.stroke-319"),sQuery(id+"F0.wireOp",EDGE,"E2.sketch_text.stroke-320"),sQuery(id+"F0.wireOp",EDGE,"E2.sketch_text.stroke-321")])]});
            var Q17;
            Q17=makeQuery(id+"F1.opExtrude","SWEPT_BODY",BODY,{"disambiguationData":[OSD([sQuery(id+"F0.wireOp",EDGE,"E2.sketch_text.stroke-295"),sQuery(id+"F0.wireOp",EDGE,"E2.sketch_text.stroke-296"),sQuery(id+"F0.wireOp",EDGE,"E2.sketch_text.stroke-297"),sQuery(id+"F0.wireOp",EDGE,"E2.sketch_text.stroke-298"),sQuery(id+"F0.wireOp",EDGE,"E2.sketch_text.stroke-299"),sQuery(id+"F0.wireOp",EDGE,"E2.sketch_text.stroke-300"),sQuery(id+"F0.wireOp",EDGE,"E2.sketch_text.stroke-301"),sQuery(id+"F0.wireOp",EDGE,"E2.sketch_text.stroke-302"),sQuery(id+"F0.wireOp",EDGE,"E2.sketch_text.stroke-303")])]});
            var Q18;
            Q18=makeQuery(id+"F1.opExtrude","SWEPT_BODY",BODY,{"disambiguationData":[OSD([sQuery(id+"F0.wireOp",EDGE,"E2.sketch_text.stroke-289"),sQuery(id+"F0.wireOp",EDGE,"E2.sketch_text.stroke-290"),sQuery(id+"F0.wireOp",EDGE,"E2.sketch_text.stroke-291"),sQuery(id+"F0.wireOp",EDGE,"E2.sketch_text.stroke-292"),sQuery(id+"F0.wireOp",EDGE,"E2.sketch_text.stroke-293"),sQuery(id+"F0.wireOp",EDGE,"E2.sketch_text.stroke-294")])]});
            var Q19;
            Q19=makeQuery(id+"F1.opExtrude","SWEPT_BODY",BODY,{"disambiguationData":[OSD([sQuery(id+"F0.wireOp",EDGE,"E2.sketch_text.stroke-304"),sQuery(id+"F0.wireOp",EDGE,"E2.sketch_text.stroke-305"),sQuery(id+"F0.wireOp",EDGE,"E2.sketch_text.stroke-306"),sQuery(id+"F0.wireOp",EDGE,"E2.sketch_text.stroke-307"),sQuery(id+"F0.wireOp",EDGE,"E2.sketch_text.stroke-308"),sQuery(id+"F0.wireOp",EDGE,"E2.sketch_text.stroke-309"),sQuery(id+"F0.wireOp",EDGE,"E2.sketch_text.stroke-310"),sQuery(id+"F0.wireOp",EDGE,"E2.sketch_text.stroke-311"),sQuery(id+"F0.wireOp",EDGE,"E2.sketch_text.stroke-312"),sQuery(id+"F0.wireOp",EDGE,"E2.sketch_text.stroke-313"),sQuery(id+"F0.wireOp",EDGE,"E2.sketch_text.stroke-314"),sQuery(id+"F0.wireOp",EDGE,"E2.sketch_text.stroke-315"),sQuery(id+"F0.wireOp",EDGE,"E2.sketch_text.stroke-316"),sQuery(id+"F0.wireOp",EDGE,"E2.sketch_text.stroke-317")])]});
            booleanBodies(context, id + "F9", {"operationType" : BooleanOperationType.UNION, "tools" : qUnion([Q0, Q1, Q2, Q3, Q4, Q5, Q6, Q7, Q8, Q9, Q10, Q11, Q12, Q13, Q14, Q15, Q16, Q17, Q18, Q19])});
        }
        {
            var Q0;
            Q0=makeQuery(id+"F1.opExtrude","SWEPT_BODY",BODY,{"disambiguationData":[OSD([sQuery(id+"F0.wireOp",EDGE,"E3.sketch_text.stroke-105"),sQuery(id+"F0.wireOp",EDGE,"E3.sketch_text.stroke-106"),sQuery(id+"F0.wireOp",EDGE,"E3.sketch_text.stroke-107"),sQuery(id+"F0.wireOp",EDGE,"E3.sketch_text.stroke-108"),sQuery(id+"F0.wireOp",EDGE,"E3.sketch_text.stroke-109")])]});
            var Q1;
            Q1=makeQuery(id+"F1.opExtrude","SWEPT_BODY",BODY,{"disambiguationData":[OSD([sQuery(id+"F0.wireOp",EDGE,"E3.sketch_text.stroke-175"),sQuery(id+"F0.wireOp",EDGE,"E3.sketch_text.stroke-176"),sQuery(id+"F0.wireOp",EDGE,"E3.sketch_text.stroke-177"),sQuery(id+"F0.wireOp",EDGE,"E3.sketch_text.stroke-178"),sQuery(id+"F0.wireOp",EDGE,"E3.sketch_text.stroke-179"),sQuery(id+"F0.wireOp",EDGE,"E3.sketch_text.stroke-180"),sQuery(id+"F0.wireOp",EDGE,"E3.sketch_text.stroke-181"),sQuery(id+"F0.wireOp",EDGE,"E3.sketch_text.stroke-182"),sQuery(id+"F0.wireOp",EDGE,"E3.sketch_text.stroke-183"),sQuery(id+"F0.wireOp",EDGE,"E3.sketch_text.stroke-184"),sQuery(id+"F0.wireOp",EDGE,"E3.sketch_text.stroke-185"),sQuery(id+"F0.wireOp",EDGE,"E3.sketch_text.stroke-186"),sQuery(id+"F0.wireOp",EDGE,"E3.sketch_text.stroke-187"),sQuery(id+"F0.wireOp",EDGE,"E3.sketch_text.stroke-188"),sQuery(id+"F0.wireOp",EDGE,"E3.sketch_text.stroke-189"),sQuery(id+"F0.wireOp",EDGE,"E3.sketch_text.stroke-190"),sQuery(id+"F0.wireOp",EDGE,"E3.sketch_text.stroke-191"),sQuery(id+"F0.wireOp",EDGE,"E3.sketch_text.stroke-192"),sQuery(id+"F0.wireOp",EDGE,"E3.sketch_text.stroke-193")])]});
            var Q2;
            Q2=makeQuery(id+"F1.opExtrude","SWEPT_BODY",BODY,{"disambiguationData":[OSD([sQuery(id+"F0.wireOp",EDGE,"E3.sketch_text.stroke-156"),sQuery(id+"F0.wireOp",EDGE,"E3.sketch_text.stroke-157"),sQuery(id+"F0.wireOp",EDGE,"E3.sketch_text.stroke-158"),sQuery(id+"F0.wireOp",EDGE,"E3.sketch_text.stroke-159"),sQuery(id+"F0.wireOp",EDGE,"E3.sketch_text.stroke-160"),sQuery(id+"F0.wireOp",EDGE,"E3.sketch_text.stroke-161"),sQuery(id+"F0.wireOp",EDGE,"E3.sketch_text.stroke-162"),sQuery(id+"F0.wireOp",EDGE,"E3.sketch_text.stroke-163"),sQuery(id+"F0.wireOp",EDGE,"E3.sketch_text.stroke-164"),sQuery(id+"F0.wireOp",EDGE,"E3.sketch_text.stroke-165"),sQuery(id+"F0.wireOp",EDGE,"E3.sketch_text.stroke-166"),sQuery(id+"F0.wireOp",EDGE,"E3.sketch_text.stroke-167"),sQuery(id+"F0.wireOp",EDGE,"E3.sketch_text.stroke-168"),sQuery(id+"F0.wireOp",EDGE,"E3.sketch_text.stroke-169"),sQuery(id+"F0.wireOp",EDGE,"E3.sketch_text.stroke-170"),sQuery(id+"F0.wireOp",EDGE,"E3.sketch_text.stroke-171"),sQuery(id+"F0.wireOp",EDGE,"E3.sketch_text.stroke-172"),sQuery(id+"F0.wireOp",EDGE,"E3.sketch_text.stroke-173"),sQuery(id+"F0.wireOp",EDGE,"E3.sketch_text.stroke-174")])]});
            var Q3;
            Q3=makeQuery(id+"F1.opExtrude","SWEPT_BODY",BODY,{"disambiguationData":[OSD([sQuery(id+"F0.wireOp",EDGE,"E3.sketch_text.stroke-194"),sQuery(id+"F0.wireOp",EDGE,"E3.sketch_text.stroke-195"),sQuery(id+"F0.wireOp",EDGE,"E3.sketch_text.stroke-196"),sQuery(id+"F0.wireOp",EDGE,"E3.sketch_text.stroke-197"),sQuery(id+"F0.wireOp",EDGE,"E3.sketch_text.stroke-198"),sQuery(id+"F0.wireOp",EDGE,"E3.sketch_text.stroke-199"),sQuery(id+"F0.wireOp",EDGE,"E3.sketch_text.stroke-200"),sQuery(id+"F0.wireOp",EDGE,"E3.sketch_text.stroke-201"),sQuery(id+"F0.wireOp",EDGE,"E3.sketch_text.stroke-202"),sQuery(id+"F0.wireOp",EDGE,"E3.sketch_text.stroke-203"),sQuery(id+"F0.wireOp",EDGE,"E3.sketch_text.stroke-204"),sQuery(id+"F0.wireOp",EDGE,"E3.sketch_text.stroke-205"),sQuery(id+"F0.wireOp",EDGE,"E3.sketch_text.stroke-206"),sQuery(id+"F0.wireOp",EDGE,"E3.sketch_text.stroke-207"),sQuery(id+"F0.wireOp",EDGE,"E3.sketch_text.stroke-208"),sQuery(id+"F0.wireOp",EDGE,"E3.sketch_text.stroke-209"),sQuery(id+"F0.wireOp",EDGE,"E3.sketch_text.stroke-210"),sQuery(id+"F0.wireOp",EDGE,"E3.sketch_text.stroke-211"),sQuery(id+"F0.wireOp",EDGE,"E3.sketch_text.stroke-212"),sQuery(id+"F0.wireOp",EDGE,"E3.sketch_text.stroke-213"),sQuery(id+"F0.wireOp",EDGE,"E3.sketch_text.stroke-214"),sQuery(id+"F0.wireOp",EDGE,"E3.sketch_text.stroke-215"),sQuery(id+"F0.wireOp",EDGE,"E3.sketch_text.stroke-216"),sQuery(id+"F0.wireOp",EDGE,"E3.sketch_text.stroke-217"),sQuery(id+"F0.wireOp",EDGE,"E3.sketch_text.stroke-218"),sQuery(id+"F0.wireOp",EDGE,"E3.sketch_text.stroke-219"),sQuery(id+"F0.wireOp",EDGE,"E3.sketch_text.stroke-220"),sQuery(id+"F0.wireOp",EDGE,"E3.sketch_text.stroke-221"),sQuery(id+"F0.wireOp",EDGE,"E3.sketch_text.stroke-222"),sQuery(id+"F0.wireOp",EDGE,"E3.sketch_text.stroke-223"),sQuery(id+"F0.wireOp",EDGE,"E3.sketch_text.stroke-224"),sQuery(id+"F0.wireOp",EDGE,"E3.sketch_text.stroke-225"),sQuery(id+"F0.wireOp",EDGE,"E3.sketch_text.stroke-226"),sQuery(id+"F0.wireOp",EDGE,"E3.sketch_text.stroke-227"),sQuery(id+"F0.wireOp",EDGE,"E3.sketch_text.stroke-228"),sQuery(id+"F0.wireOp",EDGE,"E3.sketch_text.stroke-229")])]});
            var Q4;
            Q4=makeQuery(id+"F1.opExtrude","SWEPT_BODY",BODY,{"disambiguationData":[OSD([sQuery(id+"F0.wireOp",EDGE,"E3.sketch_text.stroke-119"),sQuery(id+"F0.wireOp",EDGE,"E3.sketch_text.stroke-120"),sQuery(id+"F0.wireOp",EDGE,"E3.sketch_text.stroke-121"),sQuery(id+"F0.wireOp",EDGE,"E3.sketch_text.stroke-122"),sQuery(id+"F0.wireOp",EDGE,"E3.sketch_text.stroke-123"),sQuery(id+"F0.wireOp",EDGE,"E3.sketch_text.stroke-124"),sQuery(id+"F0.wireOp",EDGE,"E3.sketch_text.stroke-125"),sQuery(id+"F0.wireOp",EDGE,"E3.sketch_text.stroke-126")])]});
            var Q5;
            Q5=makeQuery(id+"F1.opExtrude","SWEPT_BODY",BODY,{"disambiguationData":[OSD([sQuery(id+"F0.wireOp",EDGE,"E3.sketch_text.stroke-115"),sQuery(id+"F0.wireOp",EDGE,"E3.sketch_text.stroke-116"),sQuery(id+"F0.wireOp",EDGE,"E3.sketch_text.stroke-117"),sQuery(id+"F0.wireOp",EDGE,"E3.sketch_text.stroke-118")])]});
            var Q6;
            Q6=makeQuery(id+"F1.opExtrude","SWEPT_BODY",BODY,{"disambiguationData":[OSD([sQuery(id+"F0.wireOp",EDGE,"E3.sketch_text.stroke-127"),sQuery(id+"F0.wireOp",EDGE,"E3.sketch_text.stroke-128"),sQuery(id+"F0.wireOp",EDGE,"E3.sketch_text.stroke-129"),sQuery(id+"F0.wireOp",EDGE,"E3.sketch_text.stroke-130"),sQuery(id+"F0.wireOp",EDGE,"E3.sketch_text.stroke-131"),sQuery(id+"F0.wireOp",EDGE,"E3.sketch_text.stroke-132"),sQuery(id+"F0.wireOp",EDGE,"E3.sketch_text.stroke-133"),sQuery(id+"F0.wireOp",EDGE,"E3.sketch_text.stroke-134"),sQuery(id+"F0.wireOp",EDGE,"E3.sketch_text.stroke-135"),sQuery(id+"F0.wireOp",EDGE,"E3.sketch_text.stroke-136"),sQuery(id+"F0.wireOp",EDGE,"E3.sketch_text.stroke-137"),sQuery(id+"F0.wireOp",EDGE,"E3.sketch_text.stroke-138"),sQuery(id+"F0.wireOp",EDGE,"E3.sketch_text.stroke-139"),sQuery(id+"F0.wireOp",EDGE,"E3.sketch_text.stroke-140"),sQuery(id+"F0.wireOp",EDGE,"E3.sketch_text.stroke-141"),sQuery(id+"F0.wireOp",EDGE,"E3.sketch_text.stroke-142"),sQuery(id+"F0.wireOp",EDGE,"E3.sketch_text.stroke-143"),sQuery(id+"F0.wireOp",EDGE,"E3.sketch_text.stroke-144"),sQuery(id+"F0.wireOp",EDGE,"E3.sketch_text.stroke-145"),sQuery(id+"F0.wireOp",EDGE,"E3.sketch_text.stroke-146"),sQuery(id+"F0.wireOp",EDGE,"E3.sketch_text.stroke-147"),sQuery(id+"F0.wireOp",EDGE,"E3.sketch_text.stroke-148"),sQuery(id+"F0.wireOp",EDGE,"E3.sketch_text.stroke-149"),sQuery(id+"F0.wireOp",EDGE,"E3.sketch_text.stroke-150"),sQuery(id+"F0.wireOp",EDGE,"E3.sketch_text.stroke-151")])]});
            var Q7;
            Q7=makeQuery(id+"F1.opExtrude","SWEPT_BODY",BODY,{"disambiguationData":[OSD([sQuery(id+"F0.wireOp",EDGE,"E3.sketch_text.stroke-152"),sQuery(id+"F0.wireOp",EDGE,"E3.sketch_text.stroke-153"),sQuery(id+"F0.wireOp",EDGE,"E3.sketch_text.stroke-154"),sQuery(id+"F0.wireOp",EDGE,"E3.sketch_text.stroke-155")])]});
            var Q8;
            Q8=makeQuery(id+"F5.opExtrude","SWEPT_BODY",BODY,{"disambiguationData":[OSD([sQuery(id+"F4.wireOp",EDGE,"E13.0.0"),sQuery(id+"F4.wireOp",EDGE,"E13.0.1"),sQuery(id+"F4.wireOp",EDGE,"E13.0.2"),sQuery(id+"F4.wireOp",EDGE,"E13.0.3")])]});
            var Q9;
            Q9=makeQuery(id+"F1.opExtrude","SWEPT_BODY",BODY,{"disambiguationData":[OSD([sQuery(id+"F0.wireOp",EDGE,"E3.sketch_text.stroke-11"),sQuery(id+"F0.wireOp",EDGE,"E3.sketch_text.stroke-12"),sQuery(id+"F0.wireOp",EDGE,"E3.sketch_text.stroke-13"),sQuery(id+"F0.wireOp",EDGE,"E3.sketch_text.stroke-14"),sQuery(id+"F0.wireOp",EDGE,"E3.sketch_text.stroke-15"),sQuery(id+"F0.wireOp",EDGE,"E3.sketch_text.stroke-16"),sQuery(id+"F0.wireOp",EDGE,"E3.sketch_text.stroke-17"),sQuery(id+"F0.wireOp",EDGE,"E3.sketch_text.stroke-18"),sQuery(id+"F0.wireOp",EDGE,"E3.sketch_text.stroke-19"),sQuery(id+"F0.wireOp",EDGE,"E3.sketch_text.stroke-20"),sQuery(id+"F0.wireOp",EDGE,"E3.sketch_text.stroke-21"),sQuery(id+"F0.wireOp",EDGE,"E3.sketch_text.stroke-22"),sQuery(id+"F0.wireOp",EDGE,"E3.sketch_text.stroke-23"),sQuery(id+"F0.wireOp",EDGE,"E3.sketch_text.stroke-24")])]});
            var Q10;
            Q10=makeQuery(id+"F1.opExtrude","SWEPT_BODY",BODY,{"disambiguationData":[OSD([sQuery(id+"F0.wireOp",EDGE,"E3.sketch_text.stroke-50"),sQuery(id+"F0.wireOp",EDGE,"E3.sketch_text.stroke-51"),sQuery(id+"F0.wireOp",EDGE,"E3.sketch_text.stroke-52"),sQuery(id+"F0.wireOp",EDGE,"E3.sketch_text.stroke-53"),sQuery(id+"F0.wireOp",EDGE,"E3.sketch_text.stroke-54"),sQuery(id+"F0.wireOp",EDGE,"E3.sketch_text.stroke-55"),sQuery(id+"F0.wireOp",EDGE,"E3.sketch_text.stroke-56"),sQuery(id+"F0.wireOp",EDGE,"E3.sketch_text.stroke-57"),sQuery(id+"F0.wireOp",EDGE,"E3.sketch_text.stroke-58"),sQuery(id+"F0.wireOp",EDGE,"E3.sketch_text.stroke-59"),sQuery(id+"F0.wireOp",EDGE,"E3.sketch_text.stroke-60"),sQuery(id+"F0.wireOp",EDGE,"E3.sketch_text.stroke-61"),sQuery(id+"F0.wireOp",EDGE,"E3.sketch_text.stroke-62"),sQuery(id+"F0.wireOp",EDGE,"E3.sketch_text.stroke-63"),sQuery(id+"F0.wireOp",EDGE,"E3.sketch_text.stroke-64"),sQuery(id+"F0.wireOp",EDGE,"E3.sketch_text.stroke-65"),sQuery(id+"F0.wireOp",EDGE,"E3.sketch_text.stroke-66"),sQuery(id+"F0.wireOp",EDGE,"E3.sketch_text.stroke-67"),sQuery(id+"F0.wireOp",EDGE,"E3.sketch_text.stroke-68")])]});
            var Q11;
            Q11=makeQuery(id+"F1.opExtrude","SWEPT_BODY",BODY,{"disambiguationData":[OSD([sQuery(id+"F0.wireOp",EDGE,"E3.sketch_text.stroke-37"),sQuery(id+"F0.wireOp",EDGE,"E3.sketch_text.stroke-38"),sQuery(id+"F0.wireOp",EDGE,"E3.sketch_text.stroke-39"),sQuery(id+"F0.wireOp",EDGE,"E3.sketch_text.stroke-40"),sQuery(id+"F0.wireOp",EDGE,"E3.sketch_text.stroke-41"),sQuery(id+"F0.wireOp",EDGE,"E3.sketch_text.stroke-42"),sQuery(id+"F0.wireOp",EDGE,"E3.sketch_text.stroke-43"),sQuery(id+"F0.wireOp",EDGE,"E3.sketch_text.stroke-44"),sQuery(id+"F0.wireOp",EDGE,"E3.sketch_text.stroke-45"),sQuery(id+"F0.wireOp",EDGE,"E3.sketch_text.stroke-46"),sQuery(id+"F0.wireOp",EDGE,"E3.sketch_text.stroke-47"),sQuery(id+"F0.wireOp",EDGE,"E3.sketch_text.stroke-48"),sQuery(id+"F0.wireOp",EDGE,"E3.sketch_text.stroke-49")])]});
            var Q12;
            Q12=makeQuery(id+"F1.opExtrude","SWEPT_BODY",BODY,{"disambiguationData":[OSD([sQuery(id+"F0.wireOp",EDGE,"E3.sketch_text.stroke-69"),sQuery(id+"F0.wireOp",EDGE,"E3.sketch_text.stroke-70"),sQuery(id+"F0.wireOp",EDGE,"E3.sketch_text.stroke-71"),sQuery(id+"F0.wireOp",EDGE,"E3.sketch_text.stroke-72"),sQuery(id+"F0.wireOp",EDGE,"E3.sketch_text.stroke-73"),sQuery(id+"F0.wireOp",EDGE,"E3.sketch_text.stroke-74"),sQuery(id+"F0.wireOp",EDGE,"E3.sketch_text.stroke-75"),sQuery(id+"F0.wireOp",EDGE,"E3.sketch_text.stroke-76"),sQuery(id+"F0.wireOp",EDGE,"E3.sketch_text.stroke-77"),sQuery(id+"F0.wireOp",EDGE,"E3.sketch_text.stroke-78"),sQuery(id+"F0.wireOp",EDGE,"E3.sketch_text.stroke-79"),sQuery(id+"F0.wireOp",EDGE,"E3.sketch_text.stroke-80"),sQuery(id+"F0.wireOp",EDGE,"E3.sketch_text.stroke-81"),sQuery(id+"F0.wireOp",EDGE,"E3.sketch_text.stroke-82"),sQuery(id+"F0.wireOp",EDGE,"E3.sketch_text.stroke-83"),sQuery(id+"F0.wireOp",EDGE,"E3.sketch_text.stroke-84"),sQuery(id+"F0.wireOp",EDGE,"E3.sketch_text.stroke-85"),sQuery(id+"F0.wireOp",EDGE,"E3.sketch_text.stroke-86"),sQuery(id+"F0.wireOp",EDGE,"E3.sketch_text.stroke-87"),sQuery(id+"F0.wireOp",EDGE,"E3.sketch_text.stroke-88"),sQuery(id+"F0.wireOp",EDGE,"E3.sketch_text.stroke-89"),sQuery(id+"F0.wireOp",EDGE,"E3.sketch_text.stroke-90"),sQuery(id+"F0.wireOp",EDGE,"E3.sketch_text.stroke-91"),sQuery(id+"F0.wireOp",EDGE,"E3.sketch_text.stroke-92"),sQuery(id+"F0.wireOp",EDGE,"E3.sketch_text.stroke-93"),sQuery(id+"F0.wireOp",EDGE,"E3.sketch_text.stroke-94"),sQuery(id+"F0.wireOp",EDGE,"E3.sketch_text.stroke-95"),sQuery(id+"F0.wireOp",EDGE,"E3.sketch_text.stroke-96"),sQuery(id+"F0.wireOp",EDGE,"E3.sketch_text.stroke-97"),sQuery(id+"F0.wireOp",EDGE,"E3.sketch_text.stroke-98"),sQuery(id+"F0.wireOp",EDGE,"E3.sketch_text.stroke-99"),sQuery(id+"F0.wireOp",EDGE,"E3.sketch_text.stroke-100"),sQuery(id+"F0.wireOp",EDGE,"E3.sketch_text.stroke-101"),sQuery(id+"F0.wireOp",EDGE,"E3.sketch_text.stroke-102"),sQuery(id+"F0.wireOp",EDGE,"E3.sketch_text.stroke-103"),sQuery(id+"F0.wireOp",EDGE,"E3.sketch_text.stroke-104")])]});
            var Q13;
            Q13=makeQuery(id+"F1.opExtrude","SWEPT_BODY",BODY,{"disambiguationData":[OSD([sQuery(id+"F0.wireOp",EDGE,"E3.sketch_text.stroke-110"),sQuery(id+"F0.wireOp",EDGE,"E3.sketch_text.stroke-111"),sQuery(id+"F0.wireOp",EDGE,"E3.sketch_text.stroke-112"),sQuery(id+"F0.wireOp",EDGE,"E3.sketch_text.stroke-113"),sQuery(id+"F0.wireOp",EDGE,"E3.sketch_text.stroke-114")])]});
            var Q14;
            Q14=makeQuery(id+"F1.opExtrude","SWEPT_BODY",BODY,{"disambiguationData":[OSD([sQuery(id+"F0.wireOp",EDGE,"E3.sketch_text.stroke-0"),sQuery(id+"F0.wireOp",EDGE,"E3.sketch_text.stroke-1"),sQuery(id+"F0.wireOp",EDGE,"E3.sketch_text.stroke-2"),sQuery(id+"F0.wireOp",EDGE,"E3.sketch_text.stroke-3"),sQuery(id+"F0.wireOp",EDGE,"E3.sketch_text.stroke-4"),sQuery(id+"F0.wireOp",EDGE,"E3.sketch_text.stroke-5"),sQuery(id+"F0.wireOp",EDGE,"E3.sketch_text.stroke-6"),sQuery(id+"F0.wireOp",EDGE,"E3.sketch_text.stroke-7"),sQuery(id+"F0.wireOp",EDGE,"E3.sketch_text.stroke-8"),sQuery(id+"F0.wireOp",EDGE,"E3.sketch_text.stroke-9"),sQuery(id+"F0.wireOp",EDGE,"E3.sketch_text.stroke-10")])]});
            var Q15;
            Q15=makeQuery(id+"F1.opExtrude","SWEPT_BODY",BODY,{"disambiguationData":[OSD([sQuery(id+"F0.wireOp",EDGE,"E3.sketch_text.stroke-25"),sQuery(id+"F0.wireOp",EDGE,"E3.sketch_text.stroke-26"),sQuery(id+"F0.wireOp",EDGE,"E3.sketch_text.stroke-27"),sQuery(id+"F0.wireOp",EDGE,"E3.sketch_text.stroke-28"),sQuery(id+"F0.wireOp",EDGE,"E3.sketch_text.stroke-29"),sQuery(id+"F0.wireOp",EDGE,"E3.sketch_text.stroke-30"),sQuery(id+"F0.wireOp",EDGE,"E3.sketch_text.stroke-31"),sQuery(id+"F0.wireOp",EDGE,"E3.sketch_text.stroke-32"),sQuery(id+"F0.wireOp",EDGE,"E3.sketch_text.stroke-33"),sQuery(id+"F0.wireOp",EDGE,"E3.sketch_text.stroke-34"),sQuery(id+"F0.wireOp",EDGE,"E3.sketch_text.stroke-35"),sQuery(id+"F0.wireOp",EDGE,"E3.sketch_text.stroke-36")])]});
            booleanBodies(context, id + "F10", {"operationType" : BooleanOperationType.UNION, "tools" : qUnion([Q0, Q1, Q2, Q3, Q4, Q5, Q6, Q7, Q8, Q9, Q10, Q11, Q12, Q13, Q14, Q15])});
        }
        {
            var Q0;
            Q0=makeQuery(id+"F1.opExtrude","SWEPT_BODY",BODY,{"disambiguationData":[OSD([sQuery(id+"F0.wireOp",EDGE,"E4.sketch_text.stroke-11"),sQuery(id+"F0.wireOp",EDGE,"E4.sketch_text.stroke-12"),sQuery(id+"F0.wireOp",EDGE,"E4.sketch_text.stroke-13"),sQuery(id+"F0.wireOp",EDGE,"E4.sketch_text.stroke-14"),sQuery(id+"F0.wireOp",EDGE,"E4.sketch_text.stroke-15"),sQuery(id+"F0.wireOp",EDGE,"E4.sketch_text.stroke-16"),sQuery(id+"F0.wireOp",EDGE,"E4.sketch_text.stroke-17"),sQuery(id+"F0.wireOp",EDGE,"E4.sketch_text.stroke-18"),sQuery(id+"F0.wireOp",EDGE,"E4.sketch_text.stroke-19"),sQuery(id+"F0.wireOp",EDGE,"E4.sketch_text.stroke-20"),sQuery(id+"F0.wireOp",EDGE,"E4.sketch_text.stroke-21"),sQuery(id+"F0.wireOp",EDGE,"E4.sketch_text.stroke-22"),sQuery(id+"F0.wireOp",EDGE,"E4.sketch_text.stroke-23"),sQuery(id+"F0.wireOp",EDGE,"E4.sketch_text.stroke-24"),sQuery(id+"F0.wireOp",EDGE,"E4.sketch_text.stroke-25"),sQuery(id+"F0.wireOp",EDGE,"E4.sketch_text.stroke-26"),sQuery(id+"F0.wireOp",EDGE,"E4.sketch_text.stroke-27"),sQuery(id+"F0.wireOp",EDGE,"E4.sketch_text.stroke-28")])]});
            var Q1;
            Q1=makeQuery(id+"F1.opExtrude","SWEPT_BODY",BODY,{"disambiguationData":[OSD([sQuery(id+"F0.wireOp",EDGE,"E4.sketch_text.stroke-33"),sQuery(id+"F0.wireOp",EDGE,"E4.sketch_text.stroke-34"),sQuery(id+"F0.wireOp",EDGE,"E4.sketch_text.stroke-35"),sQuery(id+"F0.wireOp",EDGE,"E4.sketch_text.stroke-36"),sQuery(id+"F0.wireOp",EDGE,"E4.sketch_text.stroke-37"),sQuery(id+"F0.wireOp",EDGE,"E4.sketch_text.stroke-38"),sQuery(id+"F0.wireOp",EDGE,"E4.sketch_text.stroke-39"),sQuery(id+"F0.wireOp",EDGE,"E4.sketch_text.stroke-40"),sQuery(id+"F0.wireOp",EDGE,"E4.sketch_text.stroke-41"),sQuery(id+"F0.wireOp",EDGE,"E4.sketch_text.stroke-42"),sQuery(id+"F0.wireOp",EDGE,"E4.sketch_text.stroke-43"),sQuery(id+"F0.wireOp",EDGE,"E4.sketch_text.stroke-44"),sQuery(id+"F0.wireOp",EDGE,"E4.sketch_text.stroke-45"),sQuery(id+"F0.wireOp",EDGE,"E4.sketch_text.stroke-46"),sQuery(id+"F0.wireOp",EDGE,"E4.sketch_text.stroke-47"),sQuery(id+"F0.wireOp",EDGE,"E4.sketch_text.stroke-48"),sQuery(id+"F0.wireOp",EDGE,"E4.sketch_text.stroke-49"),sQuery(id+"F0.wireOp",EDGE,"E4.sketch_text.stroke-50"),sQuery(id+"F0.wireOp",EDGE,"E4.sketch_text.stroke-51")])]});
            var Q2;
            Q2=makeQuery(id+"F1.opExtrude","SWEPT_BODY",BODY,{"disambiguationData":[OSD([sQuery(id+"F0.wireOp",EDGE,"E4.sketch_text.stroke-71"),sQuery(id+"F0.wireOp",EDGE,"E4.sketch_text.stroke-72"),sQuery(id+"F0.wireOp",EDGE,"E4.sketch_text.stroke-73"),sQuery(id+"F0.wireOp",EDGE,"E4.sketch_text.stroke-74"),sQuery(id+"F0.wireOp",EDGE,"E4.sketch_text.stroke-75"),sQuery(id+"F0.wireOp",EDGE,"E4.sketch_text.stroke-76"),sQuery(id+"F0.wireOp",EDGE,"E4.sketch_text.stroke-77"),sQuery(id+"F0.wireOp",EDGE,"E4.sketch_text.stroke-78"),sQuery(id+"F0.wireOp",EDGE,"E4.sketch_text.stroke-79"),sQuery(id+"F0.wireOp",EDGE,"E4.sketch_text.stroke-80"),sQuery(id+"F0.wireOp",EDGE,"E4.sketch_text.stroke-81"),sQuery(id+"F0.wireOp",EDGE,"E4.sketch_text.stroke-82"),sQuery(id+"F0.wireOp",EDGE,"E4.sketch_text.stroke-83"),sQuery(id+"F0.wireOp",EDGE,"E4.sketch_text.stroke-84"),sQuery(id+"F0.wireOp",EDGE,"E4.sketch_text.stroke-85"),sQuery(id+"F0.wireOp",EDGE,"E4.sketch_text.stroke-86"),sQuery(id+"F0.wireOp",EDGE,"E4.sketch_text.stroke-87"),sQuery(id+"F0.wireOp",EDGE,"E4.sketch_text.stroke-88"),sQuery(id+"F0.wireOp",EDGE,"E4.sketch_text.stroke-89"),sQuery(id+"F0.wireOp",EDGE,"E4.sketch_text.stroke-90"),sQuery(id+"F0.wireOp",EDGE,"E4.sketch_text.stroke-91"),sQuery(id+"F0.wireOp",EDGE,"E4.sketch_text.stroke-92"),sQuery(id+"F0.wireOp",EDGE,"E4.sketch_text.stroke-93"),sQuery(id+"F0.wireOp",EDGE,"E4.sketch_text.stroke-94"),sQuery(id+"F0.wireOp",EDGE,"E4.sketch_text.stroke-95"),sQuery(id+"F0.wireOp",EDGE,"E4.sketch_text.stroke-96"),sQuery(id+"F0.wireOp",EDGE,"E4.sketch_text.stroke-97"),sQuery(id+"F0.wireOp",EDGE,"E4.sketch_text.stroke-98"),sQuery(id+"F0.wireOp",EDGE,"E4.sketch_text.stroke-99"),sQuery(id+"F0.wireOp",EDGE,"E4.sketch_text.stroke-100"),sQuery(id+"F0.wireOp",EDGE,"E4.sketch_text.stroke-101"),sQuery(id+"F0.wireOp",EDGE,"E4.sketch_text.stroke-102"),sQuery(id+"F0.wireOp",EDGE,"E4.sketch_text.stroke-103"),sQuery(id+"F0.wireOp",EDGE,"E4.sketch_text.stroke-104"),sQuery(id+"F0.wireOp",EDGE,"E4.sketch_text.stroke-105"),sQuery(id+"F0.wireOp",EDGE,"E4.sketch_text.stroke-106")])]});
            var Q3;
            Q3=makeQuery(id+"F1.opExtrude","SWEPT_BODY",BODY,{"disambiguationData":[OSD([sQuery(id+"F0.wireOp",EDGE,"E4.sketch_text.stroke-111"),sQuery(id+"F0.wireOp",EDGE,"E4.sketch_text.stroke-112"),sQuery(id+"F0.wireOp",EDGE,"E4.sketch_text.stroke-113"),sQuery(id+"F0.wireOp",EDGE,"E4.sketch_text.stroke-114"),sQuery(id+"F0.wireOp",EDGE,"E4.sketch_text.stroke-115"),sQuery(id+"F0.wireOp",EDGE,"E4.sketch_text.stroke-116"),sQuery(id+"F0.wireOp",EDGE,"E4.sketch_text.stroke-117"),sQuery(id+"F0.wireOp",EDGE,"E4.sketch_text.stroke-118")])]});
            var Q4;
            Q4=makeQuery(id+"F1.opExtrude","SWEPT_BODY",BODY,{"disambiguationData":[OSD([sQuery(id+"F0.wireOp",EDGE,"E4.sketch_text.stroke-144"),sQuery(id+"F0.wireOp",EDGE,"E4.sketch_text.stroke-145"),sQuery(id+"F0.wireOp",EDGE,"E4.sketch_text.stroke-146"),sQuery(id+"F0.wireOp",EDGE,"E4.sketch_text.stroke-147"),sQuery(id+"F0.wireOp",EDGE,"E4.sketch_text.stroke-148"),sQuery(id+"F0.wireOp",EDGE,"E4.sketch_text.stroke-149"),sQuery(id+"F0.wireOp",EDGE,"E4.sketch_text.stroke-150")])]});
            var Q5;
            Q5=makeQuery(id+"F1.opExtrude","SWEPT_BODY",BODY,{"disambiguationData":[OSD([sQuery(id+"F0.wireOp",EDGE,"E4.sketch_text.stroke-158"),sQuery(id+"F0.wireOp",EDGE,"E4.sketch_text.stroke-159"),sQuery(id+"F0.wireOp",EDGE,"E4.sketch_text.stroke-160"),sQuery(id+"F0.wireOp",EDGE,"E4.sketch_text.stroke-161"),sQuery(id+"F0.wireOp",EDGE,"E4.sketch_text.stroke-162"),sQuery(id+"F0.wireOp",EDGE,"E4.sketch_text.stroke-163"),sQuery(id+"F0.wireOp",EDGE,"E4.sketch_text.stroke-164"),sQuery(id+"F0.wireOp",EDGE,"E4.sketch_text.stroke-165"),sQuery(id+"F0.wireOp",EDGE,"E4.sketch_text.stroke-166"),sQuery(id+"F0.wireOp",EDGE,"E4.sketch_text.stroke-167"),sQuery(id+"F0.wireOp",EDGE,"E4.sketch_text.stroke-168"),sQuery(id+"F0.wireOp",EDGE,"E4.sketch_text.stroke-169"),sQuery(id+"F0.wireOp",EDGE,"E4.sketch_text.stroke-170"),sQuery(id+"F0.wireOp",EDGE,"E4.sketch_text.stroke-171"),sQuery(id+"F0.wireOp",EDGE,"E4.sketch_text.stroke-172"),sQuery(id+"F0.wireOp",EDGE,"E4.sketch_text.stroke-173"),sQuery(id+"F0.wireOp",EDGE,"E4.sketch_text.stroke-174"),sQuery(id+"F0.wireOp",EDGE,"E4.sketch_text.stroke-175"),sQuery(id+"F0.wireOp",EDGE,"E4.sketch_text.stroke-176")])]});
            var Q6;
            Q6=makeQuery(id+"F1.opExtrude","SWEPT_BODY",BODY,{"disambiguationData":[OSD([sQuery(id+"F0.wireOp",EDGE,"E4.sketch_text.stroke-177"),sQuery(id+"F0.wireOp",EDGE,"E4.sketch_text.stroke-178"),sQuery(id+"F0.wireOp",EDGE,"E4.sketch_text.stroke-179"),sQuery(id+"F0.wireOp",EDGE,"E4.sketch_text.stroke-180"),sQuery(id+"F0.wireOp",EDGE,"E4.sketch_text.stroke-181"),sQuery(id+"F0.wireOp",EDGE,"E4.sketch_text.stroke-182"),sQuery(id+"F0.wireOp",EDGE,"E4.sketch_text.stroke-183"),sQuery(id+"F0.wireOp",EDGE,"E4.sketch_text.stroke-184"),sQuery(id+"F0.wireOp",EDGE,"E4.sketch_text.stroke-185"),sQuery(id+"F0.wireOp",EDGE,"E4.sketch_text.stroke-186"),sQuery(id+"F0.wireOp",EDGE,"E4.sketch_text.stroke-187"),sQuery(id+"F0.wireOp",EDGE,"E4.sketch_text.stroke-188"),sQuery(id+"F0.wireOp",EDGE,"E4.sketch_text.stroke-189"),sQuery(id+"F0.wireOp",EDGE,"E4.sketch_text.stroke-190"),sQuery(id+"F0.wireOp",EDGE,"E4.sketch_text.stroke-191"),sQuery(id+"F0.wireOp",EDGE,"E4.sketch_text.stroke-192"),sQuery(id+"F0.wireOp",EDGE,"E4.sketch_text.stroke-193"),sQuery(id+"F0.wireOp",EDGE,"E4.sketch_text.stroke-194"),sQuery(id+"F0.wireOp",EDGE,"E4.sketch_text.stroke-195"),sQuery(id+"F0.wireOp",EDGE,"E4.sketch_text.stroke-196"),sQuery(id+"F0.wireOp",EDGE,"E4.sketch_text.stroke-197"),sQuery(id+"F0.wireOp",EDGE,"E4.sketch_text.stroke-198"),sQuery(id+"F0.wireOp",EDGE,"E4.sketch_text.stroke-199"),sQuery(id+"F0.wireOp",EDGE,"E4.sketch_text.stroke-200"),sQuery(id+"F0.wireOp",EDGE,"E4.sketch_text.stroke-201"),sQuery(id+"F0.wireOp",EDGE,"E4.sketch_text.stroke-202"),sQuery(id+"F0.wireOp",EDGE,"E4.sketch_text.stroke-203"),sQuery(id+"F0.wireOp",EDGE,"E4.sketch_text.stroke-204"),sQuery(id+"F0.wireOp",EDGE,"E4.sketch_text.stroke-205"),sQuery(id+"F0.wireOp",EDGE,"E4.sketch_text.stroke-206"),sQuery(id+"F0.wireOp",EDGE,"E4.sketch_text.stroke-207"),sQuery(id+"F0.wireOp",EDGE,"E4.sketch_text.stroke-208"),sQuery(id+"F0.wireOp",EDGE,"E4.sketch_text.stroke-209"),sQuery(id+"F0.wireOp",EDGE,"E4.sketch_text.stroke-210"),sQuery(id+"F0.wireOp",EDGE,"E4.sketch_text.stroke-211"),sQuery(id+"F0.wireOp",EDGE,"E4.sketch_text.stroke-212")])]});
            var Q7;
            Q7=makeQuery(id+"F1.opExtrude","SWEPT_BODY",BODY,{"disambiguationData":[OSD([sQuery(id+"F0.wireOp",EDGE,"E4.sketch_text.stroke-5"),sQuery(id+"F0.wireOp",EDGE,"E4.sketch_text.stroke-6"),sQuery(id+"F0.wireOp",EDGE,"E4.sketch_text.stroke-7"),sQuery(id+"F0.wireOp",EDGE,"E4.sketch_text.stroke-8"),sQuery(id+"F0.wireOp",EDGE,"E4.sketch_text.stroke-9"),sQuery(id+"F0.wireOp",EDGE,"E4.sketch_text.stroke-10")])]});
            var Q8;
            Q8=makeQuery(id+"F1.opExtrude","SWEPT_BODY",BODY,{"disambiguationData":[OSD([sQuery(id+"F0.wireOp",EDGE,"E4.sketch_text.stroke-119"),sQuery(id+"F0.wireOp",EDGE,"E4.sketch_text.stroke-120"),sQuery(id+"F0.wireOp",EDGE,"E4.sketch_text.stroke-121"),sQuery(id+"F0.wireOp",EDGE,"E4.sketch_text.stroke-122"),sQuery(id+"F0.wireOp",EDGE,"E4.sketch_text.stroke-123"),sQuery(id+"F0.wireOp",EDGE,"E4.sketch_text.stroke-124"),sQuery(id+"F0.wireOp",EDGE,"E4.sketch_text.stroke-125"),sQuery(id+"F0.wireOp",EDGE,"E4.sketch_text.stroke-126"),sQuery(id+"F0.wireOp",EDGE,"E4.sketch_text.stroke-127"),sQuery(id+"F0.wireOp",EDGE,"E4.sketch_text.stroke-128"),sQuery(id+"F0.wireOp",EDGE,"E4.sketch_text.stroke-129"),sQuery(id+"F0.wireOp",EDGE,"E4.sketch_text.stroke-130"),sQuery(id+"F0.wireOp",EDGE,"E4.sketch_text.stroke-131"),sQuery(id+"F0.wireOp",EDGE,"E4.sketch_text.stroke-132"),sQuery(id+"F0.wireOp",EDGE,"E4.sketch_text.stroke-133"),sQuery(id+"F0.wireOp",EDGE,"E4.sketch_text.stroke-134"),sQuery(id+"F0.wireOp",EDGE,"E4.sketch_text.stroke-135"),sQuery(id+"F0.wireOp",EDGE,"E4.sketch_text.stroke-136"),sQuery(id+"F0.wireOp",EDGE,"E4.sketch_text.stroke-137"),sQuery(id+"F0.wireOp",EDGE,"E4.sketch_text.stroke-138"),sQuery(id+"F0.wireOp",EDGE,"E4.sketch_text.stroke-139"),sQuery(id+"F0.wireOp",EDGE,"E4.sketch_text.stroke-140"),sQuery(id+"F0.wireOp",EDGE,"E4.sketch_text.stroke-141"),sQuery(id+"F0.wireOp",EDGE,"E4.sketch_text.stroke-142"),sQuery(id+"F0.wireOp",EDGE,"E4.sketch_text.stroke-143")])]});
            var Q9;
            Q9=makeQuery(id+"F1.opExtrude","SWEPT_BODY",BODY,{"disambiguationData":[OSD([sQuery(id+"F0.wireOp",EDGE,"E4.sketch_text.stroke-151"),sQuery(id+"F0.wireOp",EDGE,"E4.sketch_text.stroke-152"),sQuery(id+"F0.wireOp",EDGE,"E4.sketch_text.stroke-153"),sQuery(id+"F0.wireOp",EDGE,"E4.sketch_text.stroke-154"),sQuery(id+"F0.wireOp",EDGE,"E4.sketch_text.stroke-155"),sQuery(id+"F0.wireOp",EDGE,"E4.sketch_text.stroke-156"),sQuery(id+"F0.wireOp",EDGE,"E4.sketch_text.stroke-157")])]});
            var Q10;
            Q10=makeQuery(id+"F1.opExtrude","SWEPT_BODY",BODY,{"disambiguationData":[OSD([sQuery(id+"F0.wireOp",EDGE,"E4.sketch_text.stroke-107"),sQuery(id+"F0.wireOp",EDGE,"E4.sketch_text.stroke-108"),sQuery(id+"F0.wireOp",EDGE,"E4.sketch_text.stroke-109"),sQuery(id+"F0.wireOp",EDGE,"E4.sketch_text.stroke-110")])]});
            var Q11;
            Q11=makeQuery(id+"F1.opExtrude","SWEPT_BODY",BODY,{"disambiguationData":[OSD([sQuery(id+"F0.wireOp",EDGE,"E4.sketch_text.stroke-52"),sQuery(id+"F0.wireOp",EDGE,"E4.sketch_text.stroke-53"),sQuery(id+"F0.wireOp",EDGE,"E4.sketch_text.stroke-54"),sQuery(id+"F0.wireOp",EDGE,"E4.sketch_text.stroke-55"),sQuery(id+"F0.wireOp",EDGE,"E4.sketch_text.stroke-56"),sQuery(id+"F0.wireOp",EDGE,"E4.sketch_text.stroke-57"),sQuery(id+"F0.wireOp",EDGE,"E4.sketch_text.stroke-58"),sQuery(id+"F0.wireOp",EDGE,"E4.sketch_text.stroke-59"),sQuery(id+"F0.wireOp",EDGE,"E4.sketch_text.stroke-60"),sQuery(id+"F0.wireOp",EDGE,"E4.sketch_text.stroke-61"),sQuery(id+"F0.wireOp",EDGE,"E4.sketch_text.stroke-62"),sQuery(id+"F0.wireOp",EDGE,"E4.sketch_text.stroke-63"),sQuery(id+"F0.wireOp",EDGE,"E4.sketch_text.stroke-64"),sQuery(id+"F0.wireOp",EDGE,"E4.sketch_text.stroke-65"),sQuery(id+"F0.wireOp",EDGE,"E4.sketch_text.stroke-66"),sQuery(id+"F0.wireOp",EDGE,"E4.sketch_text.stroke-67"),sQuery(id+"F0.wireOp",EDGE,"E4.sketch_text.stroke-68"),sQuery(id+"F0.wireOp",EDGE,"E4.sketch_text.stroke-69"),sQuery(id+"F0.wireOp",EDGE,"E4.sketch_text.stroke-70")])]});
            var Q12;
            Q12=makeQuery(id+"F1.opExtrude","SWEPT_BODY",BODY,{"disambiguationData":[OSD([sQuery(id+"F0.wireOp",EDGE,"E4.sketch_text.stroke-0"),sQuery(id+"F0.wireOp",EDGE,"E4.sketch_text.stroke-1"),sQuery(id+"F0.wireOp",EDGE,"E4.sketch_text.stroke-2"),sQuery(id+"F0.wireOp",EDGE,"E4.sketch_text.stroke-3"),sQuery(id+"F0.wireOp",EDGE,"E4.sketch_text.stroke-4")])]});
            var Q13;
            Q13=makeQuery(id+"F5.opExtrude","SWEPT_BODY",BODY,{"disambiguationData":[OSD([sQuery(id+"F4.wireOp",EDGE,"E14.0.0"),sQuery(id+"F4.wireOp",EDGE,"E14.0.1"),sQuery(id+"F4.wireOp",EDGE,"E14.0.2"),sQuery(id+"F4.wireOp",EDGE,"E14.0.3")])]});
            var Q14;
            Q14=makeQuery(id+"F1.opExtrude","SWEPT_BODY",BODY,{"disambiguationData":[OSD([sQuery(id+"F0.wireOp",EDGE,"E4.sketch_text.stroke-29"),sQuery(id+"F0.wireOp",EDGE,"E4.sketch_text.stroke-30"),sQuery(id+"F0.wireOp",EDGE,"E4.sketch_text.stroke-31"),sQuery(id+"F0.wireOp",EDGE,"E4.sketch_text.stroke-32")])]});
            booleanBodies(context, id + "F11", {"operationType" : BooleanOperationType.UNION, "tools" : qUnion([Q0, Q1, Q2, Q3, Q4, Q5, Q6, Q7, Q8, Q9, Q10, Q11, Q12, Q13, Q14])});
        }
        {
            var Q0;
            Q0=makeQuery(id+"F7.opBoolean","INTERSECT",EDGE,{"derivedFrom":[makeQuery(id+"F1.opExtrude","CAP_FACE",FACE,{"disambiguationData":[OSD([sQuery(id+"F0.wireOp",EDGE,"E0.sketch_text.stroke-191"),sQuery(id+"F0.wireOp",EDGE,"E0.sketch_text.stroke-192"),sQuery(id+"F0.wireOp",EDGE,"E0.sketch_text.stroke-193"),sQuery(id+"F0.wireOp",EDGE,"E0.sketch_text.stroke-194")])],"isStart":true}),makeQuery(id+"F5.opExtrude","SWEPT_FACE",FACE,{"disambiguationData":[OSD([sQuery(id+"F4.wireOp",EDGE,"E10.0.0")])]})]});
            var Q1;
            Q1=makeQuery(id+"F7.opBoolean","INTERSECT",EDGE,{"derivedFrom":[makeQuery(id+"F1.opExtrude","CAP_FACE",FACE,{"disambiguationData":[OSD([sQuery(id+"F0.wireOp",EDGE,"E0.sketch_text.stroke-103"),sQuery(id+"F0.wireOp",EDGE,"E0.sketch_text.stroke-104"),sQuery(id+"F0.wireOp",EDGE,"E0.sketch_text.stroke-105"),sQuery(id+"F0.wireOp",EDGE,"E0.sketch_text.stroke-106"),sQuery(id+"F0.wireOp",EDGE,"E0.sketch_text.stroke-107"),sQuery(id+"F0.wireOp",EDGE,"E0.sketch_text.stroke-108"),sQuery(id+"F0.wireOp",EDGE,"E0.sketch_text.stroke-109"),sQuery(id+"F0.wireOp",EDGE,"E0.sketch_text.stroke-110")])],"isStart":true}),makeQuery(id+"F5.opExtrude","SWEPT_FACE",FACE,{"disambiguationData":[OSD([sQuery(id+"F4.wireOp",EDGE,"E10.0.0")])]})]});
            var Q2;
            Q2=makeQuery(id+"F7.opBoolean","INTERSECT",EDGE,{"derivedFrom":[makeQuery(id+"F1.opExtrude","CAP_FACE",FACE,{"disambiguationData":[OSD([sQuery(id+"F0.wireOp",EDGE,"E0.sketch_text.stroke-4"),sQuery(id+"F0.wireOp",EDGE,"E0.sketch_text.stroke-5"),sQuery(id+"F0.wireOp",EDGE,"E0.sketch_text.stroke-6"),sQuery(id+"F0.wireOp",EDGE,"E0.sketch_text.stroke-7"),sQuery(id+"F0.wireOp",EDGE,"E0.sketch_text.stroke-8"),sQuery(id+"F0.wireOp",EDGE,"E0.sketch_text.stroke-9"),sQuery(id+"F0.wireOp",EDGE,"E0.sketch_text.stroke-10"),sQuery(id+"F0.wireOp",EDGE,"E0.sketch_text.stroke-11"),sQuery(id+"F0.wireOp",EDGE,"E0.sketch_text.stroke-12"),sQuery(id+"F0.wireOp",EDGE,"E0.sketch_text.stroke-13"),sQuery(id+"F0.wireOp",EDGE,"E0.sketch_text.stroke-14"),sQuery(id+"F0.wireOp",EDGE,"E0.sketch_text.stroke-15"),sQuery(id+"F0.wireOp",EDGE,"E0.sketch_text.stroke-16"),sQuery(id+"F0.wireOp",EDGE,"E0.sketch_text.stroke-17"),sQuery(id+"F0.wireOp",EDGE,"E0.sketch_text.stroke-18"),sQuery(id+"F0.wireOp",EDGE,"E0.sketch_text.stroke-19"),sQuery(id+"F0.wireOp",EDGE,"E0.sketch_text.stroke-20"),sQuery(id+"F0.wireOp",EDGE,"E0.sketch_text.stroke-21"),sQuery(id+"F0.wireOp",EDGE,"E0.sketch_text.stroke-22"),sQuery(id+"F0.wireOp",EDGE,"E0.sketch_text.stroke-23"),sQuery(id+"F0.wireOp",EDGE,"E0.sketch_text.stroke-24"),sQuery(id+"F0.wireOp",EDGE,"E0.sketch_text.stroke-25"),sQuery(id+"F0.wireOp",EDGE,"E0.sketch_text.stroke-26"),sQuery(id+"F0.wireOp",EDGE,"E0.sketch_text.stroke-27"),sQuery(id+"F0.wireOp",EDGE,"E0.sketch_text.stroke-28"),sQuery(id+"F0.wireOp",EDGE,"E0.sketch_text.stroke-29")])],"isStart":true}),makeQuery(id+"F5.opExtrude","SWEPT_FACE",FACE,{"disambiguationData":[OSD([sQuery(id+"F4.wireOp",EDGE,"E10.0.0")])]})]});
            var Q3;
            Q3=makeQuery(id+"F7.opBoolean","INTERSECT",EDGE,{"derivedFrom":[makeQuery(id+"F1.opExtrude","CAP_FACE",FACE,{"disambiguationData":[OSD([sQuery(id+"F0.wireOp",EDGE,"E0.sketch_text.stroke-0"),sQuery(id+"F0.wireOp",EDGE,"E0.sketch_text.stroke-1"),sQuery(id+"F0.wireOp",EDGE,"E0.sketch_text.stroke-2"),sQuery(id+"F0.wireOp",EDGE,"E0.sketch_text.stroke-3")])],"isStart":true}),makeQuery(id+"F6.opFillet","BLEND_FACE",FACE,{"disambiguationData":[OSD([sQuery(id+"F4.wireOp",EDGE,"E10.0.0"),sQuery(id+"F4.wireOp",EDGE,"E10.0.1")])]})]});
            var Q4;
            Q4=makeQuery(id+"F7.opBoolean","INTERSECT",EDGE,{"derivedFrom":[makeQuery(id+"F1.opExtrude","CAP_FACE",FACE,{"disambiguationData":[OSD([sQuery(id+"F0.wireOp",EDGE,"E0.sketch_text.stroke-0"),sQuery(id+"F0.wireOp",EDGE,"E0.sketch_text.stroke-1"),sQuery(id+"F0.wireOp",EDGE,"E0.sketch_text.stroke-2"),sQuery(id+"F0.wireOp",EDGE,"E0.sketch_text.stroke-3")])],"isStart":true}),makeQuery(id+"F5.opExtrude","SWEPT_FACE",FACE,{"disambiguationData":[OSD([sQuery(id+"F4.wireOp",EDGE,"E10.0.2")])]})]});
            var Q5;
            Q5=makeQuery(id+"F7.opBoolean","INTERSECT",EDGE,{"derivedFrom":[makeQuery(id+"F1.opExtrude","CAP_FACE",FACE,{"disambiguationData":[OSD([sQuery(id+"F0.wireOp",EDGE,"E0.sketch_text.stroke-4"),sQuery(id+"F0.wireOp",EDGE,"E0.sketch_text.stroke-5"),sQuery(id+"F0.wireOp",EDGE,"E0.sketch_text.stroke-6"),sQuery(id+"F0.wireOp",EDGE,"E0.sketch_text.stroke-7"),sQuery(id+"F0.wireOp",EDGE,"E0.sketch_text.stroke-8"),sQuery(id+"F0.wireOp",EDGE,"E0.sketch_text.stroke-9"),sQuery(id+"F0.wireOp",EDGE,"E0.sketch_text.stroke-10"),sQuery(id+"F0.wireOp",EDGE,"E0.sketch_text.stroke-11"),sQuery(id+"F0.wireOp",EDGE,"E0.sketch_text.stroke-12"),sQuery(id+"F0.wireOp",EDGE,"E0.sketch_text.stroke-13"),sQuery(id+"F0.wireOp",EDGE,"E0.sketch_text.stroke-14"),sQuery(id+"F0.wireOp",EDGE,"E0.sketch_text.stroke-15"),sQuery(id+"F0.wireOp",EDGE,"E0.sketch_text.stroke-16"),sQuery(id+"F0.wireOp",EDGE,"E0.sketch_text.stroke-17"),sQuery(id+"F0.wireOp",EDGE,"E0.sketch_text.stroke-18"),sQuery(id+"F0.wireOp",EDGE,"E0.sketch_text.stroke-19"),sQuery(id+"F0.wireOp",EDGE,"E0.sketch_text.stroke-20"),sQuery(id+"F0.wireOp",EDGE,"E0.sketch_text.stroke-21"),sQuery(id+"F0.wireOp",EDGE,"E0.sketch_text.stroke-22"),sQuery(id+"F0.wireOp",EDGE,"E0.sketch_text.stroke-23"),sQuery(id+"F0.wireOp",EDGE,"E0.sketch_text.stroke-24"),sQuery(id+"F0.wireOp",EDGE,"E0.sketch_text.stroke-25"),sQuery(id+"F0.wireOp",EDGE,"E0.sketch_text.stroke-26"),sQuery(id+"F0.wireOp",EDGE,"E0.sketch_text.stroke-27"),sQuery(id+"F0.wireOp",EDGE,"E0.sketch_text.stroke-28"),sQuery(id+"F0.wireOp",EDGE,"E0.sketch_text.stroke-29")])],"isStart":true}),makeQuery(id+"F5.opExtrude","SWEPT_FACE",FACE,{"disambiguationData":[OSD([sQuery(id+"F4.wireOp",EDGE,"E10.0.2")])]})]});
            var Q6;
            Q6=makeQuery(id+"F7.opBoolean","INTERSECT",EDGE,{"derivedFrom":[makeQuery(id+"F1.opExtrude","CAP_FACE",FACE,{"disambiguationData":[OSD([sQuery(id+"F0.wireOp",EDGE,"E0.sketch_text.stroke-30"),sQuery(id+"F0.wireOp",EDGE,"E0.sketch_text.stroke-31"),sQuery(id+"F0.wireOp",EDGE,"E0.sketch_text.stroke-32"),sQuery(id+"F0.wireOp",EDGE,"E0.sketch_text.stroke-33"),sQuery(id+"F0.wireOp",EDGE,"E0.sketch_text.stroke-34"),sQuery(id+"F0.wireOp",EDGE,"E0.sketch_text.stroke-35"),sQuery(id+"F0.wireOp",EDGE,"E0.sketch_text.stroke-36"),sQuery(id+"F0.wireOp",EDGE,"E0.sketch_text.stroke-37"),sQuery(id+"F0.wireOp",EDGE,"E0.sketch_text.stroke-38"),sQuery(id+"F0.wireOp",EDGE,"E0.sketch_text.stroke-39"),sQuery(id+"F0.wireOp",EDGE,"E0.sketch_text.stroke-40"),sQuery(id+"F0.wireOp",EDGE,"E0.sketch_text.stroke-41"),sQuery(id+"F0.wireOp",EDGE,"E0.sketch_text.stroke-42"),sQuery(id+"F0.wireOp",EDGE,"E0.sketch_text.stroke-43"),sQuery(id+"F0.wireOp",EDGE,"E0.sketch_text.stroke-44"),sQuery(id+"F0.wireOp",EDGE,"E0.sketch_text.stroke-45"),sQuery(id+"F0.wireOp",EDGE,"E0.sketch_text.stroke-46"),sQuery(id+"F0.wireOp",EDGE,"E0.sketch_text.stroke-47"),sQuery(id+"F0.wireOp",EDGE,"E0.sketch_text.stroke-48")])],"isStart":true}),makeQuery(id+"F5.opExtrude","SWEPT_FACE",FACE,{"disambiguationData":[OSD([sQuery(id+"F4.wireOp",EDGE,"E10.0.2")])]})]});
            var Q7;
            Q7=makeQuery(id+"F7.opBoolean","INTERSECT",EDGE,{"disambiguationData":[OD(1.0)],"derivedFrom":[makeQuery(id+"F1.opExtrude","CAP_FACE",FACE,{"disambiguationData":[OSD([sQuery(id+"F0.wireOp",EDGE,"E0.sketch_text.stroke-49"),sQuery(id+"F0.wireOp",EDGE,"E0.sketch_text.stroke-50"),sQuery(id+"F0.wireOp",EDGE,"E0.sketch_text.stroke-51"),sQuery(id+"F0.wireOp",EDGE,"E0.sketch_text.stroke-52"),sQuery(id+"F0.wireOp",EDGE,"E0.sketch_text.stroke-53"),sQuery(id+"F0.wireOp",EDGE,"E0.sketch_text.stroke-54"),sQuery(id+"F0.wireOp",EDGE,"E0.sketch_text.stroke-55"),sQuery(id+"F0.wireOp",EDGE,"E0.sketch_text.stroke-56"),sQuery(id+"F0.wireOp",EDGE,"E0.sketch_text.stroke-57"),sQuery(id+"F0.wireOp",EDGE,"E0.sketch_text.stroke-58"),sQuery(id+"F0.wireOp",EDGE,"E0.sketch_text.stroke-59"),sQuery(id+"F0.wireOp",EDGE,"E0.sketch_text.stroke-60"),sQuery(id+"F0.wireOp",EDGE,"E0.sketch_text.stroke-61"),sQuery(id+"F0.wireOp",EDGE,"E0.sketch_text.stroke-62"),sQuery(id+"F0.wireOp",EDGE,"E0.sketch_text.stroke-63"),sQuery(id+"F0.wireOp",EDGE,"E0.sketch_text.stroke-64"),sQuery(id+"F0.wireOp",EDGE,"E0.sketch_text.stroke-65"),sQuery(id+"F0.wireOp",EDGE,"E0.sketch_text.stroke-66"),sQuery(id+"F0.wireOp",EDGE,"E0.sketch_text.stroke-67"),sQuery(id+"F0.wireOp",EDGE,"E0.sketch_text.stroke-68"),sQuery(id+"F0.wireOp",EDGE,"E0.sketch_text.stroke-69"),sQuery(id+"F0.wireOp",EDGE,"E0.sketch_text.stroke-70"),sQuery(id+"F0.wireOp",EDGE,"E0.sketch_text.stroke-71"),sQuery(id+"F0.wireOp",EDGE,"E0.sketch_text.stroke-72"),sQuery(id+"F0.wireOp",EDGE,"E0.sketch_text.stroke-73"),sQuery(id+"F0.wireOp",EDGE,"E0.sketch_text.stroke-74"),sQuery(id+"F0.wireOp",EDGE,"E0.sketch_text.stroke-75"),sQuery(id+"F0.wireOp",EDGE,"E0.sketch_text.stroke-76"),sQuery(id+"F0.wireOp",EDGE,"E0.sketch_text.stroke-77"),sQuery(id+"F0.wireOp",EDGE,"E0.sketch_text.stroke-78"),sQuery(id+"F0.wireOp",EDGE,"E0.sketch_text.stroke-79"),sQuery(id+"F0.wireOp",EDGE,"E0.sketch_text.stroke-80"),sQuery(id+"F0.wireOp",EDGE,"E0.sketch_text.stroke-81"),sQuery(id+"F0.wireOp",EDGE,"E0.sketch_text.stroke-82"),sQuery(id+"F0.wireOp",EDGE,"E0.sketch_text.stroke-83"),sQuery(id+"F0.wireOp",EDGE,"E0.sketch_text.stroke-84")])],"isStart":true}),makeQuery(id+"F5.opExtrude","SWEPT_FACE",FACE,{"disambiguationData":[OSD([sQuery(id+"F4.wireOp",EDGE,"E10.0.2")])]})]});
            var Q8;
            Q8=makeQuery(id+"F7.opBoolean","INTERSECT",EDGE,{"disambiguationData":[OD(0.0)],"derivedFrom":[makeQuery(id+"F1.opExtrude","CAP_FACE",FACE,{"disambiguationData":[OSD([sQuery(id+"F0.wireOp",EDGE,"E0.sketch_text.stroke-49"),sQuery(id+"F0.wireOp",EDGE,"E0.sketch_text.stroke-50"),sQuery(id+"F0.wireOp",EDGE,"E0.sketch_text.stroke-51"),sQuery(id+"F0.wireOp",EDGE,"E0.sketch_text.stroke-52"),sQuery(id+"F0.wireOp",EDGE,"E0.sketch_text.stroke-53"),sQuery(id+"F0.wireOp",EDGE,"E0.sketch_text.stroke-54"),sQuery(id+"F0.wireOp",EDGE,"E0.sketch_text.stroke-55"),sQuery(id+"F0.wireOp",EDGE,"E0.sketch_text.stroke-56"),sQuery(id+"F0.wireOp",EDGE,"E0.sketch_text.stroke-57"),sQuery(id+"F0.wireOp",EDGE,"E0.sketch_text.stroke-58"),sQuery(id+"F0.wireOp",EDGE,"E0.sketch_text.stroke-59"),sQuery(id+"F0.wireOp",EDGE,"E0.sketch_text.stroke-60"),sQuery(id+"F0.wireOp",EDGE,"E0.sketch_text.stroke-61"),sQuery(id+"F0.wireOp",EDGE,"E0.sketch_text.stroke-62"),sQuery(id+"F0.wireOp",EDGE,"E0.sketch_text.stroke-63"),sQuery(id+"F0.wireOp",EDGE,"E0.sketch_text.stroke-64"),sQuery(id+"F0.wireOp",EDGE,"E0.sketch_text.stroke-65"),sQuery(id+"F0.wireOp",EDGE,"E0.sketch_text.stroke-66"),sQuery(id+"F0.wireOp",EDGE,"E0.sketch_text.stroke-67"),sQuery(id+"F0.wireOp",EDGE,"E0.sketch_text.stroke-68"),sQuery(id+"F0.wireOp",EDGE,"E0.sketch_text.stroke-69"),sQuery(id+"F0.wireOp",EDGE,"E0.sketch_text.stroke-70"),sQuery(id+"F0.wireOp",EDGE,"E0.sketch_text.stroke-71"),sQuery(id+"F0.wireOp",EDGE,"E0.sketch_text.stroke-72"),sQuery(id+"F0.wireOp",EDGE,"E0.sketch_text.stroke-73"),sQuery(id+"F0.wireOp",EDGE,"E0.sketch_text.stroke-74"),sQuery(id+"F0.wireOp",EDGE,"E0.sketch_text.stroke-75"),sQuery(id+"F0.wireOp",EDGE,"E0.sketch_text.stroke-76"),sQuery(id+"F0.wireOp",EDGE,"E0.sketch_text.stroke-77"),sQuery(id+"F0.wireOp",EDGE,"E0.sketch_text.stroke-78"),sQuery(id+"F0.wireOp",EDGE,"E0.sketch_text.stroke-79"),sQuery(id+"F0.wireOp",EDGE,"E0.sketch_text.stroke-80"),sQuery(id+"F0.wireOp",EDGE,"E0.sketch_text.stroke-81"),sQuery(id+"F0.wireOp",EDGE,"E0.sketch_text.stroke-82"),sQuery(id+"F0.wireOp",EDGE,"E0.sketch_text.stroke-83"),sQuery(id+"F0.wireOp",EDGE,"E0.sketch_text.stroke-84")])],"isStart":true}),makeQuery(id+"F5.opExtrude","SWEPT_FACE",FACE,{"disambiguationData":[OSD([sQuery(id+"F4.wireOp",EDGE,"E10.0.2")])]})]});
            var Q9;
            Q9=makeQuery(id+"F7.opBoolean","INTERSECT",EDGE,{"derivedFrom":[makeQuery(id+"F1.opExtrude","CAP_FACE",FACE,{"disambiguationData":[OSD([sQuery(id+"F0.wireOp",EDGE,"E0.sketch_text.stroke-85"),sQuery(id+"F0.wireOp",EDGE,"E0.sketch_text.stroke-86"),sQuery(id+"F0.wireOp",EDGE,"E0.sketch_text.stroke-87"),sQuery(id+"F0.wireOp",EDGE,"E0.sketch_text.stroke-88"),sQuery(id+"F0.wireOp",EDGE,"E0.sketch_text.stroke-89"),sQuery(id+"F0.wireOp",EDGE,"E0.sketch_text.stroke-90"),sQuery(id+"F0.wireOp",EDGE,"E0.sketch_text.stroke-91"),sQuery(id+"F0.wireOp",EDGE,"E0.sketch_text.stroke-92"),sQuery(id+"F0.wireOp",EDGE,"E0.sketch_text.stroke-93"),sQuery(id+"F0.wireOp",EDGE,"E0.sketch_text.stroke-94"),sQuery(id+"F0.wireOp",EDGE,"E0.sketch_text.stroke-95"),sQuery(id+"F0.wireOp",EDGE,"E0.sketch_text.stroke-96"),sQuery(id+"F0.wireOp",EDGE,"E0.sketch_text.stroke-97"),sQuery(id+"F0.wireOp",EDGE,"E0.sketch_text.stroke-98"),sQuery(id+"F0.wireOp",EDGE,"E0.sketch_text.stroke-99"),sQuery(id+"F0.wireOp",EDGE,"E0.sketch_text.stroke-100"),sQuery(id+"F0.wireOp",EDGE,"E0.sketch_text.stroke-101"),sQuery(id+"F0.wireOp",EDGE,"E0.sketch_text.stroke-102")])],"isStart":true}),makeQuery(id+"F5.opExtrude","SWEPT_FACE",FACE,{"disambiguationData":[OSD([sQuery(id+"F4.wireOp",EDGE,"E10.0.2")])]})]});
            var Q10;
            Q10=makeQuery(id+"F7.opBoolean","INTERSECT",EDGE,{"derivedFrom":[makeQuery(id+"F1.opExtrude","CAP_FACE",FACE,{"disambiguationData":[OSD([sQuery(id+"F0.wireOp",EDGE,"E0.sketch_text.stroke-124"),sQuery(id+"F0.wireOp",EDGE,"E0.sketch_text.stroke-125"),sQuery(id+"F0.wireOp",EDGE,"E0.sketch_text.stroke-126"),sQuery(id+"F0.wireOp",EDGE,"E0.sketch_text.stroke-127"),sQuery(id+"F0.wireOp",EDGE,"E0.sketch_text.stroke-128"),sQuery(id+"F0.wireOp",EDGE,"E0.sketch_text.stroke-129"),sQuery(id+"F0.wireOp",EDGE,"E0.sketch_text.stroke-130"),sQuery(id+"F0.wireOp",EDGE,"E0.sketch_text.stroke-131"),sQuery(id+"F0.wireOp",EDGE,"E0.sketch_text.stroke-132"),sQuery(id+"F0.wireOp",EDGE,"E0.sketch_text.stroke-133"),sQuery(id+"F0.wireOp",EDGE,"E0.sketch_text.stroke-134"),sQuery(id+"F0.wireOp",EDGE,"E0.sketch_text.stroke-135"),sQuery(id+"F0.wireOp",EDGE,"E0.sketch_text.stroke-136"),sQuery(id+"F0.wireOp",EDGE,"E0.sketch_text.stroke-137"),sQuery(id+"F0.wireOp",EDGE,"E0.sketch_text.stroke-138"),sQuery(id+"F0.wireOp",EDGE,"E0.sketch_text.stroke-139"),sQuery(id+"F0.wireOp",EDGE,"E0.sketch_text.stroke-140"),sQuery(id+"F0.wireOp",EDGE,"E0.sketch_text.stroke-141"),sQuery(id+"F0.wireOp",EDGE,"E0.sketch_text.stroke-142"),sQuery(id+"F0.wireOp",EDGE,"E0.sketch_text.stroke-143"),sQuery(id+"F0.wireOp",EDGE,"E0.sketch_text.stroke-144"),sQuery(id+"F0.wireOp",EDGE,"E0.sketch_text.stroke-145"),sQuery(id+"F0.wireOp",EDGE,"E0.sketch_text.stroke-146"),sQuery(id+"F0.wireOp",EDGE,"E0.sketch_text.stroke-147")])],"isStart":true}),makeQuery(id+"F5.opExtrude","SWEPT_FACE",FACE,{"disambiguationData":[OSD([sQuery(id+"F4.wireOp",EDGE,"E10.0.2")])]})]});
            var Q11;
            Q11=makeQuery(id+"F7.opBoolean","INTERSECT",EDGE,{"derivedFrom":[makeQuery(id+"F1.opExtrude","CAP_FACE",FACE,{"disambiguationData":[OSD([sQuery(id+"F0.wireOp",EDGE,"E0.sketch_text.stroke-168"),sQuery(id+"F0.wireOp",EDGE,"E0.sketch_text.stroke-169"),sQuery(id+"F0.wireOp",EDGE,"E0.sketch_text.stroke-170"),sQuery(id+"F0.wireOp",EDGE,"E0.sketch_text.stroke-171"),sQuery(id+"F0.wireOp",EDGE,"E0.sketch_text.stroke-172"),sQuery(id+"F0.wireOp",EDGE,"E0.sketch_text.stroke-173"),sQuery(id+"F0.wireOp",EDGE,"E0.sketch_text.stroke-174"),sQuery(id+"F0.wireOp",EDGE,"E0.sketch_text.stroke-175"),sQuery(id+"F0.wireOp",EDGE,"E0.sketch_text.stroke-176")])],"isStart":true}),makeQuery(id+"F5.opExtrude","SWEPT_FACE",FACE,{"disambiguationData":[OSD([sQuery(id+"F4.wireOp",EDGE,"E10.0.2")])]})]});
            var Q12;
            Q12=makeQuery(id+"F7.opBoolean","INTERSECT",EDGE,{"derivedFrom":[makeQuery(id+"F1.opExtrude","CAP_FACE",FACE,{"disambiguationData":[OSD([sQuery(id+"F0.wireOp",EDGE,"E0.sketch_text.stroke-177"),sQuery(id+"F0.wireOp",EDGE,"E0.sketch_text.stroke-178"),sQuery(id+"F0.wireOp",EDGE,"E0.sketch_text.stroke-179"),sQuery(id+"F0.wireOp",EDGE,"E0.sketch_text.stroke-180"),sQuery(id+"F0.wireOp",EDGE,"E0.sketch_text.stroke-181"),sQuery(id+"F0.wireOp",EDGE,"E0.sketch_text.stroke-182"),sQuery(id+"F0.wireOp",EDGE,"E0.sketch_text.stroke-183"),sQuery(id+"F0.wireOp",EDGE,"E0.sketch_text.stroke-184"),sQuery(id+"F0.wireOp",EDGE,"E0.sketch_text.stroke-185"),sQuery(id+"F0.wireOp",EDGE,"E0.sketch_text.stroke-186"),sQuery(id+"F0.wireOp",EDGE,"E0.sketch_text.stroke-187"),sQuery(id+"F0.wireOp",EDGE,"E0.sketch_text.stroke-188"),sQuery(id+"F0.wireOp",EDGE,"E0.sketch_text.stroke-189"),sQuery(id+"F0.wireOp",EDGE,"E0.sketch_text.stroke-190")])],"isStart":true}),makeQuery(id+"F5.opExtrude","SWEPT_FACE",FACE,{"disambiguationData":[OSD([sQuery(id+"F4.wireOp",EDGE,"E10.0.2")])]})]});
            var Q13;
            Q13=makeQuery(id+"F7.opBoolean","INTERSECT",EDGE,{"derivedFrom":[makeQuery(id+"F1.opExtrude","CAP_FACE",FACE,{"disambiguationData":[OSD([sQuery(id+"F0.wireOp",EDGE,"E0.sketch_text.stroke-191"),sQuery(id+"F0.wireOp",EDGE,"E0.sketch_text.stroke-192"),sQuery(id+"F0.wireOp",EDGE,"E0.sketch_text.stroke-193"),sQuery(id+"F0.wireOp",EDGE,"E0.sketch_text.stroke-194")])],"isStart":true}),makeQuery(id+"F5.opExtrude","SWEPT_FACE",FACE,{"disambiguationData":[OSD([sQuery(id+"F4.wireOp",EDGE,"E10.0.2")])]})]});
            var Q14;
            Q14=makeQuery(id+"F7.opBoolean","INTERSECT",EDGE,{"derivedFrom":[makeQuery(id+"F1.opExtrude","CAP_FACE",FACE,{"disambiguationData":[OSD([sQuery(id+"F0.wireOp",EDGE,"E0.sketch_text.stroke-195"),sQuery(id+"F0.wireOp",EDGE,"E0.sketch_text.stroke-196"),sQuery(id+"F0.wireOp",EDGE,"E0.sketch_text.stroke-197"),sQuery(id+"F0.wireOp",EDGE,"E0.sketch_text.stroke-198"),sQuery(id+"F0.wireOp",EDGE,"E0.sketch_text.stroke-199"),sQuery(id+"F0.wireOp",EDGE,"E0.sketch_text.stroke-200"),sQuery(id+"F0.wireOp",EDGE,"E0.sketch_text.stroke-201"),sQuery(id+"F0.wireOp",EDGE,"E0.sketch_text.stroke-202"),sQuery(id+"F0.wireOp",EDGE,"E0.sketch_text.stroke-203"),sQuery(id+"F0.wireOp",EDGE,"E0.sketch_text.stroke-204"),sQuery(id+"F0.wireOp",EDGE,"E0.sketch_text.stroke-205"),sQuery(id+"F0.wireOp",EDGE,"E0.sketch_text.stroke-206"),sQuery(id+"F0.wireOp",EDGE,"E0.sketch_text.stroke-207"),sQuery(id+"F0.wireOp",EDGE,"E0.sketch_text.stroke-208"),sQuery(id+"F0.wireOp",EDGE,"E0.sketch_text.stroke-209"),sQuery(id+"F0.wireOp",EDGE,"E0.sketch_text.stroke-210"),sQuery(id+"F0.wireOp",EDGE,"E0.sketch_text.stroke-211"),sQuery(id+"F0.wireOp",EDGE,"E0.sketch_text.stroke-212"),sQuery(id+"F0.wireOp",EDGE,"E0.sketch_text.stroke-213")])],"isStart":true}),makeQuery(id+"F5.opExtrude","SWEPT_FACE",FACE,{"disambiguationData":[OSD([sQuery(id+"F4.wireOp",EDGE,"E10.0.2")])]})]});
            var Q15;
            Q15=makeQuery(id+"F8.opBoolean","INTERSECT",EDGE,{"derivedFrom":[makeQuery(id+"F1.opExtrude","CAP_FACE",FACE,{"disambiguationData":[OSD([sQuery(id+"F0.wireOp",EDGE,"E1.sketch_text.stroke-99"),sQuery(id+"F0.wireOp",EDGE,"E1.sketch_text.stroke-100"),sQuery(id+"F0.wireOp",EDGE,"E1.sketch_text.stroke-101"),sQuery(id+"F0.wireOp",EDGE,"E1.sketch_text.stroke-102"),sQuery(id+"F0.wireOp",EDGE,"E1.sketch_text.stroke-103")])],"isStart":true}),makeQuery(id+"F5.opExtrude","SWEPT_FACE",FACE,{"disambiguationData":[OSD([sQuery(id+"F4.wireOp",EDGE,"E11.0.0")])]})]});
            var Q16;
            Q16=makeQuery(id+"F8.opBoolean","INTERSECT",EDGE,{"derivedFrom":[makeQuery(id+"F1.opExtrude","CAP_FACE",FACE,{"disambiguationData":[OSD([sQuery(id+"F0.wireOp",EDGE,"E1.sketch_text.stroke-0"),sQuery(id+"F0.wireOp",EDGE,"E1.sketch_text.stroke-1"),sQuery(id+"F0.wireOp",EDGE,"E1.sketch_text.stroke-2"),sQuery(id+"F0.wireOp",EDGE,"E1.sketch_text.stroke-3"),sQuery(id+"F0.wireOp",EDGE,"E1.sketch_text.stroke-4"),sQuery(id+"F0.wireOp",EDGE,"E1.sketch_text.stroke-5"),sQuery(id+"F0.wireOp",EDGE,"E1.sketch_text.stroke-6"),sQuery(id+"F0.wireOp",EDGE,"E1.sketch_text.stroke-7"),sQuery(id+"F0.wireOp",EDGE,"E1.sketch_text.stroke-8"),sQuery(id+"F0.wireOp",EDGE,"E1.sketch_text.stroke-9"),sQuery(id+"F0.wireOp",EDGE,"E1.sketch_text.stroke-10")])],"isStart":true}),makeQuery(id+"F5.opExtrude","SWEPT_FACE",FACE,{"disambiguationData":[OSD([sQuery(id+"F4.wireOp",EDGE,"E11.0.0")])]})]});
            var Q17;
            Q17=makeQuery(id+"F8.opBoolean","INTERSECT",EDGE,{"derivedFrom":[makeQuery(id+"F1.opExtrude","CAP_FACE",FACE,{"disambiguationData":[OSD([sQuery(id+"F0.wireOp",EDGE,"E1.sketch_text.stroke-11"),sQuery(id+"F0.wireOp",EDGE,"E1.sketch_text.stroke-12"),sQuery(id+"F0.wireOp",EDGE,"E1.sketch_text.stroke-13"),sQuery(id+"F0.wireOp",EDGE,"E1.sketch_text.stroke-14"),sQuery(id+"F0.wireOp",EDGE,"E1.sketch_text.stroke-15"),sQuery(id+"F0.wireOp",EDGE,"E1.sketch_text.stroke-16"),sQuery(id+"F0.wireOp",EDGE,"E1.sketch_text.stroke-17"),sQuery(id+"F0.wireOp",EDGE,"E1.sketch_text.stroke-18"),sQuery(id+"F0.wireOp",EDGE,"E1.sketch_text.stroke-19"),sQuery(id+"F0.wireOp",EDGE,"E1.sketch_text.stroke-20"),sQuery(id+"F0.wireOp",EDGE,"E1.sketch_text.stroke-21"),sQuery(id+"F0.wireOp",EDGE,"E1.sketch_text.stroke-22"),sQuery(id+"F0.wireOp",EDGE,"E1.sketch_text.stroke-23"),sQuery(id+"F0.wireOp",EDGE,"E1.sketch_text.stroke-24")])],"isStart":true}),makeQuery(id+"F5.opExtrude","SWEPT_FACE",FACE,{"disambiguationData":[OSD([sQuery(id+"F4.wireOp",EDGE,"E11.0.0")])]})]});
            var Q18;
            Q18=makeQuery(id+"F8.opBoolean","INTERSECT",EDGE,{"derivedFrom":[makeQuery(id+"F1.opExtrude","CAP_FACE",FACE,{"disambiguationData":[OSD([sQuery(id+"F0.wireOp",EDGE,"E1.sketch_text.stroke-70"),sQuery(id+"F0.wireOp",EDGE,"E1.sketch_text.stroke-71"),sQuery(id+"F0.wireOp",EDGE,"E1.sketch_text.stroke-72"),sQuery(id+"F0.wireOp",EDGE,"E1.sketch_text.stroke-73"),sQuery(id+"F0.wireOp",EDGE,"E1.sketch_text.stroke-74")])],"isStart":true}),makeQuery(id+"F5.opExtrude","SWEPT_FACE",FACE,{"disambiguationData":[OSD([sQuery(id+"F4.wireOp",EDGE,"E11.0.2")])]})]});
            var Q19;
            Q19=makeQuery(id+"F8.opBoolean","INTERSECT",EDGE,{"derivedFrom":[makeQuery(id+"F1.opExtrude","CAP_FACE",FACE,{"disambiguationData":[OSD([sQuery(id+"F0.wireOp",EDGE,"E1.sketch_text.stroke-75"),sQuery(id+"F0.wireOp",EDGE,"E1.sketch_text.stroke-76"),sQuery(id+"F0.wireOp",EDGE,"E1.sketch_text.stroke-77"),sQuery(id+"F0.wireOp",EDGE,"E1.sketch_text.stroke-78"),sQuery(id+"F0.wireOp",EDGE,"E1.sketch_text.stroke-79")])],"isStart":true}),makeQuery(id+"F5.opExtrude","SWEPT_FACE",FACE,{"disambiguationData":[OSD([sQuery(id+"F4.wireOp",EDGE,"E11.0.2")])]})]});
            var Q20;
            Q20=makeQuery(id+"F8.opBoolean","INTERSECT",EDGE,{"derivedFrom":[makeQuery(id+"F1.opExtrude","CAP_FACE",FACE,{"disambiguationData":[OSD([sQuery(id+"F0.wireOp",EDGE,"E1.sketch_text.stroke-80"),sQuery(id+"F0.wireOp",EDGE,"E1.sketch_text.stroke-81"),sQuery(id+"F0.wireOp",EDGE,"E1.sketch_text.stroke-82"),sQuery(id+"F0.wireOp",EDGE,"E1.sketch_text.stroke-83"),sQuery(id+"F0.wireOp",EDGE,"E1.sketch_text.stroke-84"),sQuery(id+"F0.wireOp",EDGE,"E1.sketch_text.stroke-85"),sQuery(id+"F0.wireOp",EDGE,"E1.sketch_text.stroke-86"),sQuery(id+"F0.wireOp",EDGE,"E1.sketch_text.stroke-87"),sQuery(id+"F0.wireOp",EDGE,"E1.sketch_text.stroke-88"),sQuery(id+"F0.wireOp",EDGE,"E1.sketch_text.stroke-89"),sQuery(id+"F0.wireOp",EDGE,"E1.sketch_text.stroke-90"),sQuery(id+"F0.wireOp",EDGE,"E1.sketch_text.stroke-91"),sQuery(id+"F0.wireOp",EDGE,"E1.sketch_text.stroke-92"),sQuery(id+"F0.wireOp",EDGE,"E1.sketch_text.stroke-93"),sQuery(id+"F0.wireOp",EDGE,"E1.sketch_text.stroke-94"),sQuery(id+"F0.wireOp",EDGE,"E1.sketch_text.stroke-95"),sQuery(id+"F0.wireOp",EDGE,"E1.sketch_text.stroke-96"),sQuery(id+"F0.wireOp",EDGE,"E1.sketch_text.stroke-97"),sQuery(id+"F0.wireOp",EDGE,"E1.sketch_text.stroke-98")])],"isStart":true}),makeQuery(id+"F5.opExtrude","SWEPT_FACE",FACE,{"disambiguationData":[OSD([sQuery(id+"F4.wireOp",EDGE,"E11.0.2")])]})]});
            var Q21;
            Q21=makeQuery(id+"F8.opBoolean","INTERSECT",EDGE,{"derivedFrom":[makeQuery(id+"F1.opExtrude","CAP_FACE",FACE,{"disambiguationData":[OSD([sQuery(id+"F0.wireOp",EDGE,"E1.sketch_text.stroke-104"),sQuery(id+"F0.wireOp",EDGE,"E1.sketch_text.stroke-105"),sQuery(id+"F0.wireOp",EDGE,"E1.sketch_text.stroke-106"),sQuery(id+"F0.wireOp",EDGE,"E1.sketch_text.stroke-107"),sQuery(id+"F0.wireOp",EDGE,"E1.sketch_text.stroke-108"),sQuery(id+"F0.wireOp",EDGE,"E1.sketch_text.stroke-109"),sQuery(id+"F0.wireOp",EDGE,"E1.sketch_text.stroke-110"),sQuery(id+"F0.wireOp",EDGE,"E1.sketch_text.stroke-111"),sQuery(id+"F0.wireOp",EDGE,"E1.sketch_text.stroke-112"),sQuery(id+"F0.wireOp",EDGE,"E1.sketch_text.stroke-113"),sQuery(id+"F0.wireOp",EDGE,"E1.sketch_text.stroke-114"),sQuery(id+"F0.wireOp",EDGE,"E1.sketch_text.stroke-115"),sQuery(id+"F0.wireOp",EDGE,"E1.sketch_text.stroke-116"),sQuery(id+"F0.wireOp",EDGE,"E1.sketch_text.stroke-117"),sQuery(id+"F0.wireOp",EDGE,"E1.sketch_text.stroke-118"),sQuery(id+"F0.wireOp",EDGE,"E1.sketch_text.stroke-119"),sQuery(id+"F0.wireOp",EDGE,"E1.sketch_text.stroke-120"),sQuery(id+"F0.wireOp",EDGE,"E1.sketch_text.stroke-121"),sQuery(id+"F0.wireOp",EDGE,"E1.sketch_text.stroke-122"),sQuery(id+"F0.wireOp",EDGE,"E1.sketch_text.stroke-123"),sQuery(id+"F0.wireOp",EDGE,"E1.sketch_text.stroke-124"),sQuery(id+"F0.wireOp",EDGE,"E1.sketch_text.stroke-125"),sQuery(id+"F0.wireOp",EDGE,"E1.sketch_text.stroke-126"),sQuery(id+"F0.wireOp",EDGE,"E1.sketch_text.stroke-127"),sQuery(id+"F0.wireOp",EDGE,"E1.sketch_text.stroke-128")])],"isStart":true}),makeQuery(id+"F5.opExtrude","SWEPT_FACE",FACE,{"disambiguationData":[OSD([sQuery(id+"F4.wireOp",EDGE,"E11.0.2")])]})]});
            var Q22;
            Q22=makeQuery(id+"F8.opBoolean","INTERSECT",EDGE,{"derivedFrom":[makeQuery(id+"F1.opExtrude","CAP_FACE",FACE,{"disambiguationData":[OSD([sQuery(id+"F0.wireOp",EDGE,"E1.sketch_text.stroke-99"),sQuery(id+"F0.wireOp",EDGE,"E1.sketch_text.stroke-100"),sQuery(id+"F0.wireOp",EDGE,"E1.sketch_text.stroke-101"),sQuery(id+"F0.wireOp",EDGE,"E1.sketch_text.stroke-102"),sQuery(id+"F0.wireOp",EDGE,"E1.sketch_text.stroke-103")])],"isStart":true}),makeQuery(id+"F5.opExtrude","SWEPT_FACE",FACE,{"disambiguationData":[OSD([sQuery(id+"F4.wireOp",EDGE,"E11.0.2")])]})]});
            var Q23;
            Q23=makeQuery(id+"F8.opBoolean","INTERSECT",EDGE,{"derivedFrom":[makeQuery(id+"F1.opExtrude","CAP_FACE",FACE,{"disambiguationData":[OSD([sQuery(id+"F0.wireOp",EDGE,"E1.sketch_text.stroke-129"),sQuery(id+"F0.wireOp",EDGE,"E1.sketch_text.stroke-130"),sQuery(id+"F0.wireOp",EDGE,"E1.sketch_text.stroke-131"),sQuery(id+"F0.wireOp",EDGE,"E1.sketch_text.stroke-132"),sQuery(id+"F0.wireOp",EDGE,"E1.sketch_text.stroke-133"),sQuery(id+"F0.wireOp",EDGE,"E1.sketch_text.stroke-134"),sQuery(id+"F0.wireOp",EDGE,"E1.sketch_text.stroke-135"),sQuery(id+"F0.wireOp",EDGE,"E1.sketch_text.stroke-136"),sQuery(id+"F0.wireOp",EDGE,"E1.sketch_text.stroke-137"),sQuery(id+"F0.wireOp",EDGE,"E1.sketch_text.stroke-138"),sQuery(id+"F0.wireOp",EDGE,"E1.sketch_text.stroke-139"),sQuery(id+"F0.wireOp",EDGE,"E1.sketch_text.stroke-140"),sQuery(id+"F0.wireOp",EDGE,"E1.sketch_text.stroke-141"),sQuery(id+"F0.wireOp",EDGE,"E1.sketch_text.stroke-142"),sQuery(id+"F0.wireOp",EDGE,"E1.sketch_text.stroke-143"),sQuery(id+"F0.wireOp",EDGE,"E1.sketch_text.stroke-144"),sQuery(id+"F0.wireOp",EDGE,"E1.sketch_text.stroke-145"),sQuery(id+"F0.wireOp",EDGE,"E1.sketch_text.stroke-146"),sQuery(id+"F0.wireOp",EDGE,"E1.sketch_text.stroke-147")])],"isStart":true}),makeQuery(id+"F5.opExtrude","SWEPT_FACE",FACE,{"disambiguationData":[OSD([sQuery(id+"F4.wireOp",EDGE,"E11.0.2")])]})]});
            var Q24;
            Q24=makeQuery(id+"F8.opBoolean","INTERSECT",EDGE,{"disambiguationData":[OD(1.0)],"derivedFrom":[makeQuery(id+"F1.opExtrude","CAP_FACE",FACE,{"disambiguationData":[OSD([sQuery(id+"F0.wireOp",EDGE,"E1.sketch_text.stroke-148"),sQuery(id+"F0.wireOp",EDGE,"E1.sketch_text.stroke-149"),sQuery(id+"F0.wireOp",EDGE,"E1.sketch_text.stroke-150"),sQuery(id+"F0.wireOp",EDGE,"E1.sketch_text.stroke-151"),sQuery(id+"F0.wireOp",EDGE,"E1.sketch_text.stroke-152"),sQuery(id+"F0.wireOp",EDGE,"E1.sketch_text.stroke-153"),sQuery(id+"F0.wireOp",EDGE,"E1.sketch_text.stroke-154"),sQuery(id+"F0.wireOp",EDGE,"E1.sketch_text.stroke-155"),sQuery(id+"F0.wireOp",EDGE,"E1.sketch_text.stroke-156"),sQuery(id+"F0.wireOp",EDGE,"E1.sketch_text.stroke-157"),sQuery(id+"F0.wireOp",EDGE,"E1.sketch_text.stroke-158"),sQuery(id+"F0.wireOp",EDGE,"E1.sketch_text.stroke-159"),sQuery(id+"F0.wireOp",EDGE,"E1.sketch_text.stroke-160"),sQuery(id+"F0.wireOp",EDGE,"E1.sketch_text.stroke-161"),sQuery(id+"F0.wireOp",EDGE,"E1.sketch_text.stroke-162"),sQuery(id+"F0.wireOp",EDGE,"E1.sketch_text.stroke-163"),sQuery(id+"F0.wireOp",EDGE,"E1.sketch_text.stroke-164"),sQuery(id+"F0.wireOp",EDGE,"E1.sketch_text.stroke-165"),sQuery(id+"F0.wireOp",EDGE,"E1.sketch_text.stroke-166"),sQuery(id+"F0.wireOp",EDGE,"E1.sketch_text.stroke-167"),sQuery(id+"F0.wireOp",EDGE,"E1.sketch_text.stroke-168"),sQuery(id+"F0.wireOp",EDGE,"E1.sketch_text.stroke-169"),sQuery(id+"F0.wireOp",EDGE,"E1.sketch_text.stroke-170"),sQuery(id+"F0.wireOp",EDGE,"E1.sketch_text.stroke-171"),sQuery(id+"F0.wireOp",EDGE,"E1.sketch_text.stroke-172"),sQuery(id+"F0.wireOp",EDGE,"E1.sketch_text.stroke-173"),sQuery(id+"F0.wireOp",EDGE,"E1.sketch_text.stroke-174"),sQuery(id+"F0.wireOp",EDGE,"E1.sketch_text.stroke-175"),sQuery(id+"F0.wireOp",EDGE,"E1.sketch_text.stroke-176"),sQuery(id+"F0.wireOp",EDGE,"E1.sketch_text.stroke-177"),sQuery(id+"F0.wireOp",EDGE,"E1.sketch_text.stroke-178"),sQuery(id+"F0.wireOp",EDGE,"E1.sketch_text.stroke-179"),sQuery(id+"F0.wireOp",EDGE,"E1.sketch_text.stroke-180"),sQuery(id+"F0.wireOp",EDGE,"E1.sketch_text.stroke-181"),sQuery(id+"F0.wireOp",EDGE,"E1.sketch_text.stroke-182"),sQuery(id+"F0.wireOp",EDGE,"E1.sketch_text.stroke-183")])],"isStart":true}),makeQuery(id+"F5.opExtrude","SWEPT_FACE",FACE,{"disambiguationData":[OSD([sQuery(id+"F4.wireOp",EDGE,"E11.0.2")])]})]});
            var Q25;
            Q25=makeQuery(id+"F8.opBoolean","INTERSECT",EDGE,{"disambiguationData":[OD(0.0)],"derivedFrom":[makeQuery(id+"F1.opExtrude","CAP_FACE",FACE,{"disambiguationData":[OSD([sQuery(id+"F0.wireOp",EDGE,"E1.sketch_text.stroke-148"),sQuery(id+"F0.wireOp",EDGE,"E1.sketch_text.stroke-149"),sQuery(id+"F0.wireOp",EDGE,"E1.sketch_text.stroke-150"),sQuery(id+"F0.wireOp",EDGE,"E1.sketch_text.stroke-151"),sQuery(id+"F0.wireOp",EDGE,"E1.sketch_text.stroke-152"),sQuery(id+"F0.wireOp",EDGE,"E1.sketch_text.stroke-153"),sQuery(id+"F0.wireOp",EDGE,"E1.sketch_text.stroke-154"),sQuery(id+"F0.wireOp",EDGE,"E1.sketch_text.stroke-155"),sQuery(id+"F0.wireOp",EDGE,"E1.sketch_text.stroke-156"),sQuery(id+"F0.wireOp",EDGE,"E1.sketch_text.stroke-157"),sQuery(id+"F0.wireOp",EDGE,"E1.sketch_text.stroke-158"),sQuery(id+"F0.wireOp",EDGE,"E1.sketch_text.stroke-159"),sQuery(id+"F0.wireOp",EDGE,"E1.sketch_text.stroke-160"),sQuery(id+"F0.wireOp",EDGE,"E1.sketch_text.stroke-161"),sQuery(id+"F0.wireOp",EDGE,"E1.sketch_text.stroke-162"),sQuery(id+"F0.wireOp",EDGE,"E1.sketch_text.stroke-163"),sQuery(id+"F0.wireOp",EDGE,"E1.sketch_text.stroke-164"),sQuery(id+"F0.wireOp",EDGE,"E1.sketch_text.stroke-165"),sQuery(id+"F0.wireOp",EDGE,"E1.sketch_text.stroke-166"),sQuery(id+"F0.wireOp",EDGE,"E1.sketch_text.stroke-167"),sQuery(id+"F0.wireOp",EDGE,"E1.sketch_text.stroke-168"),sQuery(id+"F0.wireOp",EDGE,"E1.sketch_text.stroke-169"),sQuery(id+"F0.wireOp",EDGE,"E1.sketch_text.stroke-170"),sQuery(id+"F0.wireOp",EDGE,"E1.sketch_text.stroke-171"),sQuery(id+"F0.wireOp",EDGE,"E1.sketch_text.stroke-172"),sQuery(id+"F0.wireOp",EDGE,"E1.sketch_text.stroke-173"),sQuery(id+"F0.wireOp",EDGE,"E1.sketch_text.stroke-174"),sQuery(id+"F0.wireOp",EDGE,"E1.sketch_text.stroke-175"),sQuery(id+"F0.wireOp",EDGE,"E1.sketch_text.stroke-176"),sQuery(id+"F0.wireOp",EDGE,"E1.sketch_text.stroke-177"),sQuery(id+"F0.wireOp",EDGE,"E1.sketch_text.stroke-178"),sQuery(id+"F0.wireOp",EDGE,"E1.sketch_text.stroke-179"),sQuery(id+"F0.wireOp",EDGE,"E1.sketch_text.stroke-180"),sQuery(id+"F0.wireOp",EDGE,"E1.sketch_text.stroke-181"),sQuery(id+"F0.wireOp",EDGE,"E1.sketch_text.stroke-182"),sQuery(id+"F0.wireOp",EDGE,"E1.sketch_text.stroke-183")])],"isStart":true}),makeQuery(id+"F5.opExtrude","SWEPT_FACE",FACE,{"disambiguationData":[OSD([sQuery(id+"F4.wireOp",EDGE,"E11.0.2")])]})]});
            var Q26;
            Q26=makeQuery(id+"F8.opBoolean","INTERSECT",EDGE,{"derivedFrom":[makeQuery(id+"F1.opExtrude","CAP_FACE",FACE,{"disambiguationData":[OSD([sQuery(id+"F0.wireOp",EDGE,"E1.sketch_text.stroke-184"),sQuery(id+"F0.wireOp",EDGE,"E1.sketch_text.stroke-185"),sQuery(id+"F0.wireOp",EDGE,"E1.sketch_text.stroke-186"),sQuery(id+"F0.wireOp",EDGE,"E1.sketch_text.stroke-187"),sQuery(id+"F0.wireOp",EDGE,"E1.sketch_text.stroke-188"),sQuery(id+"F0.wireOp",EDGE,"E1.sketch_text.stroke-189"),sQuery(id+"F0.wireOp",EDGE,"E1.sketch_text.stroke-190")])],"isStart":true}),makeQuery(id+"F5.opExtrude","SWEPT_FACE",FACE,{"disambiguationData":[OSD([sQuery(id+"F4.wireOp",EDGE,"E11.0.2")])]})]});
            var Q27;
            Q27=makeQuery(id+"F9.opBoolean","INTERSECT",EDGE,{"derivedFrom":[makeQuery(id+"F1.opExtrude","CAP_FACE",FACE,{"disambiguationData":[OSD([sQuery(id+"F0.wireOp",EDGE,"E2.sketch_text.stroke-318"),sQuery(id+"F0.wireOp",EDGE,"E2.sketch_text.stroke-319"),sQuery(id+"F0.wireOp",EDGE,"E2.sketch_text.stroke-320"),sQuery(id+"F0.wireOp",EDGE,"E2.sketch_text.stroke-321")])],"isStart":true}),makeQuery(id+"F5.opExtrude","SWEPT_FACE",FACE,{"disambiguationData":[OSD([sQuery(id+"F4.wireOp",EDGE,"E12.0.0")])]})]});
            var Q28;
            Q28=makeQuery(id+"F9.opBoolean","INTERSECT",EDGE,{"derivedFrom":[makeQuery(id+"F1.opExtrude","CAP_FACE",FACE,{"disambiguationData":[OSD([sQuery(id+"F0.wireOp",EDGE,"E2.sketch_text.stroke-171"),sQuery(id+"F0.wireOp",EDGE,"E2.sketch_text.stroke-172"),sQuery(id+"F0.wireOp",EDGE,"E2.sketch_text.stroke-173"),sQuery(id+"F0.wireOp",EDGE,"E2.sketch_text.stroke-174"),sQuery(id+"F0.wireOp",EDGE,"E2.sketch_text.stroke-175")])],"isStart":true}),makeQuery(id+"F5.opExtrude","SWEPT_FACE",FACE,{"disambiguationData":[OSD([sQuery(id+"F4.wireOp",EDGE,"E12.0.0")])]})]});
            var Q29;
            Q29=makeQuery(id+"F9.opBoolean","INTERSECT",EDGE,{"derivedFrom":[makeQuery(id+"F1.opExtrude","CAP_FACE",FACE,{"disambiguationData":[OSD([sQuery(id+"F0.wireOp",EDGE,"E2.sketch_text.stroke-0"),sQuery(id+"F0.wireOp",EDGE,"E2.sketch_text.stroke-1"),sQuery(id+"F0.wireOp",EDGE,"E2.sketch_text.stroke-2"),sQuery(id+"F0.wireOp",EDGE,"E2.sketch_text.stroke-3"),sQuery(id+"F0.wireOp",EDGE,"E2.sketch_text.stroke-4"),sQuery(id+"F0.wireOp",EDGE,"E2.sketch_text.stroke-5"),sQuery(id+"F0.wireOp",EDGE,"E2.sketch_text.stroke-6"),sQuery(id+"F0.wireOp",EDGE,"E2.sketch_text.stroke-7"),sQuery(id+"F0.wireOp",EDGE,"E2.sketch_text.stroke-8"),sQuery(id+"F0.wireOp",EDGE,"E2.sketch_text.stroke-9"),sQuery(id+"F0.wireOp",EDGE,"E2.sketch_text.stroke-10"),sQuery(id+"F0.wireOp",EDGE,"E2.sketch_text.stroke-11"),sQuery(id+"F0.wireOp",EDGE,"E2.sketch_text.stroke-12"),sQuery(id+"F0.wireOp",EDGE,"E2.sketch_text.stroke-13"),sQuery(id+"F0.wireOp",EDGE,"E2.sketch_text.stroke-14"),sQuery(id+"F0.wireOp",EDGE,"E2.sketch_text.stroke-15"),sQuery(id+"F0.wireOp",EDGE,"E2.sketch_text.stroke-16"),sQuery(id+"F0.wireOp",EDGE,"E2.sketch_text.stroke-17")])],"isStart":true}),makeQuery(id+"F5.opExtrude","SWEPT_FACE",FACE,{"disambiguationData":[OSD([sQuery(id+"F4.wireOp",EDGE,"E12.0.0")])]})]});
            var Q30;
            Q30=makeQuery(id+"F9.opBoolean","INTERSECT",EDGE,{"derivedFrom":[makeQuery(id+"F1.opExtrude","CAP_FACE",FACE,{"disambiguationData":[OSD([sQuery(id+"F0.wireOp",EDGE,"E2.sketch_text.stroke-18"),sQuery(id+"F0.wireOp",EDGE,"E2.sketch_text.stroke-19"),sQuery(id+"F0.wireOp",EDGE,"E2.sketch_text.stroke-20"),sQuery(id+"F0.wireOp",EDGE,"E2.sketch_text.stroke-21"),sQuery(id+"F0.wireOp",EDGE,"E2.sketch_text.stroke-22"),sQuery(id+"F0.wireOp",EDGE,"E2.sketch_text.stroke-23"),sQuery(id+"F0.wireOp",EDGE,"E2.sketch_text.stroke-24"),sQuery(id+"F0.wireOp",EDGE,"E2.sketch_text.stroke-25"),sQuery(id+"F0.wireOp",EDGE,"E2.sketch_text.stroke-26"),sQuery(id+"F0.wireOp",EDGE,"E2.sketch_text.stroke-27"),sQuery(id+"F0.wireOp",EDGE,"E2.sketch_text.stroke-28"),sQuery(id+"F0.wireOp",EDGE,"E2.sketch_text.stroke-29"),sQuery(id+"F0.wireOp",EDGE,"E2.sketch_text.stroke-30"),sQuery(id+"F0.wireOp",EDGE,"E2.sketch_text.stroke-31"),sQuery(id+"F0.wireOp",EDGE,"E2.sketch_text.stroke-32"),sQuery(id+"F0.wireOp",EDGE,"E2.sketch_text.stroke-33"),sQuery(id+"F0.wireOp",EDGE,"E2.sketch_text.stroke-34"),sQuery(id+"F0.wireOp",EDGE,"E2.sketch_text.stroke-35"),sQuery(id+"F0.wireOp",EDGE,"E2.sketch_text.stroke-36")])],"isStart":true}),makeQuery(id+"F5.opExtrude","SWEPT_FACE",FACE,{"disambiguationData":[OSD([sQuery(id+"F4.wireOp",EDGE,"E12.0.2")])]})]});
            var Q31;
            Q31=makeQuery(id+"F9.opBoolean","INTERSECT",EDGE,{"disambiguationData":[OD(1.0)],"derivedFrom":[makeQuery(id+"F1.opExtrude","CAP_FACE",FACE,{"disambiguationData":[OSD([sQuery(id+"F0.wireOp",EDGE,"E2.sketch_text.stroke-37"),sQuery(id+"F0.wireOp",EDGE,"E2.sketch_text.stroke-38"),sQuery(id+"F0.wireOp",EDGE,"E2.sketch_text.stroke-39"),sQuery(id+"F0.wireOp",EDGE,"E2.sketch_text.stroke-40"),sQuery(id+"F0.wireOp",EDGE,"E2.sketch_text.stroke-41"),sQuery(id+"F0.wireOp",EDGE,"E2.sketch_text.stroke-42"),sQuery(id+"F0.wireOp",EDGE,"E2.sketch_text.stroke-43"),sQuery(id+"F0.wireOp",EDGE,"E2.sketch_text.stroke-44"),sQuery(id+"F0.wireOp",EDGE,"E2.sketch_text.stroke-45"),sQuery(id+"F0.wireOp",EDGE,"E2.sketch_text.stroke-46"),sQuery(id+"F0.wireOp",EDGE,"E2.sketch_text.stroke-47"),sQuery(id+"F0.wireOp",EDGE,"E2.sketch_text.stroke-48"),sQuery(id+"F0.wireOp",EDGE,"E2.sketch_text.stroke-49"),sQuery(id+"F0.wireOp",EDGE,"E2.sketch_text.stroke-50"),sQuery(id+"F0.wireOp",EDGE,"E2.sketch_text.stroke-51"),sQuery(id+"F0.wireOp",EDGE,"E2.sketch_text.stroke-52"),sQuery(id+"F0.wireOp",EDGE,"E2.sketch_text.stroke-53"),sQuery(id+"F0.wireOp",EDGE,"E2.sketch_text.stroke-54"),sQuery(id+"F0.wireOp",EDGE,"E2.sketch_text.stroke-55"),sQuery(id+"F0.wireOp",EDGE,"E2.sketch_text.stroke-56"),sQuery(id+"F0.wireOp",EDGE,"E2.sketch_text.stroke-57"),sQuery(id+"F0.wireOp",EDGE,"E2.sketch_text.stroke-58"),sQuery(id+"F0.wireOp",EDGE,"E2.sketch_text.stroke-59"),sQuery(id+"F0.wireOp",EDGE,"E2.sketch_text.stroke-60"),sQuery(id+"F0.wireOp",EDGE,"E2.sketch_text.stroke-61"),sQuery(id+"F0.wireOp",EDGE,"E2.sketch_text.stroke-62"),sQuery(id+"F0.wireOp",EDGE,"E2.sketch_text.stroke-63"),sQuery(id+"F0.wireOp",EDGE,"E2.sketch_text.stroke-64"),sQuery(id+"F0.wireOp",EDGE,"E2.sketch_text.stroke-65"),sQuery(id+"F0.wireOp",EDGE,"E2.sketch_text.stroke-66"),sQuery(id+"F0.wireOp",EDGE,"E2.sketch_text.stroke-67"),sQuery(id+"F0.wireOp",EDGE,"E2.sketch_text.stroke-68"),sQuery(id+"F0.wireOp",EDGE,"E2.sketch_text.stroke-69"),sQuery(id+"F0.wireOp",EDGE,"E2.sketch_text.stroke-70"),sQuery(id+"F0.wireOp",EDGE,"E2.sketch_text.stroke-71"),sQuery(id+"F0.wireOp",EDGE,"E2.sketch_text.stroke-72")])],"isStart":true}),makeQuery(id+"F5.opExtrude","SWEPT_FACE",FACE,{"disambiguationData":[OSD([sQuery(id+"F4.wireOp",EDGE,"E12.0.2")])]})]});
            var Q32;
            Q32=makeQuery(id+"F9.opBoolean","INTERSECT",EDGE,{"disambiguationData":[OD(0.0)],"derivedFrom":[makeQuery(id+"F1.opExtrude","CAP_FACE",FACE,{"disambiguationData":[OSD([sQuery(id+"F0.wireOp",EDGE,"E2.sketch_text.stroke-37"),sQuery(id+"F0.wireOp",EDGE,"E2.sketch_text.stroke-38"),sQuery(id+"F0.wireOp",EDGE,"E2.sketch_text.stroke-39"),sQuery(id+"F0.wireOp",EDGE,"E2.sketch_text.stroke-40"),sQuery(id+"F0.wireOp",EDGE,"E2.sketch_text.stroke-41"),sQuery(id+"F0.wireOp",EDGE,"E2.sketch_text.stroke-42"),sQuery(id+"F0.wireOp",EDGE,"E2.sketch_text.stroke-43"),sQuery(id+"F0.wireOp",EDGE,"E2.sketch_text.stroke-44"),sQuery(id+"F0.wireOp",EDGE,"E2.sketch_text.stroke-45"),sQuery(id+"F0.wireOp",EDGE,"E2.sketch_text.stroke-46"),sQuery(id+"F0.wireOp",EDGE,"E2.sketch_text.stroke-47"),sQuery(id+"F0.wireOp",EDGE,"E2.sketch_text.stroke-48"),sQuery(id+"F0.wireOp",EDGE,"E2.sketch_text.stroke-49"),sQuery(id+"F0.wireOp",EDGE,"E2.sketch_text.stroke-50"),sQuery(id+"F0.wireOp",EDGE,"E2.sketch_text.stroke-51"),sQuery(id+"F0.wireOp",EDGE,"E2.sketch_text.stroke-52"),sQuery(id+"F0.wireOp",EDGE,"E2.sketch_text.stroke-53"),sQuery(id+"F0.wireOp",EDGE,"E2.sketch_text.stroke-54"),sQuery(id+"F0.wireOp",EDGE,"E2.sketch_text.stroke-55"),sQuery(id+"F0.wireOp",EDGE,"E2.sketch_text.stroke-56"),sQuery(id+"F0.wireOp",EDGE,"E2.sketch_text.stroke-57"),sQuery(id+"F0.wireOp",EDGE,"E2.sketch_text.stroke-58"),sQuery(id+"F0.wireOp",EDGE,"E2.sketch_text.stroke-59"),sQuery(id+"F0.wireOp",EDGE,"E2.sketch_text.stroke-60"),sQuery(id+"F0.wireOp",EDGE,"E2.sketch_text.stroke-61"),sQuery(id+"F0.wireOp",EDGE,"E2.sketch_text.stroke-62"),sQuery(id+"F0.wireOp",EDGE,"E2.sketch_text.stroke-63"),sQuery(id+"F0.wireOp",EDGE,"E2.sketch_text.stroke-64"),sQuery(id+"F0.wireOp",EDGE,"E2.sketch_text.stroke-65"),sQuery(id+"F0.wireOp",EDGE,"E2.sketch_text.stroke-66"),sQuery(id+"F0.wireOp",EDGE,"E2.sketch_text.stroke-67"),sQuery(id+"F0.wireOp",EDGE,"E2.sketch_text.stroke-68"),sQuery(id+"F0.wireOp",EDGE,"E2.sketch_text.stroke-69"),sQuery(id+"F0.wireOp",EDGE,"E2.sketch_text.stroke-70"),sQuery(id+"F0.wireOp",EDGE,"E2.sketch_text.stroke-71"),sQuery(id+"F0.wireOp",EDGE,"E2.sketch_text.stroke-72")])],"isStart":true}),makeQuery(id+"F5.opExtrude","SWEPT_FACE",FACE,{"disambiguationData":[OSD([sQuery(id+"F4.wireOp",EDGE,"E12.0.2")])]})]});
            var Q33;
            Q33=makeQuery(id+"F9.opBoolean","INTERSECT",EDGE,{"derivedFrom":[makeQuery(id+"F1.opExtrude","CAP_FACE",FACE,{"disambiguationData":[OSD([sQuery(id+"F0.wireOp",EDGE,"E2.sketch_text.stroke-73"),sQuery(id+"F0.wireOp",EDGE,"E2.sketch_text.stroke-74"),sQuery(id+"F0.wireOp",EDGE,"E2.sketch_text.stroke-75"),sQuery(id+"F0.wireOp",EDGE,"E2.sketch_text.stroke-76"),sQuery(id+"F0.wireOp",EDGE,"E2.sketch_text.stroke-77"),sQuery(id+"F0.wireOp",EDGE,"E2.sketch_text.stroke-78"),sQuery(id+"F0.wireOp",EDGE,"E2.sketch_text.stroke-79"),sQuery(id+"F0.wireOp",EDGE,"E2.sketch_text.stroke-80"),sQuery(id+"F0.wireOp",EDGE,"E2.sketch_text.stroke-81"),sQuery(id+"F0.wireOp",EDGE,"E2.sketch_text.stroke-82"),sQuery(id+"F0.wireOp",EDGE,"E2.sketch_text.stroke-83"),sQuery(id+"F0.wireOp",EDGE,"E2.sketch_text.stroke-84"),sQuery(id+"F0.wireOp",EDGE,"E2.sketch_text.stroke-85"),sQuery(id+"F0.wireOp",EDGE,"E2.sketch_text.stroke-86"),sQuery(id+"F0.wireOp",EDGE,"E2.sketch_text.stroke-87"),sQuery(id+"F0.wireOp",EDGE,"E2.sketch_text.stroke-88"),sQuery(id+"F0.wireOp",EDGE,"E2.sketch_text.stroke-89"),sQuery(id+"F0.wireOp",EDGE,"E2.sketch_text.stroke-90"),sQuery(id+"F0.wireOp",EDGE,"E2.sketch_text.stroke-91"),sQuery(id+"F0.wireOp",EDGE,"E2.sketch_text.stroke-92"),sQuery(id+"F0.wireOp",EDGE,"E2.sketch_text.stroke-93"),sQuery(id+"F0.wireOp",EDGE,"E2.sketch_text.stroke-94"),sQuery(id+"F0.wireOp",EDGE,"E2.sketch_text.stroke-95"),sQuery(id+"F0.wireOp",EDGE,"E2.sketch_text.stroke-96"),sQuery(id+"F0.wireOp",EDGE,"E2.sketch_text.stroke-97"),sQuery(id+"F0.wireOp",EDGE,"E2.sketch_text.stroke-98")])],"isStart":true}),makeQuery(id+"F5.opExtrude","SWEPT_FACE",FACE,{"disambiguationData":[OSD([sQuery(id+"F4.wireOp",EDGE,"E12.0.2")])]})]});
            var Q34;
            Q34=makeQuery(id+"F9.opBoolean","INTERSECT",EDGE,{"derivedFrom":[makeQuery(id+"F1.opExtrude","CAP_FACE",FACE,{"disambiguationData":[OSD([sQuery(id+"F0.wireOp",EDGE,"E2.sketch_text.stroke-99"),sQuery(id+"F0.wireOp",EDGE,"E2.sketch_text.stroke-100"),sQuery(id+"F0.wireOp",EDGE,"E2.sketch_text.stroke-101"),sQuery(id+"F0.wireOp",EDGE,"E2.sketch_text.stroke-102"),sQuery(id+"F0.wireOp",EDGE,"E2.sketch_text.stroke-103"),sQuery(id+"F0.wireOp",EDGE,"E2.sketch_text.stroke-104"),sQuery(id+"F0.wireOp",EDGE,"E2.sketch_text.stroke-105"),sQuery(id+"F0.wireOp",EDGE,"E2.sketch_text.stroke-106"),sQuery(id+"F0.wireOp",EDGE,"E2.sketch_text.stroke-107"),sQuery(id+"F0.wireOp",EDGE,"E2.sketch_text.stroke-108"),sQuery(id+"F0.wireOp",EDGE,"E2.sketch_text.stroke-109"),sQuery(id+"F0.wireOp",EDGE,"E2.sketch_text.stroke-110"),sQuery(id+"F0.wireOp",EDGE,"E2.sketch_text.stroke-111"),sQuery(id+"F0.wireOp",EDGE,"E2.sketch_text.stroke-112"),sQuery(id+"F0.wireOp",EDGE,"E2.sketch_text.stroke-113"),sQuery(id+"F0.wireOp",EDGE,"E2.sketch_text.stroke-114"),sQuery(id+"F0.wireOp",EDGE,"E2.sketch_text.stroke-115")])],"isStart":true}),makeQuery(id+"F5.opExtrude","SWEPT_FACE",FACE,{"disambiguationData":[OSD([sQuery(id+"F4.wireOp",EDGE,"E12.0.2")])]})]});
            var Q35;
            Q35=makeQuery(id+"F8.opBoolean","INTERSECT",EDGE,{"derivedFrom":[makeQuery(id+"F1.opExtrude","CAP_FACE",FACE,{"disambiguationData":[OSD([sQuery(id+"F0.wireOp",EDGE,"E1.sketch_text.stroke-50"),sQuery(id+"F0.wireOp",EDGE,"E1.sketch_text.stroke-51"),sQuery(id+"F0.wireOp",EDGE,"E1.sketch_text.stroke-52"),sQuery(id+"F0.wireOp",EDGE,"E1.sketch_text.stroke-53"),sQuery(id+"F0.wireOp",EDGE,"E1.sketch_text.stroke-54"),sQuery(id+"F0.wireOp",EDGE,"E1.sketch_text.stroke-55"),sQuery(id+"F0.wireOp",EDGE,"E1.sketch_text.stroke-56"),sQuery(id+"F0.wireOp",EDGE,"E1.sketch_text.stroke-57"),sQuery(id+"F0.wireOp",EDGE,"E1.sketch_text.stroke-58"),sQuery(id+"F0.wireOp",EDGE,"E1.sketch_text.stroke-59"),sQuery(id+"F0.wireOp",EDGE,"E1.sketch_text.stroke-60"),sQuery(id+"F0.wireOp",EDGE,"E1.sketch_text.stroke-61"),sQuery(id+"F0.wireOp",EDGE,"E1.sketch_text.stroke-62"),sQuery(id+"F0.wireOp",EDGE,"E1.sketch_text.stroke-63"),sQuery(id+"F0.wireOp",EDGE,"E1.sketch_text.stroke-64"),sQuery(id+"F0.wireOp",EDGE,"E1.sketch_text.stroke-65"),sQuery(id+"F0.wireOp",EDGE,"E1.sketch_text.stroke-66"),sQuery(id+"F0.wireOp",EDGE,"E1.sketch_text.stroke-67"),sQuery(id+"F0.wireOp",EDGE,"E1.sketch_text.stroke-68"),sQuery(id+"F0.wireOp",EDGE,"E1.sketch_text.stroke-69")])],"isStart":true}),makeQuery(id+"F5.opExtrude","SWEPT_FACE",FACE,{"disambiguationData":[OSD([sQuery(id+"F4.wireOp",EDGE,"E11.0.2")])]})]});
            var Q36;
            Q36=makeQuery(id+"F8.opBoolean","INTERSECT",EDGE,{"derivedFrom":[makeQuery(id+"F1.opExtrude","CAP_FACE",FACE,{"disambiguationData":[OSD([sQuery(id+"F0.wireOp",EDGE,"E1.sketch_text.stroke-37"),sQuery(id+"F0.wireOp",EDGE,"E1.sketch_text.stroke-38"),sQuery(id+"F0.wireOp",EDGE,"E1.sketch_text.stroke-39"),sQuery(id+"F0.wireOp",EDGE,"E1.sketch_text.stroke-40"),sQuery(id+"F0.wireOp",EDGE,"E1.sketch_text.stroke-41"),sQuery(id+"F0.wireOp",EDGE,"E1.sketch_text.stroke-42"),sQuery(id+"F0.wireOp",EDGE,"E1.sketch_text.stroke-43"),sQuery(id+"F0.wireOp",EDGE,"E1.sketch_text.stroke-44"),sQuery(id+"F0.wireOp",EDGE,"E1.sketch_text.stroke-45"),sQuery(id+"F0.wireOp",EDGE,"E1.sketch_text.stroke-46"),sQuery(id+"F0.wireOp",EDGE,"E1.sketch_text.stroke-47"),sQuery(id+"F0.wireOp",EDGE,"E1.sketch_text.stroke-48"),sQuery(id+"F0.wireOp",EDGE,"E1.sketch_text.stroke-49")])],"isStart":true}),makeQuery(id+"F5.opExtrude","SWEPT_FACE",FACE,{"disambiguationData":[OSD([sQuery(id+"F4.wireOp",EDGE,"E11.0.2")])]})]});
            var Q37;
            Q37=makeQuery(id+"F8.opBoolean","INTERSECT",EDGE,{"derivedFrom":[makeQuery(id+"F1.opExtrude","CAP_FACE",FACE,{"disambiguationData":[OSD([sQuery(id+"F0.wireOp",EDGE,"E1.sketch_text.stroke-25"),sQuery(id+"F0.wireOp",EDGE,"E1.sketch_text.stroke-26"),sQuery(id+"F0.wireOp",EDGE,"E1.sketch_text.stroke-27"),sQuery(id+"F0.wireOp",EDGE,"E1.sketch_text.stroke-28"),sQuery(id+"F0.wireOp",EDGE,"E1.sketch_text.stroke-29"),sQuery(id+"F0.wireOp",EDGE,"E1.sketch_text.stroke-30"),sQuery(id+"F0.wireOp",EDGE,"E1.sketch_text.stroke-31"),sQuery(id+"F0.wireOp",EDGE,"E1.sketch_text.stroke-32"),sQuery(id+"F0.wireOp",EDGE,"E1.sketch_text.stroke-33"),sQuery(id+"F0.wireOp",EDGE,"E1.sketch_text.stroke-34"),sQuery(id+"F0.wireOp",EDGE,"E1.sketch_text.stroke-35"),sQuery(id+"F0.wireOp",EDGE,"E1.sketch_text.stroke-36")])],"isStart":true}),makeQuery(id+"F5.opExtrude","SWEPT_FACE",FACE,{"disambiguationData":[OSD([sQuery(id+"F4.wireOp",EDGE,"E11.0.2")])]})]});
            var Q38;
            Q38=makeQuery(id+"F10.opBoolean","INTERSECT",EDGE,{"derivedFrom":[makeQuery(id+"F1.opExtrude","CAP_FACE",FACE,{"disambiguationData":[OSD([sQuery(id+"F0.wireOp",EDGE,"E3.sketch_text.stroke-152"),sQuery(id+"F0.wireOp",EDGE,"E3.sketch_text.stroke-153"),sQuery(id+"F0.wireOp",EDGE,"E3.sketch_text.stroke-154"),sQuery(id+"F0.wireOp",EDGE,"E3.sketch_text.stroke-155")])],"isStart":true}),makeQuery(id+"F5.opExtrude","SWEPT_FACE",FACE,{"disambiguationData":[OSD([sQuery(id+"F4.wireOp",EDGE,"E13.0.0")])]})]});
            var Q39;
            Q39=makeQuery(id+"F10.opBoolean","INTERSECT",EDGE,{"derivedFrom":[makeQuery(id+"F1.opExtrude","CAP_FACE",FACE,{"disambiguationData":[OSD([sQuery(id+"F0.wireOp",EDGE,"E3.sketch_text.stroke-127"),sQuery(id+"F0.wireOp",EDGE,"E3.sketch_text.stroke-128"),sQuery(id+"F0.wireOp",EDGE,"E3.sketch_text.stroke-129"),sQuery(id+"F0.wireOp",EDGE,"E3.sketch_text.stroke-130"),sQuery(id+"F0.wireOp",EDGE,"E3.sketch_text.stroke-131"),sQuery(id+"F0.wireOp",EDGE,"E3.sketch_text.stroke-132"),sQuery(id+"F0.wireOp",EDGE,"E3.sketch_text.stroke-133"),sQuery(id+"F0.wireOp",EDGE,"E3.sketch_text.stroke-134"),sQuery(id+"F0.wireOp",EDGE,"E3.sketch_text.stroke-135"),sQuery(id+"F0.wireOp",EDGE,"E3.sketch_text.stroke-136"),sQuery(id+"F0.wireOp",EDGE,"E3.sketch_text.stroke-137"),sQuery(id+"F0.wireOp",EDGE,"E3.sketch_text.stroke-138"),sQuery(id+"F0.wireOp",EDGE,"E3.sketch_text.stroke-139"),sQuery(id+"F0.wireOp",EDGE,"E3.sketch_text.stroke-140"),sQuery(id+"F0.wireOp",EDGE,"E3.sketch_text.stroke-141"),sQuery(id+"F0.wireOp",EDGE,"E3.sketch_text.stroke-142"),sQuery(id+"F0.wireOp",EDGE,"E3.sketch_text.stroke-143"),sQuery(id+"F0.wireOp",EDGE,"E3.sketch_text.stroke-144"),sQuery(id+"F0.wireOp",EDGE,"E3.sketch_text.stroke-145"),sQuery(id+"F0.wireOp",EDGE,"E3.sketch_text.stroke-146"),sQuery(id+"F0.wireOp",EDGE,"E3.sketch_text.stroke-147"),sQuery(id+"F0.wireOp",EDGE,"E3.sketch_text.stroke-148"),sQuery(id+"F0.wireOp",EDGE,"E3.sketch_text.stroke-149"),sQuery(id+"F0.wireOp",EDGE,"E3.sketch_text.stroke-150"),sQuery(id+"F0.wireOp",EDGE,"E3.sketch_text.stroke-151")])],"isStart":true}),makeQuery(id+"F5.opExtrude","SWEPT_FACE",FACE,{"disambiguationData":[OSD([sQuery(id+"F4.wireOp",EDGE,"E13.0.0")])]})]});
            var Q40;
            Q40=makeQuery(id+"F10.opBoolean","INTERSECT",EDGE,{"derivedFrom":[makeQuery(id+"F1.opExtrude","CAP_FACE",FACE,{"disambiguationData":[OSD([sQuery(id+"F0.wireOp",EDGE,"E3.sketch_text.stroke-119"),sQuery(id+"F0.wireOp",EDGE,"E3.sketch_text.stroke-120"),sQuery(id+"F0.wireOp",EDGE,"E3.sketch_text.stroke-121"),sQuery(id+"F0.wireOp",EDGE,"E3.sketch_text.stroke-122"),sQuery(id+"F0.wireOp",EDGE,"E3.sketch_text.stroke-123"),sQuery(id+"F0.wireOp",EDGE,"E3.sketch_text.stroke-124"),sQuery(id+"F0.wireOp",EDGE,"E3.sketch_text.stroke-125"),sQuery(id+"F0.wireOp",EDGE,"E3.sketch_text.stroke-126")])],"isStart":true}),makeQuery(id+"F5.opExtrude","SWEPT_FACE",FACE,{"disambiguationData":[OSD([sQuery(id+"F4.wireOp",EDGE,"E13.0.0")])]})]});
            var Q41;
            Q41=makeQuery(id+"F11.opBoolean","INTERSECT",EDGE,{"derivedFrom":[makeQuery(id+"F1.opExtrude","CAP_FACE",FACE,{"disambiguationData":[OSD([sQuery(id+"F0.wireOp",EDGE,"E4.sketch_text.stroke-111"),sQuery(id+"F0.wireOp",EDGE,"E4.sketch_text.stroke-112"),sQuery(id+"F0.wireOp",EDGE,"E4.sketch_text.stroke-113"),sQuery(id+"F0.wireOp",EDGE,"E4.sketch_text.stroke-114"),sQuery(id+"F0.wireOp",EDGE,"E4.sketch_text.stroke-115"),sQuery(id+"F0.wireOp",EDGE,"E4.sketch_text.stroke-116"),sQuery(id+"F0.wireOp",EDGE,"E4.sketch_text.stroke-117"),sQuery(id+"F0.wireOp",EDGE,"E4.sketch_text.stroke-118")])],"isStart":true}),makeQuery(id+"F5.opExtrude","SWEPT_FACE",FACE,{"disambiguationData":[OSD([sQuery(id+"F4.wireOp",EDGE,"E14.0.0")])]})]});
            var Q42;
            Q42=makeQuery(id+"F11.opBoolean","INTERSECT",EDGE,{"derivedFrom":[makeQuery(id+"F1.opExtrude","CAP_FACE",FACE,{"disambiguationData":[OSD([sQuery(id+"F0.wireOp",EDGE,"E4.sketch_text.stroke-119"),sQuery(id+"F0.wireOp",EDGE,"E4.sketch_text.stroke-120"),sQuery(id+"F0.wireOp",EDGE,"E4.sketch_text.stroke-121"),sQuery(id+"F0.wireOp",EDGE,"E4.sketch_text.stroke-122"),sQuery(id+"F0.wireOp",EDGE,"E4.sketch_text.stroke-123"),sQuery(id+"F0.wireOp",EDGE,"E4.sketch_text.stroke-124"),sQuery(id+"F0.wireOp",EDGE,"E4.sketch_text.stroke-125"),sQuery(id+"F0.wireOp",EDGE,"E4.sketch_text.stroke-126"),sQuery(id+"F0.wireOp",EDGE,"E4.sketch_text.stroke-127"),sQuery(id+"F0.wireOp",EDGE,"E4.sketch_text.stroke-128"),sQuery(id+"F0.wireOp",EDGE,"E4.sketch_text.stroke-129"),sQuery(id+"F0.wireOp",EDGE,"E4.sketch_text.stroke-130"),sQuery(id+"F0.wireOp",EDGE,"E4.sketch_text.stroke-131"),sQuery(id+"F0.wireOp",EDGE,"E4.sketch_text.stroke-132"),sQuery(id+"F0.wireOp",EDGE,"E4.sketch_text.stroke-133"),sQuery(id+"F0.wireOp",EDGE,"E4.sketch_text.stroke-134"),sQuery(id+"F0.wireOp",EDGE,"E4.sketch_text.stroke-135"),sQuery(id+"F0.wireOp",EDGE,"E4.sketch_text.stroke-136"),sQuery(id+"F0.wireOp",EDGE,"E4.sketch_text.stroke-137"),sQuery(id+"F0.wireOp",EDGE,"E4.sketch_text.stroke-138"),sQuery(id+"F0.wireOp",EDGE,"E4.sketch_text.stroke-139"),sQuery(id+"F0.wireOp",EDGE,"E4.sketch_text.stroke-140"),sQuery(id+"F0.wireOp",EDGE,"E4.sketch_text.stroke-141"),sQuery(id+"F0.wireOp",EDGE,"E4.sketch_text.stroke-142"),sQuery(id+"F0.wireOp",EDGE,"E4.sketch_text.stroke-143")])],"isStart":true}),makeQuery(id+"F5.opExtrude","SWEPT_FACE",FACE,{"disambiguationData":[OSD([sQuery(id+"F4.wireOp",EDGE,"E14.0.0")])]})]});
            var Q43;
            Q43=makeQuery(id+"F11.opBoolean","INTERSECT",EDGE,{"derivedFrom":[makeQuery(id+"F1.opExtrude","CAP_FACE",FACE,{"disambiguationData":[OSD([sQuery(id+"F0.wireOp",EDGE,"E4.sketch_text.stroke-29"),sQuery(id+"F0.wireOp",EDGE,"E4.sketch_text.stroke-30"),sQuery(id+"F0.wireOp",EDGE,"E4.sketch_text.stroke-31"),sQuery(id+"F0.wireOp",EDGE,"E4.sketch_text.stroke-32")])],"isStart":true}),makeQuery(id+"F5.opExtrude","SWEPT_FACE",FACE,{"disambiguationData":[OSD([sQuery(id+"F4.wireOp",EDGE,"E14.0.0")])]})]});
            var Q44;
            Q44=makeQuery(id+"F11.opBoolean","INTERSECT",EDGE,{"derivedFrom":[makeQuery(id+"F1.opExtrude","CAP_FACE",FACE,{"disambiguationData":[OSD([sQuery(id+"F0.wireOp",EDGE,"E4.sketch_text.stroke-0"),sQuery(id+"F0.wireOp",EDGE,"E4.sketch_text.stroke-1"),sQuery(id+"F0.wireOp",EDGE,"E4.sketch_text.stroke-2"),sQuery(id+"F0.wireOp",EDGE,"E4.sketch_text.stroke-3"),sQuery(id+"F0.wireOp",EDGE,"E4.sketch_text.stroke-4")])],"isStart":true}),makeQuery(id+"F5.opExtrude","SWEPT_FACE",FACE,{"disambiguationData":[OSD([sQuery(id+"F4.wireOp",EDGE,"E14.0.0")])]})]});
            var Q45;
            Q45=makeQuery(id+"F11.opBoolean","INTERSECT",EDGE,{"derivedFrom":[makeQuery(id+"F1.opExtrude","CAP_FACE",FACE,{"disambiguationData":[OSD([sQuery(id+"F0.wireOp",EDGE,"E4.sketch_text.stroke-11"),sQuery(id+"F0.wireOp",EDGE,"E4.sketch_text.stroke-12"),sQuery(id+"F0.wireOp",EDGE,"E4.sketch_text.stroke-13"),sQuery(id+"F0.wireOp",EDGE,"E4.sketch_text.stroke-14"),sQuery(id+"F0.wireOp",EDGE,"E4.sketch_text.stroke-15"),sQuery(id+"F0.wireOp",EDGE,"E4.sketch_text.stroke-16"),sQuery(id+"F0.wireOp",EDGE,"E4.sketch_text.stroke-17"),sQuery(id+"F0.wireOp",EDGE,"E4.sketch_text.stroke-18"),sQuery(id+"F0.wireOp",EDGE,"E4.sketch_text.stroke-19"),sQuery(id+"F0.wireOp",EDGE,"E4.sketch_text.stroke-20"),sQuery(id+"F0.wireOp",EDGE,"E4.sketch_text.stroke-21"),sQuery(id+"F0.wireOp",EDGE,"E4.sketch_text.stroke-22"),sQuery(id+"F0.wireOp",EDGE,"E4.sketch_text.stroke-23"),sQuery(id+"F0.wireOp",EDGE,"E4.sketch_text.stroke-24"),sQuery(id+"F0.wireOp",EDGE,"E4.sketch_text.stroke-25"),sQuery(id+"F0.wireOp",EDGE,"E4.sketch_text.stroke-26"),sQuery(id+"F0.wireOp",EDGE,"E4.sketch_text.stroke-27"),sQuery(id+"F0.wireOp",EDGE,"E4.sketch_text.stroke-28")])],"isStart":true}),makeQuery(id+"F5.opExtrude","SWEPT_FACE",FACE,{"disambiguationData":[OSD([sQuery(id+"F4.wireOp",EDGE,"E14.0.0")])]})]});
            var Q46;
            Q46=makeQuery(id+"F10.opBoolean","INTERSECT",EDGE,{"derivedFrom":[makeQuery(id+"F1.opExtrude","CAP_FACE",FACE,{"disambiguationData":[OSD([sQuery(id+"F0.wireOp",EDGE,"E3.sketch_text.stroke-0"),sQuery(id+"F0.wireOp",EDGE,"E3.sketch_text.stroke-1"),sQuery(id+"F0.wireOp",EDGE,"E3.sketch_text.stroke-2"),sQuery(id+"F0.wireOp",EDGE,"E3.sketch_text.stroke-3"),sQuery(id+"F0.wireOp",EDGE,"E3.sketch_text.stroke-4"),sQuery(id+"F0.wireOp",EDGE,"E3.sketch_text.stroke-5"),sQuery(id+"F0.wireOp",EDGE,"E3.sketch_text.stroke-6"),sQuery(id+"F0.wireOp",EDGE,"E3.sketch_text.stroke-7"),sQuery(id+"F0.wireOp",EDGE,"E3.sketch_text.stroke-8"),sQuery(id+"F0.wireOp",EDGE,"E3.sketch_text.stroke-9"),sQuery(id+"F0.wireOp",EDGE,"E3.sketch_text.stroke-10")])],"isStart":true}),makeQuery(id+"F5.opExtrude","SWEPT_FACE",FACE,{"disambiguationData":[OSD([sQuery(id+"F4.wireOp",EDGE,"E13.0.0")])]})]});
            var Q47;
            Q47=makeQuery(id+"F10.opBoolean","INTERSECT",EDGE,{"derivedFrom":[makeQuery(id+"F1.opExtrude","CAP_FACE",FACE,{"disambiguationData":[OSD([sQuery(id+"F0.wireOp",EDGE,"E3.sketch_text.stroke-11"),sQuery(id+"F0.wireOp",EDGE,"E3.sketch_text.stroke-12"),sQuery(id+"F0.wireOp",EDGE,"E3.sketch_text.stroke-13"),sQuery(id+"F0.wireOp",EDGE,"E3.sketch_text.stroke-14"),sQuery(id+"F0.wireOp",EDGE,"E3.sketch_text.stroke-15"),sQuery(id+"F0.wireOp",EDGE,"E3.sketch_text.stroke-16"),sQuery(id+"F0.wireOp",EDGE,"E3.sketch_text.stroke-17"),sQuery(id+"F0.wireOp",EDGE,"E3.sketch_text.stroke-18"),sQuery(id+"F0.wireOp",EDGE,"E3.sketch_text.stroke-19"),sQuery(id+"F0.wireOp",EDGE,"E3.sketch_text.stroke-20"),sQuery(id+"F0.wireOp",EDGE,"E3.sketch_text.stroke-21"),sQuery(id+"F0.wireOp",EDGE,"E3.sketch_text.stroke-22"),sQuery(id+"F0.wireOp",EDGE,"E3.sketch_text.stroke-23"),sQuery(id+"F0.wireOp",EDGE,"E3.sketch_text.stroke-24")])],"isStart":true}),makeQuery(id+"F5.opExtrude","SWEPT_FACE",FACE,{"disambiguationData":[OSD([sQuery(id+"F4.wireOp",EDGE,"E13.0.0")])]})]});
            var Q48;
            Q48=makeQuery(id+"F10.opBoolean","INTERSECT",EDGE,{"derivedFrom":[makeQuery(id+"F1.opExtrude","CAP_FACE",FACE,{"disambiguationData":[OSD([sQuery(id+"F0.wireOp",EDGE,"E3.sketch_text.stroke-37"),sQuery(id+"F0.wireOp",EDGE,"E3.sketch_text.stroke-38"),sQuery(id+"F0.wireOp",EDGE,"E3.sketch_text.stroke-39"),sQuery(id+"F0.wireOp",EDGE,"E3.sketch_text.stroke-40"),sQuery(id+"F0.wireOp",EDGE,"E3.sketch_text.stroke-41"),sQuery(id+"F0.wireOp",EDGE,"E3.sketch_text.stroke-42"),sQuery(id+"F0.wireOp",EDGE,"E3.sketch_text.stroke-43"),sQuery(id+"F0.wireOp",EDGE,"E3.sketch_text.stroke-44"),sQuery(id+"F0.wireOp",EDGE,"E3.sketch_text.stroke-45"),sQuery(id+"F0.wireOp",EDGE,"E3.sketch_text.stroke-46"),sQuery(id+"F0.wireOp",EDGE,"E3.sketch_text.stroke-47"),sQuery(id+"F0.wireOp",EDGE,"E3.sketch_text.stroke-48"),sQuery(id+"F0.wireOp",EDGE,"E3.sketch_text.stroke-49")])],"isStart":true}),makeQuery(id+"F5.opExtrude","SWEPT_FACE",FACE,{"disambiguationData":[OSD([sQuery(id+"F4.wireOp",EDGE,"E13.0.2")])]})]});
            var Q49;
            Q49=makeQuery(id+"F10.opBoolean","INTERSECT",EDGE,{"derivedFrom":[makeQuery(id+"F1.opExtrude","CAP_FACE",FACE,{"disambiguationData":[OSD([sQuery(id+"F0.wireOp",EDGE,"E3.sketch_text.stroke-25"),sQuery(id+"F0.wireOp",EDGE,"E3.sketch_text.stroke-26"),sQuery(id+"F0.wireOp",EDGE,"E3.sketch_text.stroke-27"),sQuery(id+"F0.wireOp",EDGE,"E3.sketch_text.stroke-28"),sQuery(id+"F0.wireOp",EDGE,"E3.sketch_text.stroke-29"),sQuery(id+"F0.wireOp",EDGE,"E3.sketch_text.stroke-30"),sQuery(id+"F0.wireOp",EDGE,"E3.sketch_text.stroke-31"),sQuery(id+"F0.wireOp",EDGE,"E3.sketch_text.stroke-32"),sQuery(id+"F0.wireOp",EDGE,"E3.sketch_text.stroke-33"),sQuery(id+"F0.wireOp",EDGE,"E3.sketch_text.stroke-34"),sQuery(id+"F0.wireOp",EDGE,"E3.sketch_text.stroke-35"),sQuery(id+"F0.wireOp",EDGE,"E3.sketch_text.stroke-36")])],"isStart":true}),makeQuery(id+"F5.opExtrude","SWEPT_FACE",FACE,{"disambiguationData":[OSD([sQuery(id+"F4.wireOp",EDGE,"E13.0.2")])]})]});
            var Q50;
            Q50=makeQuery(id+"F10.opBoolean","INTERSECT",EDGE,{"derivedFrom":[makeQuery(id+"F1.opExtrude","CAP_FACE",FACE,{"disambiguationData":[OSD([sQuery(id+"F0.wireOp",EDGE,"E3.sketch_text.stroke-50"),sQuery(id+"F0.wireOp",EDGE,"E3.sketch_text.stroke-51"),sQuery(id+"F0.wireOp",EDGE,"E3.sketch_text.stroke-52"),sQuery(id+"F0.wireOp",EDGE,"E3.sketch_text.stroke-53"),sQuery(id+"F0.wireOp",EDGE,"E3.sketch_text.stroke-54"),sQuery(id+"F0.wireOp",EDGE,"E3.sketch_text.stroke-55"),sQuery(id+"F0.wireOp",EDGE,"E3.sketch_text.stroke-56"),sQuery(id+"F0.wireOp",EDGE,"E3.sketch_text.stroke-57"),sQuery(id+"F0.wireOp",EDGE,"E3.sketch_text.stroke-58"),sQuery(id+"F0.wireOp",EDGE,"E3.sketch_text.stroke-59"),sQuery(id+"F0.wireOp",EDGE,"E3.sketch_text.stroke-60"),sQuery(id+"F0.wireOp",EDGE,"E3.sketch_text.stroke-61"),sQuery(id+"F0.wireOp",EDGE,"E3.sketch_text.stroke-62"),sQuery(id+"F0.wireOp",EDGE,"E3.sketch_text.stroke-63"),sQuery(id+"F0.wireOp",EDGE,"E3.sketch_text.stroke-64"),sQuery(id+"F0.wireOp",EDGE,"E3.sketch_text.stroke-65"),sQuery(id+"F0.wireOp",EDGE,"E3.sketch_text.stroke-66"),sQuery(id+"F0.wireOp",EDGE,"E3.sketch_text.stroke-67"),sQuery(id+"F0.wireOp",EDGE,"E3.sketch_text.stroke-68")])],"isStart":true}),makeQuery(id+"F5.opExtrude","SWEPT_FACE",FACE,{"disambiguationData":[OSD([sQuery(id+"F4.wireOp",EDGE,"E13.0.2")])]})]});
            var Q51;
            Q51=makeQuery(id+"F10.opBoolean","INTERSECT",EDGE,{"disambiguationData":[OD(1.0)],"derivedFrom":[makeQuery(id+"F1.opExtrude","CAP_FACE",FACE,{"disambiguationData":[OSD([sQuery(id+"F0.wireOp",EDGE,"E3.sketch_text.stroke-69"),sQuery(id+"F0.wireOp",EDGE,"E3.sketch_text.stroke-70"),sQuery(id+"F0.wireOp",EDGE,"E3.sketch_text.stroke-71"),sQuery(id+"F0.wireOp",EDGE,"E3.sketch_text.stroke-72"),sQuery(id+"F0.wireOp",EDGE,"E3.sketch_text.stroke-73"),sQuery(id+"F0.wireOp",EDGE,"E3.sketch_text.stroke-74"),sQuery(id+"F0.wireOp",EDGE,"E3.sketch_text.stroke-75"),sQuery(id+"F0.wireOp",EDGE,"E3.sketch_text.stroke-76"),sQuery(id+"F0.wireOp",EDGE,"E3.sketch_text.stroke-77"),sQuery(id+"F0.wireOp",EDGE,"E3.sketch_text.stroke-78"),sQuery(id+"F0.wireOp",EDGE,"E3.sketch_text.stroke-79"),sQuery(id+"F0.wireOp",EDGE,"E3.sketch_text.stroke-80"),sQuery(id+"F0.wireOp",EDGE,"E3.sketch_text.stroke-81"),sQuery(id+"F0.wireOp",EDGE,"E3.sketch_text.stroke-82"),sQuery(id+"F0.wireOp",EDGE,"E3.sketch_text.stroke-83"),sQuery(id+"F0.wireOp",EDGE,"E3.sketch_text.stroke-84"),sQuery(id+"F0.wireOp",EDGE,"E3.sketch_text.stroke-85"),sQuery(id+"F0.wireOp",EDGE,"E3.sketch_text.stroke-86"),sQuery(id+"F0.wireOp",EDGE,"E3.sketch_text.stroke-87"),sQuery(id+"F0.wireOp",EDGE,"E3.sketch_text.stroke-88"),sQuery(id+"F0.wireOp",EDGE,"E3.sketch_text.stroke-89"),sQuery(id+"F0.wireOp",EDGE,"E3.sketch_text.stroke-90"),sQuery(id+"F0.wireOp",EDGE,"E3.sketch_text.stroke-91"),sQuery(id+"F0.wireOp",EDGE,"E3.sketch_text.stroke-92"),sQuery(id+"F0.wireOp",EDGE,"E3.sketch_text.stroke-93"),sQuery(id+"F0.wireOp",EDGE,"E3.sketch_text.stroke-94"),sQuery(id+"F0.wireOp",EDGE,"E3.sketch_text.stroke-95"),sQuery(id+"F0.wireOp",EDGE,"E3.sketch_text.stroke-96"),sQuery(id+"F0.wireOp",EDGE,"E3.sketch_text.stroke-97"),sQuery(id+"F0.wireOp",EDGE,"E3.sketch_text.stroke-98"),sQuery(id+"F0.wireOp",EDGE,"E3.sketch_text.stroke-99"),sQuery(id+"F0.wireOp",EDGE,"E3.sketch_text.stroke-100"),sQuery(id+"F0.wireOp",EDGE,"E3.sketch_text.stroke-101"),sQuery(id+"F0.wireOp",EDGE,"E3.sketch_text.stroke-102"),sQuery(id+"F0.wireOp",EDGE,"E3.sketch_text.stroke-103"),sQuery(id+"F0.wireOp",EDGE,"E3.sketch_text.stroke-104")])],"isStart":true}),makeQuery(id+"F5.opExtrude","SWEPT_FACE",FACE,{"disambiguationData":[OSD([sQuery(id+"F4.wireOp",EDGE,"E13.0.2")])]})]});
            var Q52;
            Q52=makeQuery(id+"F10.opBoolean","INTERSECT",EDGE,{"disambiguationData":[OD(0.0)],"derivedFrom":[makeQuery(id+"F1.opExtrude","CAP_FACE",FACE,{"disambiguationData":[OSD([sQuery(id+"F0.wireOp",EDGE,"E3.sketch_text.stroke-69"),sQuery(id+"F0.wireOp",EDGE,"E3.sketch_text.stroke-70"),sQuery(id+"F0.wireOp",EDGE,"E3.sketch_text.stroke-71"),sQuery(id+"F0.wireOp",EDGE,"E3.sketch_text.stroke-72"),sQuery(id+"F0.wireOp",EDGE,"E3.sketch_text.stroke-73"),sQuery(id+"F0.wireOp",EDGE,"E3.sketch_text.stroke-74"),sQuery(id+"F0.wireOp",EDGE,"E3.sketch_text.stroke-75"),sQuery(id+"F0.wireOp",EDGE,"E3.sketch_text.stroke-76"),sQuery(id+"F0.wireOp",EDGE,"E3.sketch_text.stroke-77"),sQuery(id+"F0.wireOp",EDGE,"E3.sketch_text.stroke-78"),sQuery(id+"F0.wireOp",EDGE,"E3.sketch_text.stroke-79"),sQuery(id+"F0.wireOp",EDGE,"E3.sketch_text.stroke-80"),sQuery(id+"F0.wireOp",EDGE,"E3.sketch_text.stroke-81"),sQuery(id+"F0.wireOp",EDGE,"E3.sketch_text.stroke-82"),sQuery(id+"F0.wireOp",EDGE,"E3.sketch_text.stroke-83"),sQuery(id+"F0.wireOp",EDGE,"E3.sketch_text.stroke-84"),sQuery(id+"F0.wireOp",EDGE,"E3.sketch_text.stroke-85"),sQuery(id+"F0.wireOp",EDGE,"E3.sketch_text.stroke-86"),sQuery(id+"F0.wireOp",EDGE,"E3.sketch_text.stroke-87"),sQuery(id+"F0.wireOp",EDGE,"E3.sketch_text.stroke-88"),sQuery(id+"F0.wireOp",EDGE,"E3.sketch_text.stroke-89"),sQuery(id+"F0.wireOp",EDGE,"E3.sketch_text.stroke-90"),sQuery(id+"F0.wireOp",EDGE,"E3.sketch_text.stroke-91"),sQuery(id+"F0.wireOp",EDGE,"E3.sketch_text.stroke-92"),sQuery(id+"F0.wireOp",EDGE,"E3.sketch_text.stroke-93"),sQuery(id+"F0.wireOp",EDGE,"E3.sketch_text.stroke-94"),sQuery(id+"F0.wireOp",EDGE,"E3.sketch_text.stroke-95"),sQuery(id+"F0.wireOp",EDGE,"E3.sketch_text.stroke-96"),sQuery(id+"F0.wireOp",EDGE,"E3.sketch_text.stroke-97"),sQuery(id+"F0.wireOp",EDGE,"E3.sketch_text.stroke-98"),sQuery(id+"F0.wireOp",EDGE,"E3.sketch_text.stroke-99"),sQuery(id+"F0.wireOp",EDGE,"E3.sketch_text.stroke-100"),sQuery(id+"F0.wireOp",EDGE,"E3.sketch_text.stroke-101"),sQuery(id+"F0.wireOp",EDGE,"E3.sketch_text.stroke-102"),sQuery(id+"F0.wireOp",EDGE,"E3.sketch_text.stroke-103"),sQuery(id+"F0.wireOp",EDGE,"E3.sketch_text.stroke-104")])],"isStart":true}),makeQuery(id+"F5.opExtrude","SWEPT_FACE",FACE,{"disambiguationData":[OSD([sQuery(id+"F4.wireOp",EDGE,"E13.0.2")])]})]});
            var Q53;
            Q53=makeQuery(id+"F10.opBoolean","INTERSECT",EDGE,{"derivedFrom":[makeQuery(id+"F1.opExtrude","CAP_FACE",FACE,{"disambiguationData":[OSD([sQuery(id+"F0.wireOp",EDGE,"E3.sketch_text.stroke-105"),sQuery(id+"F0.wireOp",EDGE,"E3.sketch_text.stroke-106"),sQuery(id+"F0.wireOp",EDGE,"E3.sketch_text.stroke-107"),sQuery(id+"F0.wireOp",EDGE,"E3.sketch_text.stroke-108"),sQuery(id+"F0.wireOp",EDGE,"E3.sketch_text.stroke-109")])],"isStart":true}),makeQuery(id+"F5.opExtrude","SWEPT_FACE",FACE,{"disambiguationData":[OSD([sQuery(id+"F4.wireOp",EDGE,"E13.0.2")])]})]});
            var Q54;
            Q54=makeQuery(id+"F10.opBoolean","INTERSECT",EDGE,{"derivedFrom":[makeQuery(id+"F1.opExtrude","CAP_FACE",FACE,{"disambiguationData":[OSD([sQuery(id+"F0.wireOp",EDGE,"E3.sketch_text.stroke-110"),sQuery(id+"F0.wireOp",EDGE,"E3.sketch_text.stroke-111"),sQuery(id+"F0.wireOp",EDGE,"E3.sketch_text.stroke-112"),sQuery(id+"F0.wireOp",EDGE,"E3.sketch_text.stroke-113"),sQuery(id+"F0.wireOp",EDGE,"E3.sketch_text.stroke-114")])],"isStart":true}),makeQuery(id+"F5.opExtrude","SWEPT_FACE",FACE,{"disambiguationData":[OSD([sQuery(id+"F4.wireOp",EDGE,"E13.0.2")])]})]});
            var Q55;
            Q55=makeQuery(id+"F10.opBoolean","INTERSECT",EDGE,{"derivedFrom":[makeQuery(id+"F1.opExtrude","CAP_FACE",FACE,{"disambiguationData":[OSD([sQuery(id+"F0.wireOp",EDGE,"E3.sketch_text.stroke-115"),sQuery(id+"F0.wireOp",EDGE,"E3.sketch_text.stroke-116"),sQuery(id+"F0.wireOp",EDGE,"E3.sketch_text.stroke-117"),sQuery(id+"F0.wireOp",EDGE,"E3.sketch_text.stroke-118")])],"isStart":true}),makeQuery(id+"F5.opExtrude","SWEPT_FACE",FACE,{"disambiguationData":[OSD([sQuery(id+"F4.wireOp",EDGE,"E13.0.2")])]})]});
            var Q56;
            Q56=makeQuery(id+"F10.opBoolean","INTERSECT",EDGE,{"derivedFrom":[makeQuery(id+"F1.opExtrude","CAP_FACE",FACE,{"disambiguationData":[OSD([sQuery(id+"F0.wireOp",EDGE,"E3.sketch_text.stroke-127"),sQuery(id+"F0.wireOp",EDGE,"E3.sketch_text.stroke-128"),sQuery(id+"F0.wireOp",EDGE,"E3.sketch_text.stroke-129"),sQuery(id+"F0.wireOp",EDGE,"E3.sketch_text.stroke-130"),sQuery(id+"F0.wireOp",EDGE,"E3.sketch_text.stroke-131"),sQuery(id+"F0.wireOp",EDGE,"E3.sketch_text.stroke-132"),sQuery(id+"F0.wireOp",EDGE,"E3.sketch_text.stroke-133"),sQuery(id+"F0.wireOp",EDGE,"E3.sketch_text.stroke-134"),sQuery(id+"F0.wireOp",EDGE,"E3.sketch_text.stroke-135"),sQuery(id+"F0.wireOp",EDGE,"E3.sketch_text.stroke-136"),sQuery(id+"F0.wireOp",EDGE,"E3.sketch_text.stroke-137"),sQuery(id+"F0.wireOp",EDGE,"E3.sketch_text.stroke-138"),sQuery(id+"F0.wireOp",EDGE,"E3.sketch_text.stroke-139"),sQuery(id+"F0.wireOp",EDGE,"E3.sketch_text.stroke-140"),sQuery(id+"F0.wireOp",EDGE,"E3.sketch_text.stroke-141"),sQuery(id+"F0.wireOp",EDGE,"E3.sketch_text.stroke-142"),sQuery(id+"F0.wireOp",EDGE,"E3.sketch_text.stroke-143"),sQuery(id+"F0.wireOp",EDGE,"E3.sketch_text.stroke-144"),sQuery(id+"F0.wireOp",EDGE,"E3.sketch_text.stroke-145"),sQuery(id+"F0.wireOp",EDGE,"E3.sketch_text.stroke-146"),sQuery(id+"F0.wireOp",EDGE,"E3.sketch_text.stroke-147"),sQuery(id+"F0.wireOp",EDGE,"E3.sketch_text.stroke-148"),sQuery(id+"F0.wireOp",EDGE,"E3.sketch_text.stroke-149"),sQuery(id+"F0.wireOp",EDGE,"E3.sketch_text.stroke-150"),sQuery(id+"F0.wireOp",EDGE,"E3.sketch_text.stroke-151")])],"isStart":true}),makeQuery(id+"F5.opExtrude","SWEPT_FACE",FACE,{"disambiguationData":[OSD([sQuery(id+"F4.wireOp",EDGE,"E13.0.2")])]})]});
            var Q57;
            Q57=makeQuery(id+"F10.opBoolean","INTERSECT",EDGE,{"derivedFrom":[makeQuery(id+"F1.opExtrude","CAP_FACE",FACE,{"disambiguationData":[OSD([sQuery(id+"F0.wireOp",EDGE,"E3.sketch_text.stroke-152"),sQuery(id+"F0.wireOp",EDGE,"E3.sketch_text.stroke-153"),sQuery(id+"F0.wireOp",EDGE,"E3.sketch_text.stroke-154"),sQuery(id+"F0.wireOp",EDGE,"E3.sketch_text.stroke-155")])],"isStart":true}),makeQuery(id+"F5.opExtrude","SWEPT_FACE",FACE,{"disambiguationData":[OSD([sQuery(id+"F4.wireOp",EDGE,"E13.0.2")])]})]});
            var Q58;
            Q58=makeQuery(id+"F10.opBoolean","INTERSECT",EDGE,{"derivedFrom":[makeQuery(id+"F1.opExtrude","CAP_FACE",FACE,{"disambiguationData":[OSD([sQuery(id+"F0.wireOp",EDGE,"E3.sketch_text.stroke-156"),sQuery(id+"F0.wireOp",EDGE,"E3.sketch_text.stroke-157"),sQuery(id+"F0.wireOp",EDGE,"E3.sketch_text.stroke-158"),sQuery(id+"F0.wireOp",EDGE,"E3.sketch_text.stroke-159"),sQuery(id+"F0.wireOp",EDGE,"E3.sketch_text.stroke-160"),sQuery(id+"F0.wireOp",EDGE,"E3.sketch_text.stroke-161"),sQuery(id+"F0.wireOp",EDGE,"E3.sketch_text.stroke-162"),sQuery(id+"F0.wireOp",EDGE,"E3.sketch_text.stroke-163"),sQuery(id+"F0.wireOp",EDGE,"E3.sketch_text.stroke-164"),sQuery(id+"F0.wireOp",EDGE,"E3.sketch_text.stroke-165"),sQuery(id+"F0.wireOp",EDGE,"E3.sketch_text.stroke-166"),sQuery(id+"F0.wireOp",EDGE,"E3.sketch_text.stroke-167"),sQuery(id+"F0.wireOp",EDGE,"E3.sketch_text.stroke-168"),sQuery(id+"F0.wireOp",EDGE,"E3.sketch_text.stroke-169"),sQuery(id+"F0.wireOp",EDGE,"E3.sketch_text.stroke-170"),sQuery(id+"F0.wireOp",EDGE,"E3.sketch_text.stroke-171"),sQuery(id+"F0.wireOp",EDGE,"E3.sketch_text.stroke-172"),sQuery(id+"F0.wireOp",EDGE,"E3.sketch_text.stroke-173"),sQuery(id+"F0.wireOp",EDGE,"E3.sketch_text.stroke-174")])],"isStart":true}),makeQuery(id+"F5.opExtrude","SWEPT_FACE",FACE,{"disambiguationData":[OSD([sQuery(id+"F4.wireOp",EDGE,"E13.0.2")])]})]});
            var Q59;
            Q59=makeQuery(id+"F10.opBoolean","INTERSECT",EDGE,{"derivedFrom":[makeQuery(id+"F1.opExtrude","CAP_FACE",FACE,{"disambiguationData":[OSD([sQuery(id+"F0.wireOp",EDGE,"E3.sketch_text.stroke-194"),sQuery(id+"F0.wireOp",EDGE,"E3.sketch_text.stroke-195"),sQuery(id+"F0.wireOp",EDGE,"E3.sketch_text.stroke-196"),sQuery(id+"F0.wireOp",EDGE,"E3.sketch_text.stroke-197"),sQuery(id+"F0.wireOp",EDGE,"E3.sketch_text.stroke-198"),sQuery(id+"F0.wireOp",EDGE,"E3.sketch_text.stroke-199"),sQuery(id+"F0.wireOp",EDGE,"E3.sketch_text.stroke-200"),sQuery(id+"F0.wireOp",EDGE,"E3.sketch_text.stroke-201"),sQuery(id+"F0.wireOp",EDGE,"E3.sketch_text.stroke-202"),sQuery(id+"F0.wireOp",EDGE,"E3.sketch_text.stroke-203"),sQuery(id+"F0.wireOp",EDGE,"E3.sketch_text.stroke-204"),sQuery(id+"F0.wireOp",EDGE,"E3.sketch_text.stroke-205"),sQuery(id+"F0.wireOp",EDGE,"E3.sketch_text.stroke-206"),sQuery(id+"F0.wireOp",EDGE,"E3.sketch_text.stroke-207"),sQuery(id+"F0.wireOp",EDGE,"E3.sketch_text.stroke-208"),sQuery(id+"F0.wireOp",EDGE,"E3.sketch_text.stroke-209"),sQuery(id+"F0.wireOp",EDGE,"E3.sketch_text.stroke-210"),sQuery(id+"F0.wireOp",EDGE,"E3.sketch_text.stroke-211"),sQuery(id+"F0.wireOp",EDGE,"E3.sketch_text.stroke-212"),sQuery(id+"F0.wireOp",EDGE,"E3.sketch_text.stroke-213"),sQuery(id+"F0.wireOp",EDGE,"E3.sketch_text.stroke-214"),sQuery(id+"F0.wireOp",EDGE,"E3.sketch_text.stroke-215"),sQuery(id+"F0.wireOp",EDGE,"E3.sketch_text.stroke-216"),sQuery(id+"F0.wireOp",EDGE,"E3.sketch_text.stroke-217"),sQuery(id+"F0.wireOp",EDGE,"E3.sketch_text.stroke-218"),sQuery(id+"F0.wireOp",EDGE,"E3.sketch_text.stroke-219"),sQuery(id+"F0.wireOp",EDGE,"E3.sketch_text.stroke-220"),sQuery(id+"F0.wireOp",EDGE,"E3.sketch_text.stroke-221"),sQuery(id+"F0.wireOp",EDGE,"E3.sketch_text.stroke-222"),sQuery(id+"F0.wireOp",EDGE,"E3.sketch_text.stroke-223"),sQuery(id+"F0.wireOp",EDGE,"E3.sketch_text.stroke-224"),sQuery(id+"F0.wireOp",EDGE,"E3.sketch_text.stroke-225"),sQuery(id+"F0.wireOp",EDGE,"E3.sketch_text.stroke-226"),sQuery(id+"F0.wireOp",EDGE,"E3.sketch_text.stroke-227"),sQuery(id+"F0.wireOp",EDGE,"E3.sketch_text.stroke-228"),sQuery(id+"F0.wireOp",EDGE,"E3.sketch_text.stroke-229")])],"isStart":true}),makeQuery(id+"F6.opFillet","BLEND_FACE",FACE,{"disambiguationData":[OSD([sQuery(id+"F4.wireOp",EDGE,"E13.0.2"),sQuery(id+"F4.wireOp",EDGE,"E13.0.3")])]})]});
            var Q60;
            Q60=makeQuery(id+"F10.opBoolean","INTERSECT",EDGE,{"disambiguationData":[OD(1.0)],"derivedFrom":[makeQuery(id+"F1.opExtrude","CAP_FACE",FACE,{"disambiguationData":[OSD([sQuery(id+"F0.wireOp",EDGE,"E3.sketch_text.stroke-194"),sQuery(id+"F0.wireOp",EDGE,"E3.sketch_text.stroke-195"),sQuery(id+"F0.wireOp",EDGE,"E3.sketch_text.stroke-196"),sQuery(id+"F0.wireOp",EDGE,"E3.sketch_text.stroke-197"),sQuery(id+"F0.wireOp",EDGE,"E3.sketch_text.stroke-198"),sQuery(id+"F0.wireOp",EDGE,"E3.sketch_text.stroke-199"),sQuery(id+"F0.wireOp",EDGE,"E3.sketch_text.stroke-200"),sQuery(id+"F0.wireOp",EDGE,"E3.sketch_text.stroke-201"),sQuery(id+"F0.wireOp",EDGE,"E3.sketch_text.stroke-202"),sQuery(id+"F0.wireOp",EDGE,"E3.sketch_text.stroke-203"),sQuery(id+"F0.wireOp",EDGE,"E3.sketch_text.stroke-204"),sQuery(id+"F0.wireOp",EDGE,"E3.sketch_text.stroke-205"),sQuery(id+"F0.wireOp",EDGE,"E3.sketch_text.stroke-206"),sQuery(id+"F0.wireOp",EDGE,"E3.sketch_text.stroke-207"),sQuery(id+"F0.wireOp",EDGE,"E3.sketch_text.stroke-208"),sQuery(id+"F0.wireOp",EDGE,"E3.sketch_text.stroke-209"),sQuery(id+"F0.wireOp",EDGE,"E3.sketch_text.stroke-210"),sQuery(id+"F0.wireOp",EDGE,"E3.sketch_text.stroke-211"),sQuery(id+"F0.wireOp",EDGE,"E3.sketch_text.stroke-212"),sQuery(id+"F0.wireOp",EDGE,"E3.sketch_text.stroke-213"),sQuery(id+"F0.wireOp",EDGE,"E3.sketch_text.stroke-214"),sQuery(id+"F0.wireOp",EDGE,"E3.sketch_text.stroke-215"),sQuery(id+"F0.wireOp",EDGE,"E3.sketch_text.stroke-216"),sQuery(id+"F0.wireOp",EDGE,"E3.sketch_text.stroke-217"),sQuery(id+"F0.wireOp",EDGE,"E3.sketch_text.stroke-218"),sQuery(id+"F0.wireOp",EDGE,"E3.sketch_text.stroke-219"),sQuery(id+"F0.wireOp",EDGE,"E3.sketch_text.stroke-220"),sQuery(id+"F0.wireOp",EDGE,"E3.sketch_text.stroke-221"),sQuery(id+"F0.wireOp",EDGE,"E3.sketch_text.stroke-222"),sQuery(id+"F0.wireOp",EDGE,"E3.sketch_text.stroke-223"),sQuery(id+"F0.wireOp",EDGE,"E3.sketch_text.stroke-224"),sQuery(id+"F0.wireOp",EDGE,"E3.sketch_text.stroke-225"),sQuery(id+"F0.wireOp",EDGE,"E3.sketch_text.stroke-226"),sQuery(id+"F0.wireOp",EDGE,"E3.sketch_text.stroke-227"),sQuery(id+"F0.wireOp",EDGE,"E3.sketch_text.stroke-228"),sQuery(id+"F0.wireOp",EDGE,"E3.sketch_text.stroke-229")])],"isStart":true}),makeQuery(id+"F5.opExtrude","SWEPT_FACE",FACE,{"disambiguationData":[OSD([sQuery(id+"F4.wireOp",EDGE,"E13.0.2")])]})]});
            var Q61;
            Q61=makeQuery(id+"F10.opBoolean","INTERSECT",EDGE,{"derivedFrom":[makeQuery(id+"F1.opExtrude","CAP_FACE",FACE,{"disambiguationData":[OSD([sQuery(id+"F0.wireOp",EDGE,"E3.sketch_text.stroke-175"),sQuery(id+"F0.wireOp",EDGE,"E3.sketch_text.stroke-176"),sQuery(id+"F0.wireOp",EDGE,"E3.sketch_text.stroke-177"),sQuery(id+"F0.wireOp",EDGE,"E3.sketch_text.stroke-178"),sQuery(id+"F0.wireOp",EDGE,"E3.sketch_text.stroke-179"),sQuery(id+"F0.wireOp",EDGE,"E3.sketch_text.stroke-180"),sQuery(id+"F0.wireOp",EDGE,"E3.sketch_text.stroke-181"),sQuery(id+"F0.wireOp",EDGE,"E3.sketch_text.stroke-182"),sQuery(id+"F0.wireOp",EDGE,"E3.sketch_text.stroke-183"),sQuery(id+"F0.wireOp",EDGE,"E3.sketch_text.stroke-184"),sQuery(id+"F0.wireOp",EDGE,"E3.sketch_text.stroke-185"),sQuery(id+"F0.wireOp",EDGE,"E3.sketch_text.stroke-186"),sQuery(id+"F0.wireOp",EDGE,"E3.sketch_text.stroke-187"),sQuery(id+"F0.wireOp",EDGE,"E3.sketch_text.stroke-188"),sQuery(id+"F0.wireOp",EDGE,"E3.sketch_text.stroke-189"),sQuery(id+"F0.wireOp",EDGE,"E3.sketch_text.stroke-190"),sQuery(id+"F0.wireOp",EDGE,"E3.sketch_text.stroke-191"),sQuery(id+"F0.wireOp",EDGE,"E3.sketch_text.stroke-192"),sQuery(id+"F0.wireOp",EDGE,"E3.sketch_text.stroke-193")])],"isStart":true}),makeQuery(id+"F5.opExtrude","SWEPT_FACE",FACE,{"disambiguationData":[OSD([sQuery(id+"F4.wireOp",EDGE,"E13.0.2")])]})]});
            var Q62;
            Q62=makeQuery(id+"F11.opBoolean","INTERSECT",EDGE,{"derivedFrom":[makeQuery(id+"F1.opExtrude","CAP_FACE",FACE,{"disambiguationData":[OSD([sQuery(id+"F0.wireOp",EDGE,"E4.sketch_text.stroke-177"),sQuery(id+"F0.wireOp",EDGE,"E4.sketch_text.stroke-178"),sQuery(id+"F0.wireOp",EDGE,"E4.sketch_text.stroke-179"),sQuery(id+"F0.wireOp",EDGE,"E4.sketch_text.stroke-180"),sQuery(id+"F0.wireOp",EDGE,"E4.sketch_text.stroke-181"),sQuery(id+"F0.wireOp",EDGE,"E4.sketch_text.stroke-182"),sQuery(id+"F0.wireOp",EDGE,"E4.sketch_text.stroke-183"),sQuery(id+"F0.wireOp",EDGE,"E4.sketch_text.stroke-184"),sQuery(id+"F0.wireOp",EDGE,"E4.sketch_text.stroke-185"),sQuery(id+"F0.wireOp",EDGE,"E4.sketch_text.stroke-186"),sQuery(id+"F0.wireOp",EDGE,"E4.sketch_text.stroke-187"),sQuery(id+"F0.wireOp",EDGE,"E4.sketch_text.stroke-188"),sQuery(id+"F0.wireOp",EDGE,"E4.sketch_text.stroke-189"),sQuery(id+"F0.wireOp",EDGE,"E4.sketch_text.stroke-190"),sQuery(id+"F0.wireOp",EDGE,"E4.sketch_text.stroke-191"),sQuery(id+"F0.wireOp",EDGE,"E4.sketch_text.stroke-192"),sQuery(id+"F0.wireOp",EDGE,"E4.sketch_text.stroke-193"),sQuery(id+"F0.wireOp",EDGE,"E4.sketch_text.stroke-194"),sQuery(id+"F0.wireOp",EDGE,"E4.sketch_text.stroke-195"),sQuery(id+"F0.wireOp",EDGE,"E4.sketch_text.stroke-196"),sQuery(id+"F0.wireOp",EDGE,"E4.sketch_text.stroke-197"),sQuery(id+"F0.wireOp",EDGE,"E4.sketch_text.stroke-198"),sQuery(id+"F0.wireOp",EDGE,"E4.sketch_text.stroke-199"),sQuery(id+"F0.wireOp",EDGE,"E4.sketch_text.stroke-200"),sQuery(id+"F0.wireOp",EDGE,"E4.sketch_text.stroke-201"),sQuery(id+"F0.wireOp",EDGE,"E4.sketch_text.stroke-202"),sQuery(id+"F0.wireOp",EDGE,"E4.sketch_text.stroke-203"),sQuery(id+"F0.wireOp",EDGE,"E4.sketch_text.stroke-204"),sQuery(id+"F0.wireOp",EDGE,"E4.sketch_text.stroke-205"),sQuery(id+"F0.wireOp",EDGE,"E4.sketch_text.stroke-206"),sQuery(id+"F0.wireOp",EDGE,"E4.sketch_text.stroke-207"),sQuery(id+"F0.wireOp",EDGE,"E4.sketch_text.stroke-208"),sQuery(id+"F0.wireOp",EDGE,"E4.sketch_text.stroke-209"),sQuery(id+"F0.wireOp",EDGE,"E4.sketch_text.stroke-210"),sQuery(id+"F0.wireOp",EDGE,"E4.sketch_text.stroke-211"),sQuery(id+"F0.wireOp",EDGE,"E4.sketch_text.stroke-212")])],"isStart":true}),makeQuery(id+"F6.opFillet","BLEND_FACE",FACE,{"disambiguationData":[OSD([sQuery(id+"F4.wireOp",EDGE,"E14.0.2"),sQuery(id+"F4.wireOp",EDGE,"E14.0.3")])]})]});
            var Q63;
            Q63=makeQuery(id+"F11.opBoolean","INTERSECT",EDGE,{"disambiguationData":[OD(1.0)],"derivedFrom":[makeQuery(id+"F1.opExtrude","CAP_FACE",FACE,{"disambiguationData":[OSD([sQuery(id+"F0.wireOp",EDGE,"E4.sketch_text.stroke-177"),sQuery(id+"F0.wireOp",EDGE,"E4.sketch_text.stroke-178"),sQuery(id+"F0.wireOp",EDGE,"E4.sketch_text.stroke-179"),sQuery(id+"F0.wireOp",EDGE,"E4.sketch_text.stroke-180"),sQuery(id+"F0.wireOp",EDGE,"E4.sketch_text.stroke-181"),sQuery(id+"F0.wireOp",EDGE,"E4.sketch_text.stroke-182"),sQuery(id+"F0.wireOp",EDGE,"E4.sketch_text.stroke-183"),sQuery(id+"F0.wireOp",EDGE,"E4.sketch_text.stroke-184"),sQuery(id+"F0.wireOp",EDGE,"E4.sketch_text.stroke-185"),sQuery(id+"F0.wireOp",EDGE,"E4.sketch_text.stroke-186"),sQuery(id+"F0.wireOp",EDGE,"E4.sketch_text.stroke-187"),sQuery(id+"F0.wireOp",EDGE,"E4.sketch_text.stroke-188"),sQuery(id+"F0.wireOp",EDGE,"E4.sketch_text.stroke-189"),sQuery(id+"F0.wireOp",EDGE,"E4.sketch_text.stroke-190"),sQuery(id+"F0.wireOp",EDGE,"E4.sketch_text.stroke-191"),sQuery(id+"F0.wireOp",EDGE,"E4.sketch_text.stroke-192"),sQuery(id+"F0.wireOp",EDGE,"E4.sketch_text.stroke-193"),sQuery(id+"F0.wireOp",EDGE,"E4.sketch_text.stroke-194"),sQuery(id+"F0.wireOp",EDGE,"E4.sketch_text.stroke-195"),sQuery(id+"F0.wireOp",EDGE,"E4.sketch_text.stroke-196"),sQuery(id+"F0.wireOp",EDGE,"E4.sketch_text.stroke-197"),sQuery(id+"F0.wireOp",EDGE,"E4.sketch_text.stroke-198"),sQuery(id+"F0.wireOp",EDGE,"E4.sketch_text.stroke-199"),sQuery(id+"F0.wireOp",EDGE,"E4.sketch_text.stroke-200"),sQuery(id+"F0.wireOp",EDGE,"E4.sketch_text.stroke-201"),sQuery(id+"F0.wireOp",EDGE,"E4.sketch_text.stroke-202"),sQuery(id+"F0.wireOp",EDGE,"E4.sketch_text.stroke-203"),sQuery(id+"F0.wireOp",EDGE,"E4.sketch_text.stroke-204"),sQuery(id+"F0.wireOp",EDGE,"E4.sketch_text.stroke-205"),sQuery(id+"F0.wireOp",EDGE,"E4.sketch_text.stroke-206"),sQuery(id+"F0.wireOp",EDGE,"E4.sketch_text.stroke-207"),sQuery(id+"F0.wireOp",EDGE,"E4.sketch_text.stroke-208"),sQuery(id+"F0.wireOp",EDGE,"E4.sketch_text.stroke-209"),sQuery(id+"F0.wireOp",EDGE,"E4.sketch_text.stroke-210"),sQuery(id+"F0.wireOp",EDGE,"E4.sketch_text.stroke-211"),sQuery(id+"F0.wireOp",EDGE,"E4.sketch_text.stroke-212")])],"isStart":true}),makeQuery(id+"F5.opExtrude","SWEPT_FACE",FACE,{"disambiguationData":[OSD([sQuery(id+"F4.wireOp",EDGE,"E14.0.2")])]})]});
            var Q64;
            Q64=makeQuery(id+"F11.opBoolean","INTERSECT",EDGE,{"derivedFrom":[makeQuery(id+"F1.opExtrude","CAP_FACE",FACE,{"disambiguationData":[OSD([sQuery(id+"F0.wireOp",EDGE,"E4.sketch_text.stroke-158"),sQuery(id+"F0.wireOp",EDGE,"E4.sketch_text.stroke-159"),sQuery(id+"F0.wireOp",EDGE,"E4.sketch_text.stroke-160"),sQuery(id+"F0.wireOp",EDGE,"E4.sketch_text.stroke-161"),sQuery(id+"F0.wireOp",EDGE,"E4.sketch_text.stroke-162"),sQuery(id+"F0.wireOp",EDGE,"E4.sketch_text.stroke-163"),sQuery(id+"F0.wireOp",EDGE,"E4.sketch_text.stroke-164"),sQuery(id+"F0.wireOp",EDGE,"E4.sketch_text.stroke-165"),sQuery(id+"F0.wireOp",EDGE,"E4.sketch_text.stroke-166"),sQuery(id+"F0.wireOp",EDGE,"E4.sketch_text.stroke-167"),sQuery(id+"F0.wireOp",EDGE,"E4.sketch_text.stroke-168"),sQuery(id+"F0.wireOp",EDGE,"E4.sketch_text.stroke-169"),sQuery(id+"F0.wireOp",EDGE,"E4.sketch_text.stroke-170"),sQuery(id+"F0.wireOp",EDGE,"E4.sketch_text.stroke-171"),sQuery(id+"F0.wireOp",EDGE,"E4.sketch_text.stroke-172"),sQuery(id+"F0.wireOp",EDGE,"E4.sketch_text.stroke-173"),sQuery(id+"F0.wireOp",EDGE,"E4.sketch_text.stroke-174"),sQuery(id+"F0.wireOp",EDGE,"E4.sketch_text.stroke-175"),sQuery(id+"F0.wireOp",EDGE,"E4.sketch_text.stroke-176")])],"isStart":true}),makeQuery(id+"F5.opExtrude","SWEPT_FACE",FACE,{"disambiguationData":[OSD([sQuery(id+"F4.wireOp",EDGE,"E14.0.2")])]})]});
            var Q65;
            Q65=makeQuery(id+"F11.opBoolean","INTERSECT",EDGE,{"derivedFrom":[makeQuery(id+"F1.opExtrude","CAP_FACE",FACE,{"disambiguationData":[OSD([sQuery(id+"F0.wireOp",EDGE,"E4.sketch_text.stroke-144"),sQuery(id+"F0.wireOp",EDGE,"E4.sketch_text.stroke-145"),sQuery(id+"F0.wireOp",EDGE,"E4.sketch_text.stroke-146"),sQuery(id+"F0.wireOp",EDGE,"E4.sketch_text.stroke-147"),sQuery(id+"F0.wireOp",EDGE,"E4.sketch_text.stroke-148"),sQuery(id+"F0.wireOp",EDGE,"E4.sketch_text.stroke-149"),sQuery(id+"F0.wireOp",EDGE,"E4.sketch_text.stroke-150")])],"isStart":true}),makeQuery(id+"F5.opExtrude","SWEPT_FACE",FACE,{"disambiguationData":[OSD([sQuery(id+"F4.wireOp",EDGE,"E14.0.2")])]})]});
            var Q66;
            Q66=makeQuery(id+"F11.opBoolean","INTERSECT",EDGE,{"derivedFrom":[makeQuery(id+"F1.opExtrude","CAP_FACE",FACE,{"disambiguationData":[OSD([sQuery(id+"F0.wireOp",EDGE,"E4.sketch_text.stroke-119"),sQuery(id+"F0.wireOp",EDGE,"E4.sketch_text.stroke-120"),sQuery(id+"F0.wireOp",EDGE,"E4.sketch_text.stroke-121"),sQuery(id+"F0.wireOp",EDGE,"E4.sketch_text.stroke-122"),sQuery(id+"F0.wireOp",EDGE,"E4.sketch_text.stroke-123"),sQuery(id+"F0.wireOp",EDGE,"E4.sketch_text.stroke-124"),sQuery(id+"F0.wireOp",EDGE,"E4.sketch_text.stroke-125"),sQuery(id+"F0.wireOp",EDGE,"E4.sketch_text.stroke-126"),sQuery(id+"F0.wireOp",EDGE,"E4.sketch_text.stroke-127"),sQuery(id+"F0.wireOp",EDGE,"E4.sketch_text.stroke-128"),sQuery(id+"F0.wireOp",EDGE,"E4.sketch_text.stroke-129"),sQuery(id+"F0.wireOp",EDGE,"E4.sketch_text.stroke-130"),sQuery(id+"F0.wireOp",EDGE,"E4.sketch_text.stroke-131"),sQuery(id+"F0.wireOp",EDGE,"E4.sketch_text.stroke-132"),sQuery(id+"F0.wireOp",EDGE,"E4.sketch_text.stroke-133"),sQuery(id+"F0.wireOp",EDGE,"E4.sketch_text.stroke-134"),sQuery(id+"F0.wireOp",EDGE,"E4.sketch_text.stroke-135"),sQuery(id+"F0.wireOp",EDGE,"E4.sketch_text.stroke-136"),sQuery(id+"F0.wireOp",EDGE,"E4.sketch_text.stroke-137"),sQuery(id+"F0.wireOp",EDGE,"E4.sketch_text.stroke-138"),sQuery(id+"F0.wireOp",EDGE,"E4.sketch_text.stroke-139"),sQuery(id+"F0.wireOp",EDGE,"E4.sketch_text.stroke-140"),sQuery(id+"F0.wireOp",EDGE,"E4.sketch_text.stroke-141"),sQuery(id+"F0.wireOp",EDGE,"E4.sketch_text.stroke-142"),sQuery(id+"F0.wireOp",EDGE,"E4.sketch_text.stroke-143")])],"isStart":true}),makeQuery(id+"F5.opExtrude","SWEPT_FACE",FACE,{"disambiguationData":[OSD([sQuery(id+"F4.wireOp",EDGE,"E14.0.2")])]})]});
            var Q67;
            Q67=makeQuery(id+"F11.opBoolean","INTERSECT",EDGE,{"derivedFrom":[makeQuery(id+"F1.opExtrude","CAP_FACE",FACE,{"disambiguationData":[OSD([sQuery(id+"F0.wireOp",EDGE,"E4.sketch_text.stroke-107"),sQuery(id+"F0.wireOp",EDGE,"E4.sketch_text.stroke-108"),sQuery(id+"F0.wireOp",EDGE,"E4.sketch_text.stroke-109"),sQuery(id+"F0.wireOp",EDGE,"E4.sketch_text.stroke-110")])],"isStart":true}),makeQuery(id+"F5.opExtrude","SWEPT_FACE",FACE,{"disambiguationData":[OSD([sQuery(id+"F4.wireOp",EDGE,"E14.0.2")])]})]});
            var Q68;
            Q68=makeQuery(id+"F11.opBoolean","INTERSECT",EDGE,{"disambiguationData":[OD(0.0)],"derivedFrom":[makeQuery(id+"F1.opExtrude","CAP_FACE",FACE,{"disambiguationData":[OSD([sQuery(id+"F0.wireOp",EDGE,"E4.sketch_text.stroke-71"),sQuery(id+"F0.wireOp",EDGE,"E4.sketch_text.stroke-72"),sQuery(id+"F0.wireOp",EDGE,"E4.sketch_text.stroke-73"),sQuery(id+"F0.wireOp",EDGE,"E4.sketch_text.stroke-74"),sQuery(id+"F0.wireOp",EDGE,"E4.sketch_text.stroke-75"),sQuery(id+"F0.wireOp",EDGE,"E4.sketch_text.stroke-76"),sQuery(id+"F0.wireOp",EDGE,"E4.sketch_text.stroke-77"),sQuery(id+"F0.wireOp",EDGE,"E4.sketch_text.stroke-78"),sQuery(id+"F0.wireOp",EDGE,"E4.sketch_text.stroke-79"),sQuery(id+"F0.wireOp",EDGE,"E4.sketch_text.stroke-80"),sQuery(id+"F0.wireOp",EDGE,"E4.sketch_text.stroke-81"),sQuery(id+"F0.wireOp",EDGE,"E4.sketch_text.stroke-82"),sQuery(id+"F0.wireOp",EDGE,"E4.sketch_text.stroke-83"),sQuery(id+"F0.wireOp",EDGE,"E4.sketch_text.stroke-84"),sQuery(id+"F0.wireOp",EDGE,"E4.sketch_text.stroke-85"),sQuery(id+"F0.wireOp",EDGE,"E4.sketch_text.stroke-86"),sQuery(id+"F0.wireOp",EDGE,"E4.sketch_text.stroke-87"),sQuery(id+"F0.wireOp",EDGE,"E4.sketch_text.stroke-88"),sQuery(id+"F0.wireOp",EDGE,"E4.sketch_text.stroke-89"),sQuery(id+"F0.wireOp",EDGE,"E4.sketch_text.stroke-90"),sQuery(id+"F0.wireOp",EDGE,"E4.sketch_text.stroke-91"),sQuery(id+"F0.wireOp",EDGE,"E4.sketch_text.stroke-92"),sQuery(id+"F0.wireOp",EDGE,"E4.sketch_text.stroke-93"),sQuery(id+"F0.wireOp",EDGE,"E4.sketch_text.stroke-94"),sQuery(id+"F0.wireOp",EDGE,"E4.sketch_text.stroke-95"),sQuery(id+"F0.wireOp",EDGE,"E4.sketch_text.stroke-96"),sQuery(id+"F0.wireOp",EDGE,"E4.sketch_text.stroke-97"),sQuery(id+"F0.wireOp",EDGE,"E4.sketch_text.stroke-98"),sQuery(id+"F0.wireOp",EDGE,"E4.sketch_text.stroke-99"),sQuery(id+"F0.wireOp",EDGE,"E4.sketch_text.stroke-100"),sQuery(id+"F0.wireOp",EDGE,"E4.sketch_text.stroke-101"),sQuery(id+"F0.wireOp",EDGE,"E4.sketch_text.stroke-102"),sQuery(id+"F0.wireOp",EDGE,"E4.sketch_text.stroke-103"),sQuery(id+"F0.wireOp",EDGE,"E4.sketch_text.stroke-104"),sQuery(id+"F0.wireOp",EDGE,"E4.sketch_text.stroke-105"),sQuery(id+"F0.wireOp",EDGE,"E4.sketch_text.stroke-106")])],"isStart":true}),makeQuery(id+"F5.opExtrude","SWEPT_FACE",FACE,{"disambiguationData":[OSD([sQuery(id+"F4.wireOp",EDGE,"E14.0.2")])]})]});
            var Q69;
            Q69=makeQuery(id+"F11.opBoolean","INTERSECT",EDGE,{"disambiguationData":[OD(1.0)],"derivedFrom":[makeQuery(id+"F1.opExtrude","CAP_FACE",FACE,{"disambiguationData":[OSD([sQuery(id+"F0.wireOp",EDGE,"E4.sketch_text.stroke-71"),sQuery(id+"F0.wireOp",EDGE,"E4.sketch_text.stroke-72"),sQuery(id+"F0.wireOp",EDGE,"E4.sketch_text.stroke-73"),sQuery(id+"F0.wireOp",EDGE,"E4.sketch_text.stroke-74"),sQuery(id+"F0.wireOp",EDGE,"E4.sketch_text.stroke-75"),sQuery(id+"F0.wireOp",EDGE,"E4.sketch_text.stroke-76"),sQuery(id+"F0.wireOp",EDGE,"E4.sketch_text.stroke-77"),sQuery(id+"F0.wireOp",EDGE,"E4.sketch_text.stroke-78"),sQuery(id+"F0.wireOp",EDGE,"E4.sketch_text.stroke-79"),sQuery(id+"F0.wireOp",EDGE,"E4.sketch_text.stroke-80"),sQuery(id+"F0.wireOp",EDGE,"E4.sketch_text.stroke-81"),sQuery(id+"F0.wireOp",EDGE,"E4.sketch_text.stroke-82"),sQuery(id+"F0.wireOp",EDGE,"E4.sketch_text.stroke-83"),sQuery(id+"F0.wireOp",EDGE,"E4.sketch_text.stroke-84"),sQuery(id+"F0.wireOp",EDGE,"E4.sketch_text.stroke-85"),sQuery(id+"F0.wireOp",EDGE,"E4.sketch_text.stroke-86"),sQuery(id+"F0.wireOp",EDGE,"E4.sketch_text.stroke-87"),sQuery(id+"F0.wireOp",EDGE,"E4.sketch_text.stroke-88"),sQuery(id+"F0.wireOp",EDGE,"E4.sketch_text.stroke-89"),sQuery(id+"F0.wireOp",EDGE,"E4.sketch_text.stroke-90"),sQuery(id+"F0.wireOp",EDGE,"E4.sketch_text.stroke-91"),sQuery(id+"F0.wireOp",EDGE,"E4.sketch_text.stroke-92"),sQuery(id+"F0.wireOp",EDGE,"E4.sketch_text.stroke-93"),sQuery(id+"F0.wireOp",EDGE,"E4.sketch_text.stroke-94"),sQuery(id+"F0.wireOp",EDGE,"E4.sketch_text.stroke-95"),sQuery(id+"F0.wireOp",EDGE,"E4.sketch_text.stroke-96"),sQuery(id+"F0.wireOp",EDGE,"E4.sketch_text.stroke-97"),sQuery(id+"F0.wireOp",EDGE,"E4.sketch_text.stroke-98"),sQuery(id+"F0.wireOp",EDGE,"E4.sketch_text.stroke-99"),sQuery(id+"F0.wireOp",EDGE,"E4.sketch_text.stroke-100"),sQuery(id+"F0.wireOp",EDGE,"E4.sketch_text.stroke-101"),sQuery(id+"F0.wireOp",EDGE,"E4.sketch_text.stroke-102"),sQuery(id+"F0.wireOp",EDGE,"E4.sketch_text.stroke-103"),sQuery(id+"F0.wireOp",EDGE,"E4.sketch_text.stroke-104"),sQuery(id+"F0.wireOp",EDGE,"E4.sketch_text.stroke-105"),sQuery(id+"F0.wireOp",EDGE,"E4.sketch_text.stroke-106")])],"isStart":true}),makeQuery(id+"F5.opExtrude","SWEPT_FACE",FACE,{"disambiguationData":[OSD([sQuery(id+"F4.wireOp",EDGE,"E14.0.2")])]})]});
            var Q70;
            Q70=makeQuery(id+"F11.opBoolean","INTERSECT",EDGE,{"derivedFrom":[makeQuery(id+"F1.opExtrude","CAP_FACE",FACE,{"disambiguationData":[OSD([sQuery(id+"F0.wireOp",EDGE,"E4.sketch_text.stroke-52"),sQuery(id+"F0.wireOp",EDGE,"E4.sketch_text.stroke-53"),sQuery(id+"F0.wireOp",EDGE,"E4.sketch_text.stroke-54"),sQuery(id+"F0.wireOp",EDGE,"E4.sketch_text.stroke-55"),sQuery(id+"F0.wireOp",EDGE,"E4.sketch_text.stroke-56"),sQuery(id+"F0.wireOp",EDGE,"E4.sketch_text.stroke-57"),sQuery(id+"F0.wireOp",EDGE,"E4.sketch_text.stroke-58"),sQuery(id+"F0.wireOp",EDGE,"E4.sketch_text.stroke-59"),sQuery(id+"F0.wireOp",EDGE,"E4.sketch_text.stroke-60"),sQuery(id+"F0.wireOp",EDGE,"E4.sketch_text.stroke-61"),sQuery(id+"F0.wireOp",EDGE,"E4.sketch_text.stroke-62"),sQuery(id+"F0.wireOp",EDGE,"E4.sketch_text.stroke-63"),sQuery(id+"F0.wireOp",EDGE,"E4.sketch_text.stroke-64"),sQuery(id+"F0.wireOp",EDGE,"E4.sketch_text.stroke-65"),sQuery(id+"F0.wireOp",EDGE,"E4.sketch_text.stroke-66"),sQuery(id+"F0.wireOp",EDGE,"E4.sketch_text.stroke-67"),sQuery(id+"F0.wireOp",EDGE,"E4.sketch_text.stroke-68"),sQuery(id+"F0.wireOp",EDGE,"E4.sketch_text.stroke-69"),sQuery(id+"F0.wireOp",EDGE,"E4.sketch_text.stroke-70")])],"isStart":true}),makeQuery(id+"F5.opExtrude","SWEPT_FACE",FACE,{"disambiguationData":[OSD([sQuery(id+"F4.wireOp",EDGE,"E14.0.2")])]})]});
            var Q71;
            Q71=makeQuery(id+"F11.opBoolean","INTERSECT",EDGE,{"derivedFrom":[makeQuery(id+"F1.opExtrude","CAP_FACE",FACE,{"disambiguationData":[OSD([sQuery(id+"F0.wireOp",EDGE,"E4.sketch_text.stroke-33"),sQuery(id+"F0.wireOp",EDGE,"E4.sketch_text.stroke-34"),sQuery(id+"F0.wireOp",EDGE,"E4.sketch_text.stroke-35"),sQuery(id+"F0.wireOp",EDGE,"E4.sketch_text.stroke-36"),sQuery(id+"F0.wireOp",EDGE,"E4.sketch_text.stroke-37"),sQuery(id+"F0.wireOp",EDGE,"E4.sketch_text.stroke-38"),sQuery(id+"F0.wireOp",EDGE,"E4.sketch_text.stroke-39"),sQuery(id+"F0.wireOp",EDGE,"E4.sketch_text.stroke-40"),sQuery(id+"F0.wireOp",EDGE,"E4.sketch_text.stroke-41"),sQuery(id+"F0.wireOp",EDGE,"E4.sketch_text.stroke-42"),sQuery(id+"F0.wireOp",EDGE,"E4.sketch_text.stroke-43"),sQuery(id+"F0.wireOp",EDGE,"E4.sketch_text.stroke-44"),sQuery(id+"F0.wireOp",EDGE,"E4.sketch_text.stroke-45"),sQuery(id+"F0.wireOp",EDGE,"E4.sketch_text.stroke-46"),sQuery(id+"F0.wireOp",EDGE,"E4.sketch_text.stroke-47"),sQuery(id+"F0.wireOp",EDGE,"E4.sketch_text.stroke-48"),sQuery(id+"F0.wireOp",EDGE,"E4.sketch_text.stroke-49"),sQuery(id+"F0.wireOp",EDGE,"E4.sketch_text.stroke-50"),sQuery(id+"F0.wireOp",EDGE,"E4.sketch_text.stroke-51")])],"isStart":true}),makeQuery(id+"F5.opExtrude","SWEPT_FACE",FACE,{"disambiguationData":[OSD([sQuery(id+"F4.wireOp",EDGE,"E14.0.2")])]})]});
            var Q72;
            Q72=makeQuery(id+"F11.opBoolean","INTERSECT",EDGE,{"derivedFrom":[makeQuery(id+"F1.opExtrude","CAP_FACE",FACE,{"disambiguationData":[OSD([sQuery(id+"F0.wireOp",EDGE,"E4.sketch_text.stroke-29"),sQuery(id+"F0.wireOp",EDGE,"E4.sketch_text.stroke-30"),sQuery(id+"F0.wireOp",EDGE,"E4.sketch_text.stroke-31"),sQuery(id+"F0.wireOp",EDGE,"E4.sketch_text.stroke-32")])],"isStart":true}),makeQuery(id+"F5.opExtrude","SWEPT_FACE",FACE,{"disambiguationData":[OSD([sQuery(id+"F4.wireOp",EDGE,"E14.0.2")])]})]});
            var Q73;
            Q73=makeQuery(id+"F11.opBoolean","INTERSECT",EDGE,{"derivedFrom":[makeQuery(id+"F1.opExtrude","CAP_FACE",FACE,{"disambiguationData":[OSD([sQuery(id+"F0.wireOp",EDGE,"E4.sketch_text.stroke-5"),sQuery(id+"F0.wireOp",EDGE,"E4.sketch_text.stroke-6"),sQuery(id+"F0.wireOp",EDGE,"E4.sketch_text.stroke-7"),sQuery(id+"F0.wireOp",EDGE,"E4.sketch_text.stroke-8"),sQuery(id+"F0.wireOp",EDGE,"E4.sketch_text.stroke-9"),sQuery(id+"F0.wireOp",EDGE,"E4.sketch_text.stroke-10")])],"isStart":true}),makeQuery(id+"F5.opExtrude","SWEPT_FACE",FACE,{"disambiguationData":[OSD([sQuery(id+"F4.wireOp",EDGE,"E14.0.2")])]})]});
            var Q74;
            Q74=makeQuery(id+"F11.opBoolean","INTERSECT",EDGE,{"derivedFrom":[makeQuery(id+"F1.opExtrude","CAP_FACE",FACE,{"disambiguationData":[OSD([sQuery(id+"F0.wireOp",EDGE,"E4.sketch_text.stroke-11"),sQuery(id+"F0.wireOp",EDGE,"E4.sketch_text.stroke-12"),sQuery(id+"F0.wireOp",EDGE,"E4.sketch_text.stroke-13"),sQuery(id+"F0.wireOp",EDGE,"E4.sketch_text.stroke-14"),sQuery(id+"F0.wireOp",EDGE,"E4.sketch_text.stroke-15"),sQuery(id+"F0.wireOp",EDGE,"E4.sketch_text.stroke-16"),sQuery(id+"F0.wireOp",EDGE,"E4.sketch_text.stroke-17"),sQuery(id+"F0.wireOp",EDGE,"E4.sketch_text.stroke-18"),sQuery(id+"F0.wireOp",EDGE,"E4.sketch_text.stroke-19"),sQuery(id+"F0.wireOp",EDGE,"E4.sketch_text.stroke-20"),sQuery(id+"F0.wireOp",EDGE,"E4.sketch_text.stroke-21"),sQuery(id+"F0.wireOp",EDGE,"E4.sketch_text.stroke-22"),sQuery(id+"F0.wireOp",EDGE,"E4.sketch_text.stroke-23"),sQuery(id+"F0.wireOp",EDGE,"E4.sketch_text.stroke-24"),sQuery(id+"F0.wireOp",EDGE,"E4.sketch_text.stroke-25"),sQuery(id+"F0.wireOp",EDGE,"E4.sketch_text.stroke-26"),sQuery(id+"F0.wireOp",EDGE,"E4.sketch_text.stroke-27"),sQuery(id+"F0.wireOp",EDGE,"E4.sketch_text.stroke-28")])],"isStart":true}),makeQuery(id+"F5.opExtrude","SWEPT_FACE",FACE,{"disambiguationData":[OSD([sQuery(id+"F4.wireOp",EDGE,"E14.0.2")])]})]});
            var Q75;
            Q75=makeQuery(id+"F9.opBoolean","INTERSECT",EDGE,{"derivedFrom":[makeQuery(id+"F1.opExtrude","CAP_FACE",FACE,{"disambiguationData":[OSD([sQuery(id+"F0.wireOp",EDGE,"E2.sketch_text.stroke-116"),sQuery(id+"F0.wireOp",EDGE,"E2.sketch_text.stroke-117"),sQuery(id+"F0.wireOp",EDGE,"E2.sketch_text.stroke-118"),sQuery(id+"F0.wireOp",EDGE,"E2.sketch_text.stroke-119"),sQuery(id+"F0.wireOp",EDGE,"E2.sketch_text.stroke-120"),sQuery(id+"F0.wireOp",EDGE,"E2.sketch_text.stroke-121"),sQuery(id+"F0.wireOp",EDGE,"E2.sketch_text.stroke-122"),sQuery(id+"F0.wireOp",EDGE,"E2.sketch_text.stroke-123"),sQuery(id+"F0.wireOp",EDGE,"E2.sketch_text.stroke-124"),sQuery(id+"F0.wireOp",EDGE,"E2.sketch_text.stroke-125"),sQuery(id+"F0.wireOp",EDGE,"E2.sketch_text.stroke-126"),sQuery(id+"F0.wireOp",EDGE,"E2.sketch_text.stroke-127"),sQuery(id+"F0.wireOp",EDGE,"E2.sketch_text.stroke-128"),sQuery(id+"F0.wireOp",EDGE,"E2.sketch_text.stroke-129"),sQuery(id+"F0.wireOp",EDGE,"E2.sketch_text.stroke-130"),sQuery(id+"F0.wireOp",EDGE,"E2.sketch_text.stroke-131"),sQuery(id+"F0.wireOp",EDGE,"E2.sketch_text.stroke-132"),sQuery(id+"F0.wireOp",EDGE,"E2.sketch_text.stroke-133"),sQuery(id+"F0.wireOp",EDGE,"E2.sketch_text.stroke-134")])],"isStart":true}),makeQuery(id+"F5.opExtrude","SWEPT_FACE",FACE,{"disambiguationData":[OSD([sQuery(id+"F4.wireOp",EDGE,"E12.0.2")])]})]});
            var Q76;
            Q76=makeQuery(id+"F9.opBoolean","INTERSECT",EDGE,{"disambiguationData":[OD(1.0)],"derivedFrom":[makeQuery(id+"F1.opExtrude","CAP_FACE",FACE,{"disambiguationData":[OSD([sQuery(id+"F0.wireOp",EDGE,"E2.sketch_text.stroke-135"),sQuery(id+"F0.wireOp",EDGE,"E2.sketch_text.stroke-136"),sQuery(id+"F0.wireOp",EDGE,"E2.sketch_text.stroke-137"),sQuery(id+"F0.wireOp",EDGE,"E2.sketch_text.stroke-138"),sQuery(id+"F0.wireOp",EDGE,"E2.sketch_text.stroke-139"),sQuery(id+"F0.wireOp",EDGE,"E2.sketch_text.stroke-140"),sQuery(id+"F0.wireOp",EDGE,"E2.sketch_text.stroke-141"),sQuery(id+"F0.wireOp",EDGE,"E2.sketch_text.stroke-142"),sQuery(id+"F0.wireOp",EDGE,"E2.sketch_text.stroke-143"),sQuery(id+"F0.wireOp",EDGE,"E2.sketch_text.stroke-144"),sQuery(id+"F0.wireOp",EDGE,"E2.sketch_text.stroke-145"),sQuery(id+"F0.wireOp",EDGE,"E2.sketch_text.stroke-146"),sQuery(id+"F0.wireOp",EDGE,"E2.sketch_text.stroke-147"),sQuery(id+"F0.wireOp",EDGE,"E2.sketch_text.stroke-148"),sQuery(id+"F0.wireOp",EDGE,"E2.sketch_text.stroke-149"),sQuery(id+"F0.wireOp",EDGE,"E2.sketch_text.stroke-150"),sQuery(id+"F0.wireOp",EDGE,"E2.sketch_text.stroke-151"),sQuery(id+"F0.wireOp",EDGE,"E2.sketch_text.stroke-152"),sQuery(id+"F0.wireOp",EDGE,"E2.sketch_text.stroke-153"),sQuery(id+"F0.wireOp",EDGE,"E2.sketch_text.stroke-154"),sQuery(id+"F0.wireOp",EDGE,"E2.sketch_text.stroke-155"),sQuery(id+"F0.wireOp",EDGE,"E2.sketch_text.stroke-156"),sQuery(id+"F0.wireOp",EDGE,"E2.sketch_text.stroke-157"),sQuery(id+"F0.wireOp",EDGE,"E2.sketch_text.stroke-158"),sQuery(id+"F0.wireOp",EDGE,"E2.sketch_text.stroke-159"),sQuery(id+"F0.wireOp",EDGE,"E2.sketch_text.stroke-160"),sQuery(id+"F0.wireOp",EDGE,"E2.sketch_text.stroke-161"),sQuery(id+"F0.wireOp",EDGE,"E2.sketch_text.stroke-162"),sQuery(id+"F0.wireOp",EDGE,"E2.sketch_text.stroke-163"),sQuery(id+"F0.wireOp",EDGE,"E2.sketch_text.stroke-164"),sQuery(id+"F0.wireOp",EDGE,"E2.sketch_text.stroke-165"),sQuery(id+"F0.wireOp",EDGE,"E2.sketch_text.stroke-166"),sQuery(id+"F0.wireOp",EDGE,"E2.sketch_text.stroke-167"),sQuery(id+"F0.wireOp",EDGE,"E2.sketch_text.stroke-168"),sQuery(id+"F0.wireOp",EDGE,"E2.sketch_text.stroke-169"),sQuery(id+"F0.wireOp",EDGE,"E2.sketch_text.stroke-170")])],"isStart":true}),makeQuery(id+"F5.opExtrude","SWEPT_FACE",FACE,{"disambiguationData":[OSD([sQuery(id+"F4.wireOp",EDGE,"E12.0.2")])]})]});
            var Q77;
            Q77=makeQuery(id+"F9.opBoolean","INTERSECT",EDGE,{"disambiguationData":[OD(0.0)],"derivedFrom":[makeQuery(id+"F1.opExtrude","CAP_FACE",FACE,{"disambiguationData":[OSD([sQuery(id+"F0.wireOp",EDGE,"E2.sketch_text.stroke-135"),sQuery(id+"F0.wireOp",EDGE,"E2.sketch_text.stroke-136"),sQuery(id+"F0.wireOp",EDGE,"E2.sketch_text.stroke-137"),sQuery(id+"F0.wireOp",EDGE,"E2.sketch_text.stroke-138"),sQuery(id+"F0.wireOp",EDGE,"E2.sketch_text.stroke-139"),sQuery(id+"F0.wireOp",EDGE,"E2.sketch_text.stroke-140"),sQuery(id+"F0.wireOp",EDGE,"E2.sketch_text.stroke-141"),sQuery(id+"F0.wireOp",EDGE,"E2.sketch_text.stroke-142"),sQuery(id+"F0.wireOp",EDGE,"E2.sketch_text.stroke-143"),sQuery(id+"F0.wireOp",EDGE,"E2.sketch_text.stroke-144"),sQuery(id+"F0.wireOp",EDGE,"E2.sketch_text.stroke-145"),sQuery(id+"F0.wireOp",EDGE,"E2.sketch_text.stroke-146"),sQuery(id+"F0.wireOp",EDGE,"E2.sketch_text.stroke-147"),sQuery(id+"F0.wireOp",EDGE,"E2.sketch_text.stroke-148"),sQuery(id+"F0.wireOp",EDGE,"E2.sketch_text.stroke-149"),sQuery(id+"F0.wireOp",EDGE,"E2.sketch_text.stroke-150"),sQuery(id+"F0.wireOp",EDGE,"E2.sketch_text.stroke-151"),sQuery(id+"F0.wireOp",EDGE,"E2.sketch_text.stroke-152"),sQuery(id+"F0.wireOp",EDGE,"E2.sketch_text.stroke-153"),sQuery(id+"F0.wireOp",EDGE,"E2.sketch_text.stroke-154"),sQuery(id+"F0.wireOp",EDGE,"E2.sketch_text.stroke-155"),sQuery(id+"F0.wireOp",EDGE,"E2.sketch_text.stroke-156"),sQuery(id+"F0.wireOp",EDGE,"E2.sketch_text.stroke-157"),sQuery(id+"F0.wireOp",EDGE,"E2.sketch_text.stroke-158"),sQuery(id+"F0.wireOp",EDGE,"E2.sketch_text.stroke-159"),sQuery(id+"F0.wireOp",EDGE,"E2.sketch_text.stroke-160"),sQuery(id+"F0.wireOp",EDGE,"E2.sketch_text.stroke-161"),sQuery(id+"F0.wireOp",EDGE,"E2.sketch_text.stroke-162"),sQuery(id+"F0.wireOp",EDGE,"E2.sketch_text.stroke-163"),sQuery(id+"F0.wireOp",EDGE,"E2.sketch_text.stroke-164"),sQuery(id+"F0.wireOp",EDGE,"E2.sketch_text.stroke-165"),sQuery(id+"F0.wireOp",EDGE,"E2.sketch_text.stroke-166"),sQuery(id+"F0.wireOp",EDGE,"E2.sketch_text.stroke-167"),sQuery(id+"F0.wireOp",EDGE,"E2.sketch_text.stroke-168"),sQuery(id+"F0.wireOp",EDGE,"E2.sketch_text.stroke-169"),sQuery(id+"F0.wireOp",EDGE,"E2.sketch_text.stroke-170")])],"isStart":true}),makeQuery(id+"F5.opExtrude","SWEPT_FACE",FACE,{"disambiguationData":[OSD([sQuery(id+"F4.wireOp",EDGE,"E12.0.2")])]})]});
            var Q78;
            Q78=makeQuery(id+"F9.opBoolean","INTERSECT",EDGE,{"derivedFrom":[makeQuery(id+"F1.opExtrude","CAP_FACE",FACE,{"disambiguationData":[OSD([sQuery(id+"F0.wireOp",EDGE,"E2.sketch_text.stroke-176"),sQuery(id+"F0.wireOp",EDGE,"E2.sketch_text.stroke-177"),sQuery(id+"F0.wireOp",EDGE,"E2.sketch_text.stroke-178"),sQuery(id+"F0.wireOp",EDGE,"E2.sketch_text.stroke-179"),sQuery(id+"F0.wireOp",EDGE,"E2.sketch_text.stroke-180"),sQuery(id+"F0.wireOp",EDGE,"E2.sketch_text.stroke-181"),sQuery(id+"F0.wireOp",EDGE,"E2.sketch_text.stroke-182"),sQuery(id+"F0.wireOp",EDGE,"E2.sketch_text.stroke-183"),sQuery(id+"F0.wireOp",EDGE,"E2.sketch_text.stroke-184"),sQuery(id+"F0.wireOp",EDGE,"E2.sketch_text.stroke-185"),sQuery(id+"F0.wireOp",EDGE,"E2.sketch_text.stroke-186"),sQuery(id+"F0.wireOp",EDGE,"E2.sketch_text.stroke-187"),sQuery(id+"F0.wireOp",EDGE,"E2.sketch_text.stroke-188"),sQuery(id+"F0.wireOp",EDGE,"E2.sketch_text.stroke-189"),sQuery(id+"F0.wireOp",EDGE,"E2.sketch_text.stroke-190"),sQuery(id+"F0.wireOp",EDGE,"E2.sketch_text.stroke-191"),sQuery(id+"F0.wireOp",EDGE,"E2.sketch_text.stroke-192"),sQuery(id+"F0.wireOp",EDGE,"E2.sketch_text.stroke-193"),sQuery(id+"F0.wireOp",EDGE,"E2.sketch_text.stroke-194"),sQuery(id+"F0.wireOp",EDGE,"E2.sketch_text.stroke-195"),sQuery(id+"F0.wireOp",EDGE,"E2.sketch_text.stroke-196"),sQuery(id+"F0.wireOp",EDGE,"E2.sketch_text.stroke-197"),sQuery(id+"F0.wireOp",EDGE,"E2.sketch_text.stroke-198"),sQuery(id+"F0.wireOp",EDGE,"E2.sketch_text.stroke-199"),sQuery(id+"F0.wireOp",EDGE,"E2.sketch_text.stroke-200")])],"isStart":true}),makeQuery(id+"F5.opExtrude","SWEPT_FACE",FACE,{"disambiguationData":[OSD([sQuery(id+"F4.wireOp",EDGE,"E12.0.2")])]})]});
            var Q79;
            Q79=makeQuery(id+"F9.opBoolean","INTERSECT",EDGE,{"derivedFrom":[makeQuery(id+"F1.opExtrude","CAP_FACE",FACE,{"disambiguationData":[OSD([sQuery(id+"F0.wireOp",EDGE,"E2.sketch_text.stroke-171"),sQuery(id+"F0.wireOp",EDGE,"E2.sketch_text.stroke-172"),sQuery(id+"F0.wireOp",EDGE,"E2.sketch_text.stroke-173"),sQuery(id+"F0.wireOp",EDGE,"E2.sketch_text.stroke-174"),sQuery(id+"F0.wireOp",EDGE,"E2.sketch_text.stroke-175")])],"isStart":true}),makeQuery(id+"F5.opExtrude","SWEPT_FACE",FACE,{"disambiguationData":[OSD([sQuery(id+"F4.wireOp",EDGE,"E12.0.2")])]})]});
            var Q80;
            Q80=makeQuery(id+"F9.opBoolean","INTERSECT",EDGE,{"derivedFrom":[makeQuery(id+"F1.opExtrude","CAP_FACE",FACE,{"disambiguationData":[OSD([sQuery(id+"F0.wireOp",EDGE,"E2.sketch_text.stroke-214"),sQuery(id+"F0.wireOp",EDGE,"E2.sketch_text.stroke-215"),sQuery(id+"F0.wireOp",EDGE,"E2.sketch_text.stroke-216"),sQuery(id+"F0.wireOp",EDGE,"E2.sketch_text.stroke-217"),sQuery(id+"F0.wireOp",EDGE,"E2.sketch_text.stroke-218"),sQuery(id+"F0.wireOp",EDGE,"E2.sketch_text.stroke-219"),sQuery(id+"F0.wireOp",EDGE,"E2.sketch_text.stroke-220"),sQuery(id+"F0.wireOp",EDGE,"E2.sketch_text.stroke-221"),sQuery(id+"F0.wireOp",EDGE,"E2.sketch_text.stroke-222"),sQuery(id+"F0.wireOp",EDGE,"E2.sketch_text.stroke-223"),sQuery(id+"F0.wireOp",EDGE,"E2.sketch_text.stroke-224"),sQuery(id+"F0.wireOp",EDGE,"E2.sketch_text.stroke-225"),sQuery(id+"F0.wireOp",EDGE,"E2.sketch_text.stroke-226"),sQuery(id+"F0.wireOp",EDGE,"E2.sketch_text.stroke-227"),sQuery(id+"F0.wireOp",EDGE,"E2.sketch_text.stroke-228"),sQuery(id+"F0.wireOp",EDGE,"E2.sketch_text.stroke-229"),sQuery(id+"F0.wireOp",EDGE,"E2.sketch_text.stroke-230"),sQuery(id+"F0.wireOp",EDGE,"E2.sketch_text.stroke-231"),sQuery(id+"F0.wireOp",EDGE,"E2.sketch_text.stroke-232"),sQuery(id+"F0.wireOp",EDGE,"E2.sketch_text.stroke-233"),sQuery(id+"F0.wireOp",EDGE,"E2.sketch_text.stroke-234"),sQuery(id+"F0.wireOp",EDGE,"E2.sketch_text.stroke-235"),sQuery(id+"F0.wireOp",EDGE,"E2.sketch_text.stroke-236"),sQuery(id+"F0.wireOp",EDGE,"E2.sketch_text.stroke-237")])],"isStart":true}),makeQuery(id+"F5.opExtrude","SWEPT_FACE",FACE,{"disambiguationData":[OSD([sQuery(id+"F4.wireOp",EDGE,"E12.0.2")])]})]});
            var Q81;
            Q81=makeQuery(id+"F9.opBoolean","INTERSECT",EDGE,{"derivedFrom":[makeQuery(id+"F1.opExtrude","CAP_FACE",FACE,{"disambiguationData":[OSD([sQuery(id+"F0.wireOp",EDGE,"E2.sketch_text.stroke-251"),sQuery(id+"F0.wireOp",EDGE,"E2.sketch_text.stroke-252"),sQuery(id+"F0.wireOp",EDGE,"E2.sketch_text.stroke-253"),sQuery(id+"F0.wireOp",EDGE,"E2.sketch_text.stroke-254"),sQuery(id+"F0.wireOp",EDGE,"E2.sketch_text.stroke-255"),sQuery(id+"F0.wireOp",EDGE,"E2.sketch_text.stroke-256"),sQuery(id+"F0.wireOp",EDGE,"E2.sketch_text.stroke-257"),sQuery(id+"F0.wireOp",EDGE,"E2.sketch_text.stroke-258"),sQuery(id+"F0.wireOp",EDGE,"E2.sketch_text.stroke-259"),sQuery(id+"F0.wireOp",EDGE,"E2.sketch_text.stroke-260"),sQuery(id+"F0.wireOp",EDGE,"E2.sketch_text.stroke-261"),sQuery(id+"F0.wireOp",EDGE,"E2.sketch_text.stroke-262"),sQuery(id+"F0.wireOp",EDGE,"E2.sketch_text.stroke-263"),sQuery(id+"F0.wireOp",EDGE,"E2.sketch_text.stroke-264"),sQuery(id+"F0.wireOp",EDGE,"E2.sketch_text.stroke-265"),sQuery(id+"F0.wireOp",EDGE,"E2.sketch_text.stroke-266"),sQuery(id+"F0.wireOp",EDGE,"E2.sketch_text.stroke-267"),sQuery(id+"F0.wireOp",EDGE,"E2.sketch_text.stroke-268"),sQuery(id+"F0.wireOp",EDGE,"E2.sketch_text.stroke-269"),sQuery(id+"F0.wireOp",EDGE,"E2.sketch_text.stroke-270"),sQuery(id+"F0.wireOp",EDGE,"E2.sketch_text.stroke-271"),sQuery(id+"F0.wireOp",EDGE,"E2.sketch_text.stroke-272"),sQuery(id+"F0.wireOp",EDGE,"E2.sketch_text.stroke-273"),sQuery(id+"F0.wireOp",EDGE,"E2.sketch_text.stroke-274")])],"isStart":true}),makeQuery(id+"F5.opExtrude","SWEPT_FACE",FACE,{"disambiguationData":[OSD([sQuery(id+"F4.wireOp",EDGE,"E12.0.2")])]})]});
            var Q82;
            Q82=makeQuery(id+"F9.opBoolean","INTERSECT",EDGE,{"derivedFrom":[makeQuery(id+"F1.opExtrude","CAP_FACE",FACE,{"disambiguationData":[OSD([sQuery(id+"F0.wireOp",EDGE,"E2.sketch_text.stroke-295"),sQuery(id+"F0.wireOp",EDGE,"E2.sketch_text.stroke-296"),sQuery(id+"F0.wireOp",EDGE,"E2.sketch_text.stroke-297"),sQuery(id+"F0.wireOp",EDGE,"E2.sketch_text.stroke-298"),sQuery(id+"F0.wireOp",EDGE,"E2.sketch_text.stroke-299"),sQuery(id+"F0.wireOp",EDGE,"E2.sketch_text.stroke-300"),sQuery(id+"F0.wireOp",EDGE,"E2.sketch_text.stroke-301"),sQuery(id+"F0.wireOp",EDGE,"E2.sketch_text.stroke-302"),sQuery(id+"F0.wireOp",EDGE,"E2.sketch_text.stroke-303")])],"isStart":true}),makeQuery(id+"F5.opExtrude","SWEPT_FACE",FACE,{"disambiguationData":[OSD([sQuery(id+"F4.wireOp",EDGE,"E12.0.2")])]})]});
            var Q83;
            Q83=makeQuery(id+"F9.opBoolean","INTERSECT",EDGE,{"derivedFrom":[makeQuery(id+"F1.opExtrude","CAP_FACE",FACE,{"disambiguationData":[OSD([sQuery(id+"F0.wireOp",EDGE,"E2.sketch_text.stroke-304"),sQuery(id+"F0.wireOp",EDGE,"E2.sketch_text.stroke-305"),sQuery(id+"F0.wireOp",EDGE,"E2.sketch_text.stroke-306"),sQuery(id+"F0.wireOp",EDGE,"E2.sketch_text.stroke-307"),sQuery(id+"F0.wireOp",EDGE,"E2.sketch_text.stroke-308"),sQuery(id+"F0.wireOp",EDGE,"E2.sketch_text.stroke-309"),sQuery(id+"F0.wireOp",EDGE,"E2.sketch_text.stroke-310"),sQuery(id+"F0.wireOp",EDGE,"E2.sketch_text.stroke-311"),sQuery(id+"F0.wireOp",EDGE,"E2.sketch_text.stroke-312"),sQuery(id+"F0.wireOp",EDGE,"E2.sketch_text.stroke-313"),sQuery(id+"F0.wireOp",EDGE,"E2.sketch_text.stroke-314"),sQuery(id+"F0.wireOp",EDGE,"E2.sketch_text.stroke-315"),sQuery(id+"F0.wireOp",EDGE,"E2.sketch_text.stroke-316"),sQuery(id+"F0.wireOp",EDGE,"E2.sketch_text.stroke-317")])],"isStart":true}),makeQuery(id+"F5.opExtrude","SWEPT_FACE",FACE,{"disambiguationData":[OSD([sQuery(id+"F4.wireOp",EDGE,"E12.0.2")])]})]});
            var Q84;
            Q84=makeQuery(id+"F9.opBoolean","INTERSECT",EDGE,{"derivedFrom":[makeQuery(id+"F1.opExtrude","CAP_FACE",FACE,{"disambiguationData":[OSD([sQuery(id+"F0.wireOp",EDGE,"E2.sketch_text.stroke-318"),sQuery(id+"F0.wireOp",EDGE,"E2.sketch_text.stroke-319"),sQuery(id+"F0.wireOp",EDGE,"E2.sketch_text.stroke-320"),sQuery(id+"F0.wireOp",EDGE,"E2.sketch_text.stroke-321")])],"isStart":true}),makeQuery(id+"F5.opExtrude","SWEPT_FACE",FACE,{"disambiguationData":[OSD([sQuery(id+"F4.wireOp",EDGE,"E12.0.2")])]})]});
            var Q85;
            Q85=makeQuery(id+"F9.opBoolean","INTERSECT",EDGE,{"derivedFrom":[makeQuery(id+"F1.opExtrude","CAP_FACE",FACE,{"disambiguationData":[OSD([sQuery(id+"F0.wireOp",EDGE,"E2.sketch_text.stroke-322"),sQuery(id+"F0.wireOp",EDGE,"E2.sketch_text.stroke-323"),sQuery(id+"F0.wireOp",EDGE,"E2.sketch_text.stroke-324"),sQuery(id+"F0.wireOp",EDGE,"E2.sketch_text.stroke-325"),sQuery(id+"F0.wireOp",EDGE,"E2.sketch_text.stroke-326"),sQuery(id+"F0.wireOp",EDGE,"E2.sketch_text.stroke-327"),sQuery(id+"F0.wireOp",EDGE,"E2.sketch_text.stroke-328"),sQuery(id+"F0.wireOp",EDGE,"E2.sketch_text.stroke-329"),sQuery(id+"F0.wireOp",EDGE,"E2.sketch_text.stroke-330"),sQuery(id+"F0.wireOp",EDGE,"E2.sketch_text.stroke-331"),sQuery(id+"F0.wireOp",EDGE,"E2.sketch_text.stroke-332"),sQuery(id+"F0.wireOp",EDGE,"E2.sketch_text.stroke-333"),sQuery(id+"F0.wireOp",EDGE,"E2.sketch_text.stroke-334"),sQuery(id+"F0.wireOp",EDGE,"E2.sketch_text.stroke-335"),sQuery(id+"F0.wireOp",EDGE,"E2.sketch_text.stroke-336"),sQuery(id+"F0.wireOp",EDGE,"E2.sketch_text.stroke-337"),sQuery(id+"F0.wireOp",EDGE,"E2.sketch_text.stroke-338"),sQuery(id+"F0.wireOp",EDGE,"E2.sketch_text.stroke-339"),sQuery(id+"F0.wireOp",EDGE,"E2.sketch_text.stroke-340")])],"isStart":true}),makeQuery(id+"F6.opFillet","BLEND_FACE",FACE,{"disambiguationData":[OSD([sQuery(id+"F4.wireOp",EDGE,"E12.0.2"),sQuery(id+"F4.wireOp",EDGE,"E12.0.3")])]})]});
            chamfer(context, id + "F12", {"entities" : qUnion([Q0, Q1, Q2, Q3, Q4, Q5, Q6, Q7, Q8, Q9, Q10, Q11, Q12, Q13, Q14, Q15, Q16, Q17, Q18, Q19, Q20, Q21, Q22, Q23, Q24, Q25, Q26, Q27, Q28, Q29, Q30, Q31, Q32, Q33, Q34, Q35, Q36, Q37, Q38, Q39, Q40, Q41, Q42, Q43, Q44, Q45, Q46, Q47, Q48, Q49, Q50, Q51, Q52, Q53, Q54, Q55, Q56, Q57, Q58, Q59, Q60, Q61, Q62, Q63, Q64, Q65, Q66, Q67, Q68, Q69, Q70, Q71, Q72, Q73, Q74, Q75, Q76, Q77, Q78, Q79, Q80, Q81, Q82, Q83, Q84, Q85]), "chamferType" : ChamferType.TWO_OFFSETS, "width1" : 1.5 * mm, "oppositeDirection" : false, "width2" : 2 * mm, "tangentPropagation" : true});
        }
        {
            var Q0;
            Q0=makeQuery(id+"F9.opBoolean","INTERSECT",EDGE,{"derivedFrom":[makeQuery(id+"F1.opExtrude","CAP_FACE",FACE,{"disambiguationData":[OSD([sQuery(id+"F0.wireOp",EDGE,"E2.sketch_text.stroke-0"),sQuery(id+"F0.wireOp",EDGE,"E2.sketch_text.stroke-1"),sQuery(id+"F0.wireOp",EDGE,"E2.sketch_text.stroke-2"),sQuery(id+"F0.wireOp",EDGE,"E2.sketch_text.stroke-3"),sQuery(id+"F0.wireOp",EDGE,"E2.sketch_text.stroke-4"),sQuery(id+"F0.wireOp",EDGE,"E2.sketch_text.stroke-5"),sQuery(id+"F0.wireOp",EDGE,"E2.sketch_text.stroke-6"),sQuery(id+"F0.wireOp",EDGE,"E2.sketch_text.stroke-7"),sQuery(id+"F0.wireOp",EDGE,"E2.sketch_text.stroke-8"),sQuery(id+"F0.wireOp",EDGE,"E2.sketch_text.stroke-9"),sQuery(id+"F0.wireOp",EDGE,"E2.sketch_text.stroke-10"),sQuery(id+"F0.wireOp",EDGE,"E2.sketch_text.stroke-11"),sQuery(id+"F0.wireOp",EDGE,"E2.sketch_text.stroke-12"),sQuery(id+"F0.wireOp",EDGE,"E2.sketch_text.stroke-13"),sQuery(id+"F0.wireOp",EDGE,"E2.sketch_text.stroke-14"),sQuery(id+"F0.wireOp",EDGE,"E2.sketch_text.stroke-15"),sQuery(id+"F0.wireOp",EDGE,"E2.sketch_text.stroke-16"),sQuery(id+"F0.wireOp",EDGE,"E2.sketch_text.stroke-17")])],"isStart":true}),makeQuery(id+"F6.opFillet","BLEND_FACE",FACE,{"disambiguationData":[OSD([sQuery(id+"F4.wireOp",EDGE,"E12.0.1"),sQuery(id+"F4.wireOp",EDGE,"E12.0.2")])]})]});
            chamfer(context, id + "F13", {"entities" : qUnion([Q0]), "width" : 1 * mm, "tangentPropagation" : true});
        }
        {
            var Q0;
            {var subQ0=sQuery(id+"F4.wireOp",EDGE,"E11.0.0");Q0=makeQuery(id+"F8.opBoolean","SPLIT",EDGE,{"disambiguationData":[TD([makeQuery(id+"F1.opExtrude","SWEPT_FACE",FACE,{"disambiguationData":[OSD([sQuery(id+"F0.wireOp",EDGE,"E1.sketch_text.stroke-7")])]})])],"derivedFrom":makeQuery(id+"F5.opExtrude","CAP_EDGE",EDGE,{"disambiguationData":[OSD([subQ0])],"isStart":true})});}
            var Q1;
            {var subQ0=sQuery(id+"F4.wireOp",EDGE,"E11.0.2");Q1=makeQuery(id+"F8.opBoolean","SPLIT",EDGE,{"disambiguationData":[TD([makeQuery(id+"F1.opExtrude","SWEPT_FACE",FACE,{"disambiguationData":[OSD([sQuery(id+"F0.wireOp",EDGE,"E1.sketch_text.stroke-43")])]})])],"derivedFrom":makeQuery(id+"F5.opExtrude","CAP_EDGE",EDGE,{"disambiguationData":[OSD([subQ0])],"isStart":true})});}
            var Q2;
            Q2=makeQuery(id+"F5.opExtrude","CAP_EDGE",EDGE,{"disambiguationData":[OSD([sQuery(id+"F4.wireOp",EDGE,"E11.0.1")])],"isStart":true});
            var Q3;
            {var subQ0=sQuery(id+"F4.wireOp",EDGE,"E11.0.2");Q3=makeQuery(id+"F8.opBoolean","SPLIT",EDGE,{"disambiguationData":[TD([makeQuery(id+"F1.opExtrude","SWEPT_FACE",FACE,{"disambiguationData":[OSD([sQuery(id+"F0.wireOp",EDGE,"E1.sketch_text.stroke-70")])]})])],"derivedFrom":makeQuery(id+"F5.opExtrude","CAP_EDGE",EDGE,{"disambiguationData":[OSD([subQ0])],"isStart":true})});}
            var Q4;
            {var subQ0=sQuery(id+"F4.wireOp",EDGE,"E11.0.2");Q4=makeQuery(id+"F8.opBoolean","SPLIT",EDGE,{"disambiguationData":[TD([makeQuery(id+"F1.opExtrude","SWEPT_FACE",FACE,{"disambiguationData":[OSD([sQuery(id+"F0.wireOp",EDGE,"E1.sketch_text.stroke-76")])]})])],"derivedFrom":makeQuery(id+"F5.opExtrude","CAP_EDGE",EDGE,{"disambiguationData":[OSD([subQ0])],"isStart":true})});}
            var Q5;
            {var subQ0=sQuery(id+"F4.wireOp",EDGE,"E11.0.2");Q5=makeQuery(id+"F8.opBoolean","SPLIT",EDGE,{"disambiguationData":[TD([makeQuery(id+"F1.opExtrude","SWEPT_FACE",FACE,{"disambiguationData":[OSD([sQuery(id+"F0.wireOp",EDGE,"E1.sketch_text.stroke-126")])]})])],"derivedFrom":makeQuery(id+"F5.opExtrude","CAP_EDGE",EDGE,{"disambiguationData":[OSD([subQ0])],"isStart":true})});}
            var Q6;
            {var subQ0=sQuery(id+"F4.wireOp",EDGE,"E11.0.2");Q6=makeQuery(id+"F8.opBoolean","SPLIT",EDGE,{"disambiguationData":[TD([makeQuery(id+"F1.opExtrude","SWEPT_FACE",FACE,{"disambiguationData":[OSD([sQuery(id+"F0.wireOp",EDGE,"E1.sketch_text.stroke-99")])]})])],"derivedFrom":makeQuery(id+"F5.opExtrude","CAP_EDGE",EDGE,{"disambiguationData":[OSD([subQ0])],"isStart":true})});}
            var Q7;
            {var subQ0=sQuery(id+"F4.wireOp",EDGE,"E11.0.2");Q7=makeQuery(id+"F8.opBoolean","SPLIT",EDGE,{"disambiguationData":[TD([makeQuery(id+"F1.opExtrude","SWEPT_FACE",FACE,{"disambiguationData":[OSD([sQuery(id+"F0.wireOp",EDGE,"E1.sketch_text.stroke-152")])]})])],"derivedFrom":makeQuery(id+"F5.opExtrude","CAP_EDGE",EDGE,{"disambiguationData":[OSD([subQ0])],"isStart":true})});}
            var Q8;
            {var subQ0=sQuery(id+"F4.wireOp",EDGE,"E11.0.0");Q8=makeQuery(id+"F8.opBoolean","SPLIT",EDGE,{"disambiguationData":[TD([makeQuery(id+"F1.opExtrude","SWEPT_FACE",FACE,{"disambiguationData":[OSD([sQuery(id+"F0.wireOp",EDGE,"E1.sketch_text.stroke-99")])]})])],"derivedFrom":makeQuery(id+"F5.opExtrude","CAP_EDGE",EDGE,{"disambiguationData":[OSD([subQ0])],"isStart":true})});}
            var Q9;
            {var subQ0=sQuery(id+"F4.wireOp",EDGE,"E11.0.2");Q9=makeQuery(id+"F8.opBoolean","SPLIT",EDGE,{"disambiguationData":[TD([makeQuery(id+"F1.opExtrude","SWEPT_FACE",FACE,{"disambiguationData":[OSD([sQuery(id+"F0.wireOp",EDGE,"E1.sketch_text.stroke-101")])]})])],"derivedFrom":makeQuery(id+"F5.opExtrude","CAP_EDGE",EDGE,{"disambiguationData":[OSD([subQ0])],"isStart":true})});}
            var Q10;
            {var subQ0=sQuery(id+"F4.wireOp",EDGE,"E11.0.2");Q10=makeQuery(id+"F8.opBoolean","SPLIT",EDGE,{"disambiguationData":[TD([makeQuery(id+"F1.opExtrude","SWEPT_FACE",FACE,{"disambiguationData":[OSD([sQuery(id+"F0.wireOp",EDGE,"E1.sketch_text.stroke-56")])]})])],"derivedFrom":makeQuery(id+"F5.opExtrude","CAP_EDGE",EDGE,{"disambiguationData":[OSD([subQ0])],"isStart":true})});}
            var Q11;
            {var subQ0=sQuery(id+"F4.wireOp",EDGE,"E10.0.0");Q11=makeQuery(id+"F7.opBoolean","SPLIT",EDGE,{"disambiguationData":[TD([makeQuery(id+"F1.opExtrude","SWEPT_FACE",FACE,{"disambiguationData":[OSD([sQuery(id+"F0.wireOp",EDGE,"E0.sketch_text.stroke-103")])]})])],"derivedFrom":makeQuery(id+"F5.opExtrude","CAP_EDGE",EDGE,{"disambiguationData":[OSD([subQ0])],"isStart":true})});}
            var Q12;
            {var subQ0=sQuery(id+"F4.wireOp",EDGE,"E10.0.0");Q12=makeQuery(id+"F7.opBoolean","SPLIT",EDGE,{"disambiguationData":[TD([makeQuery(id+"F1.opExtrude","SWEPT_FACE",FACE,{"disambiguationData":[OSD([sQuery(id+"F0.wireOp",EDGE,"E0.sketch_text.stroke-192")])]})])],"derivedFrom":makeQuery(id+"F5.opExtrude","CAP_EDGE",EDGE,{"disambiguationData":[OSD([subQ0])],"isStart":true})});}
            var Q13;
            {var subQ0=sQuery(id+"F4.wireOp",EDGE,"E10.0.2");Q13=makeQuery(id+"F7.opBoolean","SPLIT",EDGE,{"disambiguationData":[TD([makeQuery(id+"F1.opExtrude","SWEPT_FACE",FACE,{"disambiguationData":[OSD([sQuery(id+"F0.wireOp",EDGE,"E0.sketch_text.stroke-192")])]})])],"derivedFrom":makeQuery(id+"F5.opExtrude","CAP_EDGE",EDGE,{"disambiguationData":[OSD([subQ0])],"isStart":true})});}
            var Q14;
            {var subQ0=sQuery(id+"F4.wireOp",EDGE,"E10.0.2");Q14=makeQuery(id+"F7.opBoolean","SPLIT",EDGE,{"disambiguationData":[TD([makeQuery(id+"F1.opExtrude","SWEPT_FACE",FACE,{"disambiguationData":[OSD([sQuery(id+"F0.wireOp",EDGE,"E0.sketch_text.stroke-182")])]})])],"derivedFrom":makeQuery(id+"F5.opExtrude","CAP_EDGE",EDGE,{"disambiguationData":[OSD([subQ0])],"isStart":true})});}
            var Q15;
            {var subQ0=sQuery(id+"F4.wireOp",EDGE,"E10.0.2");Q15=makeQuery(id+"F7.opBoolean","SPLIT",EDGE,{"disambiguationData":[TD([makeQuery(id+"F1.opExtrude","SWEPT_FACE",FACE,{"disambiguationData":[OSD([sQuery(id+"F0.wireOp",EDGE,"E0.sketch_text.stroke-129")])]})])],"derivedFrom":makeQuery(id+"F5.opExtrude","CAP_EDGE",EDGE,{"disambiguationData":[OSD([subQ0])],"isStart":true})});}
            var Q16;
            {var subQ0=sQuery(id+"F4.wireOp",EDGE,"E10.0.2");Q16=makeQuery(id+"F7.opBoolean","SPLIT",EDGE,{"disambiguationData":[TD([makeQuery(id+"F1.opExtrude","SWEPT_FACE",FACE,{"disambiguationData":[OSD([sQuery(id+"F0.wireOp",EDGE,"E0.sketch_text.stroke-97")])]})])],"derivedFrom":makeQuery(id+"F5.opExtrude","CAP_EDGE",EDGE,{"disambiguationData":[OSD([subQ0])],"isStart":true})});}
            var Q17;
            {var subQ0=sQuery(id+"F4.wireOp",EDGE,"E10.0.2");Q17=makeQuery(id+"F7.opBoolean","SPLIT",EDGE,{"disambiguationData":[TD([makeQuery(id+"F1.opExtrude","SWEPT_FACE",FACE,{"disambiguationData":[OSD([sQuery(id+"F0.wireOp",EDGE,"E0.sketch_text.stroke-53")])]})])],"derivedFrom":makeQuery(id+"F5.opExtrude","CAP_EDGE",EDGE,{"disambiguationData":[OSD([subQ0])],"isStart":true})});}
            var Q18;
            {var subQ0=sQuery(id+"F4.wireOp",EDGE,"E10.0.2");Q18=makeQuery(id+"F7.opBoolean","SPLIT",EDGE,{"disambiguationData":[TD([makeQuery(id+"F1.opExtrude","SWEPT_FACE",FACE,{"disambiguationData":[OSD([sQuery(id+"F0.wireOp",EDGE,"E0.sketch_text.stroke-1")])]})])],"derivedFrom":makeQuery(id+"F5.opExtrude","CAP_EDGE",EDGE,{"disambiguationData":[OSD([subQ0])],"isStart":true})});}
            var Q19;
            {var subQ0=sQuery(id+"F4.wireOp",EDGE,"E10.0.2");Q19=makeQuery(id+"F7.opBoolean","SPLIT",EDGE,{"disambiguationData":[TD([makeQuery(id+"F1.opExtrude","SWEPT_FACE",FACE,{"disambiguationData":[OSD([sQuery(id+"F0.wireOp",EDGE,"E0.sketch_text.stroke-29")])]})])],"derivedFrom":makeQuery(id+"F5.opExtrude","CAP_EDGE",EDGE,{"disambiguationData":[OSD([subQ0])],"isStart":true})});}
            var Q20;
            {var subQ0=sQuery(id+"F4.wireOp",EDGE,"E10.0.2");Q20=makeQuery(id+"F7.opBoolean","SPLIT",EDGE,{"disambiguationData":[TD([makeQuery(id+"F1.opExtrude","SWEPT_FACE",FACE,{"disambiguationData":[OSD([sQuery(id+"F0.wireOp",EDGE,"E0.sketch_text.stroke-32")])]})])],"derivedFrom":makeQuery(id+"F5.opExtrude","CAP_EDGE",EDGE,{"disambiguationData":[OSD([subQ0])],"isStart":true})});}
            var Q21;
            {var subQ0=sQuery(id+"F4.wireOp",EDGE,"E10.0.0");Q21=makeQuery(id+"F7.opBoolean","SPLIT",EDGE,{"disambiguationData":[TD([makeQuery(id+"F1.opExtrude","SWEPT_FACE",FACE,{"disambiguationData":[OSD([sQuery(id+"F0.wireOp",EDGE,"E0.sketch_text.stroke-1")])]})])],"derivedFrom":makeQuery(id+"F5.opExtrude","CAP_EDGE",EDGE,{"disambiguationData":[OSD([subQ0])],"isStart":true})});}
            var Q22;
            {var subQ0=sQuery(id+"F4.wireOp",EDGE,"E12.0.0");Q22=makeQuery(id+"F9.opBoolean","SPLIT",EDGE,{"disambiguationData":[TD([makeQuery(id+"F1.opExtrude","SWEPT_FACE",FACE,{"disambiguationData":[OSD([sQuery(id+"F0.wireOp",EDGE,"E2.sketch_text.stroke-0")])]})])],"derivedFrom":makeQuery(id+"F5.opExtrude","CAP_EDGE",EDGE,{"disambiguationData":[OSD([subQ0])],"isStart":true})});}
            var Q23;
            {var subQ0=sQuery(id+"F4.wireOp",EDGE,"E12.0.0");Q23=makeQuery(id+"F9.opBoolean","SPLIT",EDGE,{"disambiguationData":[TD([makeQuery(id+"F1.opExtrude","SWEPT_FACE",FACE,{"disambiguationData":[OSD([sQuery(id+"F0.wireOp",EDGE,"E2.sketch_text.stroke-171")])]})])],"derivedFrom":makeQuery(id+"F5.opExtrude","CAP_EDGE",EDGE,{"disambiguationData":[OSD([subQ0])],"isStart":true})});}
            var Q24;
            {var subQ0=sQuery(id+"F4.wireOp",EDGE,"E12.0.0");Q24=makeQuery(id+"F9.opBoolean","SPLIT",EDGE,{"disambiguationData":[TD([makeQuery(id+"F1.opExtrude","SWEPT_FACE",FACE,{"disambiguationData":[OSD([sQuery(id+"F0.wireOp",EDGE,"E2.sketch_text.stroke-319")])]})])],"derivedFrom":makeQuery(id+"F5.opExtrude","CAP_EDGE",EDGE,{"disambiguationData":[OSD([subQ0])],"isStart":true})});}
            var Q25;
            {var subQ0=sQuery(id+"F4.wireOp",EDGE,"E12.0.2");Q25=makeQuery(id+"F9.opBoolean","SPLIT",EDGE,{"disambiguationData":[TD([makeQuery(id+"F1.opExtrude","SWEPT_FACE",FACE,{"disambiguationData":[OSD([sQuery(id+"F0.wireOp",EDGE,"E2.sketch_text.stroke-319")])]})])],"derivedFrom":makeQuery(id+"F5.opExtrude","CAP_EDGE",EDGE,{"disambiguationData":[OSD([subQ0])],"isStart":true})});}
            var Q26;
            {var subQ0=sQuery(id+"F4.wireOp",EDGE,"E12.0.2");Q26=makeQuery(id+"F9.opBoolean","SPLIT",EDGE,{"disambiguationData":[TD([makeQuery(id+"F1.opExtrude","SWEPT_FACE",FACE,{"disambiguationData":[OSD([sQuery(id+"F0.wireOp",EDGE,"E2.sketch_text.stroke-309")])]})])],"derivedFrom":makeQuery(id+"F5.opExtrude","CAP_EDGE",EDGE,{"disambiguationData":[OSD([subQ0])],"isStart":true})});}
            var Q27;
            {var subQ0=sQuery(id+"F4.wireOp",EDGE,"E12.0.2");Q27=makeQuery(id+"F9.opBoolean","SPLIT",EDGE,{"disambiguationData":[TD([makeQuery(id+"F1.opExtrude","SWEPT_FACE",FACE,{"disambiguationData":[OSD([sQuery(id+"F0.wireOp",EDGE,"E2.sketch_text.stroke-256")])]})])],"derivedFrom":makeQuery(id+"F5.opExtrude","CAP_EDGE",EDGE,{"disambiguationData":[OSD([subQ0])],"isStart":true})});}
            var Q28;
            {var subQ0=sQuery(id+"F4.wireOp",EDGE,"E12.0.2");Q28=makeQuery(id+"F9.opBoolean","SPLIT",EDGE,{"disambiguationData":[TD([makeQuery(id+"F1.opExtrude","SWEPT_FACE",FACE,{"disambiguationData":[OSD([sQuery(id+"F0.wireOp",EDGE,"E2.sketch_text.stroke-219")])]})])],"derivedFrom":makeQuery(id+"F5.opExtrude","CAP_EDGE",EDGE,{"disambiguationData":[OSD([subQ0])],"isStart":true})});}
            var Q29;
            {var subQ0=sQuery(id+"F4.wireOp",EDGE,"E12.0.2");Q29=makeQuery(id+"F9.opBoolean","SPLIT",EDGE,{"disambiguationData":[TD([makeQuery(id+"F1.opExtrude","SWEPT_FACE",FACE,{"disambiguationData":[OSD([sQuery(id+"F0.wireOp",EDGE,"E2.sketch_text.stroke-171")])]})])],"derivedFrom":makeQuery(id+"F5.opExtrude","CAP_EDGE",EDGE,{"disambiguationData":[OSD([subQ0])],"isStart":true})});}
            var Q30;
            {var subQ0=sQuery(id+"F4.wireOp",EDGE,"E12.0.2");Q30=makeQuery(id+"F9.opBoolean","SPLIT",EDGE,{"disambiguationData":[TD([makeQuery(id+"F1.opExtrude","SWEPT_FACE",FACE,{"disambiguationData":[OSD([sQuery(id+"F0.wireOp",EDGE,"E2.sketch_text.stroke-139")])]})])],"derivedFrom":makeQuery(id+"F5.opExtrude","CAP_EDGE",EDGE,{"disambiguationData":[OSD([subQ0])],"isStart":true})});}
            var Q31;
            {var subQ0=sQuery(id+"F4.wireOp",EDGE,"E12.0.2");Q31=makeQuery(id+"F9.opBoolean","SPLIT",EDGE,{"disambiguationData":[TD([makeQuery(id+"F1.opExtrude","SWEPT_FACE",FACE,{"disambiguationData":[OSD([sQuery(id+"F0.wireOp",EDGE,"E2.sketch_text.stroke-99")])]})])],"derivedFrom":makeQuery(id+"F5.opExtrude","CAP_EDGE",EDGE,{"disambiguationData":[OSD([subQ0])],"isStart":true})});}
            var Q32;
            {var subQ0=sQuery(id+"F4.wireOp",EDGE,"E12.0.2");Q32=makeQuery(id+"F9.opBoolean","SPLIT",EDGE,{"disambiguationData":[TD([makeQuery(id+"F1.opExtrude","SWEPT_FACE",FACE,{"disambiguationData":[OSD([sQuery(id+"F0.wireOp",EDGE,"E2.sketch_text.stroke-41")])]})])],"derivedFrom":makeQuery(id+"F5.opExtrude","CAP_EDGE",EDGE,{"disambiguationData":[OSD([subQ0])],"isStart":true})});}
            var Q33;
            {var subQ0=sQuery(id+"F4.wireOp",EDGE,"E12.0.2");Q33=makeQuery(id+"F9.opBoolean","SPLIT",EDGE,{"disambiguationData":[TD([makeQuery(id+"F1.opExtrude","SWEPT_FACE",FACE,{"disambiguationData":[OSD([sQuery(id+"F0.wireOp",EDGE,"E2.sketch_text.stroke-173")])]})])],"derivedFrom":makeQuery(id+"F5.opExtrude","CAP_EDGE",EDGE,{"disambiguationData":[OSD([subQ0])],"isStart":true})});}
            var Q34;
            {var subQ0=sQuery(id+"F4.wireOp",EDGE,"E12.0.2");Q34=makeQuery(id+"F9.opBoolean","SPLIT",EDGE,{"disambiguationData":[TD([makeQuery(id+"F1.opExtrude","SWEPT_FACE",FACE,{"disambiguationData":[OSD([sQuery(id+"F0.wireOp",EDGE,"E2.sketch_text.stroke-143")])]})])],"derivedFrom":makeQuery(id+"F5.opExtrude","CAP_EDGE",EDGE,{"disambiguationData":[OSD([subQ0])],"isStart":true})});}
            var Q35;
            {var subQ0=sQuery(id+"F4.wireOp",EDGE,"E12.0.2");Q35=makeQuery(id+"F9.opBoolean","SPLIT",EDGE,{"disambiguationData":[TD([makeQuery(id+"F1.opExtrude","SWEPT_FACE",FACE,{"disambiguationData":[OSD([sQuery(id+"F0.wireOp",EDGE,"E2.sketch_text.stroke-118")])]})])],"derivedFrom":makeQuery(id+"F5.opExtrude","CAP_EDGE",EDGE,{"disambiguationData":[OSD([subQ0])],"isStart":true})});}
            var Q36;
            {var subQ0=sQuery(id+"F4.wireOp",EDGE,"E12.0.2");Q36=makeQuery(id+"F9.opBoolean","SPLIT",EDGE,{"disambiguationData":[TD([makeQuery(id+"F1.opExtrude","SWEPT_FACE",FACE,{"disambiguationData":[OSD([sQuery(id+"F0.wireOp",EDGE,"E2.sketch_text.stroke-96")])]})])],"derivedFrom":makeQuery(id+"F5.opExtrude","CAP_EDGE",EDGE,{"disambiguationData":[OSD([subQ0])],"isStart":true})});}
            var Q37;
            {var subQ0=sQuery(id+"F4.wireOp",EDGE,"E12.0.2");Q37=makeQuery(id+"F9.opBoolean","SPLIT",EDGE,{"disambiguationData":[TD([makeQuery(id+"F1.opExtrude","SWEPT_FACE",FACE,{"disambiguationData":[OSD([sQuery(id+"F0.wireOp",EDGE,"E2.sketch_text.stroke-45")])]})])],"derivedFrom":makeQuery(id+"F5.opExtrude","CAP_EDGE",EDGE,{"disambiguationData":[OSD([subQ0])],"isStart":true})});}
            var Q38;
            {var subQ0=sQuery(id+"F4.wireOp",EDGE,"E12.0.2");Q38=makeQuery(id+"F9.opBoolean","SPLIT",EDGE,{"disambiguationData":[TD([makeQuery(id+"F1.opExtrude","SWEPT_FACE",FACE,{"disambiguationData":[OSD([sQuery(id+"F0.wireOp",EDGE,"E2.sketch_text.stroke-20")])]})])],"derivedFrom":makeQuery(id+"F5.opExtrude","CAP_EDGE",EDGE,{"disambiguationData":[OSD([subQ0])],"isStart":true})});}
            var Q39;
            {var subQ0=sQuery(id+"F4.wireOp",EDGE,"E12.0.2");Q39=makeQuery(id+"F9.opBoolean","SPLIT",EDGE,{"disambiguationData":[TD([makeQuery(id+"F1.opExtrude","SWEPT_FACE",FACE,{"disambiguationData":[OSD([sQuery(id+"F0.wireOp",EDGE,"E2.sketch_text.stroke-2")])]})])],"derivedFrom":makeQuery(id+"F5.opExtrude","CAP_EDGE",EDGE,{"disambiguationData":[OSD([subQ0])],"isStart":true})});}
            var Q40;
            Q40=makeQuery(id+"F5.opExtrude","CAP_EDGE",EDGE,{"disambiguationData":[OSD([sQuery(id+"F4.wireOp",EDGE,"E12.0.1")])],"isStart":true});
            var Q41;
            {var subQ0=sQuery(id+"F4.wireOp",EDGE,"E13.0.2");Q41=makeQuery(id+"F10.opBoolean","SPLIT",EDGE,{"disambiguationData":[TD([makeQuery(id+"F1.opExtrude","SWEPT_FACE",FACE,{"disambiguationData":[OSD([sQuery(id+"F0.wireOp",EDGE,"E3.sketch_text.stroke-43")])]})])],"derivedFrom":makeQuery(id+"F5.opExtrude","CAP_EDGE",EDGE,{"disambiguationData":[OSD([subQ0])],"isStart":true})});}
            var Q42;
            {var subQ0=sQuery(id+"F4.wireOp",EDGE,"E13.0.2");Q42=makeQuery(id+"F10.opBoolean","SPLIT",EDGE,{"disambiguationData":[TD([makeQuery(id+"F1.opExtrude","SWEPT_FACE",FACE,{"disambiguationData":[OSD([sQuery(id+"F0.wireOp",EDGE,"E3.sketch_text.stroke-52")])]})])],"derivedFrom":makeQuery(id+"F5.opExtrude","CAP_EDGE",EDGE,{"disambiguationData":[OSD([subQ0])],"isStart":true})});}
            var Q43;
            {var subQ0=sQuery(id+"F4.wireOp",EDGE,"E13.0.2");Q43=makeQuery(id+"F10.opBoolean","SPLIT",EDGE,{"disambiguationData":[TD([makeQuery(id+"F1.opExtrude","SWEPT_FACE",FACE,{"disambiguationData":[OSD([sQuery(id+"F0.wireOp",EDGE,"E3.sketch_text.stroke-73")])]})])],"derivedFrom":makeQuery(id+"F5.opExtrude","CAP_EDGE",EDGE,{"disambiguationData":[OSD([subQ0])],"isStart":true})});}
            var Q44;
            {var subQ0=sQuery(id+"F4.wireOp",EDGE,"E13.0.2");Q44=makeQuery(id+"F10.opBoolean","SPLIT",EDGE,{"disambiguationData":[TD([makeQuery(id+"F1.opExtrude","SWEPT_FACE",FACE,{"disambiguationData":[OSD([sQuery(id+"F0.wireOp",EDGE,"E3.sketch_text.stroke-111")])]})])],"derivedFrom":makeQuery(id+"F5.opExtrude","CAP_EDGE",EDGE,{"disambiguationData":[OSD([subQ0])],"isStart":true})});}
            var Q45;
            {var subQ0=sQuery(id+"F4.wireOp",EDGE,"E13.0.2");Q45=makeQuery(id+"F10.opBoolean","SPLIT",EDGE,{"disambiguationData":[TD([makeQuery(id+"F1.opExtrude","SWEPT_FACE",FACE,{"disambiguationData":[OSD([sQuery(id+"F0.wireOp",EDGE,"E3.sketch_text.stroke-118")])]})])],"derivedFrom":makeQuery(id+"F5.opExtrude","CAP_EDGE",EDGE,{"disambiguationData":[OSD([subQ0])],"isStart":true})});}
            var Q46;
            {var subQ0=sQuery(id+"F4.wireOp",EDGE,"E13.0.2");Q46=makeQuery(id+"F10.opBoolean","SPLIT",EDGE,{"disambiguationData":[TD([makeQuery(id+"F1.opExtrude","SWEPT_FACE",FACE,{"disambiguationData":[OSD([sQuery(id+"F0.wireOp",EDGE,"E3.sketch_text.stroke-131")])]})])],"derivedFrom":makeQuery(id+"F5.opExtrude","CAP_EDGE",EDGE,{"disambiguationData":[OSD([subQ0])],"isStart":true})});}
            var Q47;
            {var subQ0=sQuery(id+"F4.wireOp",EDGE,"E13.0.2");Q47=makeQuery(id+"F10.opBoolean","SPLIT",EDGE,{"disambiguationData":[TD([makeQuery(id+"F1.opExtrude","SWEPT_FACE",FACE,{"disambiguationData":[OSD([sQuery(id+"F0.wireOp",EDGE,"E3.sketch_text.stroke-153")])]})])],"derivedFrom":makeQuery(id+"F5.opExtrude","CAP_EDGE",EDGE,{"disambiguationData":[OSD([subQ0])],"isStart":true})});}
            var Q48;
            {var subQ0=sQuery(id+"F4.wireOp",EDGE,"E13.0.2");Q48=makeQuery(id+"F10.opBoolean","SPLIT",EDGE,{"disambiguationData":[TD([makeQuery(id+"F1.opExtrude","SWEPT_FACE",FACE,{"disambiguationData":[OSD([sQuery(id+"F0.wireOp",EDGE,"E3.sketch_text.stroke-181")])]})])],"derivedFrom":makeQuery(id+"F5.opExtrude","CAP_EDGE",EDGE,{"disambiguationData":[OSD([subQ0])],"isStart":true})});}
            var Q49;
            {var subQ0=sQuery(id+"F4.wireOp",EDGE,"E13.0.0");Q49=makeQuery(id+"F10.opBoolean","SPLIT",EDGE,{"disambiguationData":[TD([makeQuery(id+"F1.opExtrude","SWEPT_FACE",FACE,{"disambiguationData":[OSD([sQuery(id+"F0.wireOp",EDGE,"E3.sketch_text.stroke-153")])]})])],"derivedFrom":makeQuery(id+"F5.opExtrude","CAP_EDGE",EDGE,{"disambiguationData":[OSD([subQ0])],"isStart":true})});}
            var Q50;
            {var subQ0=sQuery(id+"F4.wireOp",EDGE,"E13.0.0");Q50=makeQuery(id+"F10.opBoolean","SPLIT",EDGE,{"disambiguationData":[TD([makeQuery(id+"F1.opExtrude","SWEPT_FACE",FACE,{"disambiguationData":[OSD([sQuery(id+"F0.wireOp",EDGE,"E3.sketch_text.stroke-147")])]})])],"derivedFrom":makeQuery(id+"F5.opExtrude","CAP_EDGE",EDGE,{"disambiguationData":[OSD([subQ0])],"isStart":true})});}
            var Q51;
            {var subQ0=sQuery(id+"F4.wireOp",EDGE,"E13.0.0");Q51=makeQuery(id+"F10.opBoolean","SPLIT",EDGE,{"disambiguationData":[TD([makeQuery(id+"F1.opExtrude","SWEPT_FACE",FACE,{"disambiguationData":[OSD([sQuery(id+"F0.wireOp",EDGE,"E3.sketch_text.stroke-119")])]})])],"derivedFrom":makeQuery(id+"F5.opExtrude","CAP_EDGE",EDGE,{"disambiguationData":[OSD([subQ0])],"isStart":true})});}
            var Q52;
            Q52=makeQuery(id+"F5.opExtrude","CAP_EDGE",EDGE,{"disambiguationData":[OSD([sQuery(id+"F4.wireOp",EDGE,"E13.0.1")])],"isStart":true});
            var Q53;
            {var subQ0=sQuery(id+"F4.wireOp",EDGE,"E13.0.2");Q53=makeQuery(id+"F10.opBoolean","SPLIT",EDGE,{"disambiguationData":[TD([makeQuery(id+"F1.opExtrude","SWEPT_FACE",FACE,{"disambiguationData":[OSD([sQuery(id+"F0.wireOp",EDGE,"E3.sketch_text.stroke-177")])]})])],"derivedFrom":makeQuery(id+"F5.opExtrude","CAP_EDGE",EDGE,{"disambiguationData":[OSD([subQ0])],"isStart":true})});}
            var Q54;
            {var subQ0=sQuery(id+"F4.wireOp",EDGE,"E13.0.2");Q54=makeQuery(id+"F10.opBoolean","SPLIT",EDGE,{"disambiguationData":[TD([makeQuery(id+"F1.opExtrude","SWEPT_FACE",FACE,{"disambiguationData":[OSD([sQuery(id+"F0.wireOp",EDGE,"E3.sketch_text.stroke-107")])]})])],"derivedFrom":makeQuery(id+"F5.opExtrude","CAP_EDGE",EDGE,{"disambiguationData":[OSD([subQ0])],"isStart":true})});}
            var Q55;
            Q55=makeQuery(id+"F5.opExtrude","CAP_EDGE",EDGE,{"disambiguationData":[OSD([sQuery(id+"F4.wireOp",EDGE,"E10.0.1")])],"isStart":true});
            var Q56;
            {var subQ0=sQuery(id+"F4.wireOp",EDGE,"E14.0.0");Q56=makeQuery(id+"F11.opBoolean","SPLIT",EDGE,{"disambiguationData":[TD([makeQuery(id+"F1.opExtrude","SWEPT_FACE",FACE,{"disambiguationData":[OSD([sQuery(id+"F0.wireOp",EDGE,"E4.sketch_text.stroke-3")])]})])],"derivedFrom":makeQuery(id+"F5.opExtrude","CAP_EDGE",EDGE,{"disambiguationData":[OSD([subQ0])],"isStart":true})});}
            var Q57;
            {var subQ0=sQuery(id+"F4.wireOp",EDGE,"E14.0.0");Q57=makeQuery(id+"F11.opBoolean","SPLIT",EDGE,{"disambiguationData":[TD([makeQuery(id+"F1.opExtrude","SWEPT_FACE",FACE,{"disambiguationData":[OSD([sQuery(id+"F0.wireOp",EDGE,"E4.sketch_text.stroke-30")])]})])],"derivedFrom":makeQuery(id+"F5.opExtrude","CAP_EDGE",EDGE,{"disambiguationData":[OSD([subQ0])],"isStart":true})});}
            var Q58;
            {var subQ0=sQuery(id+"F4.wireOp",EDGE,"E14.0.2");Q58=makeQuery(id+"F11.opBoolean","SPLIT",EDGE,{"disambiguationData":[TD([makeQuery(id+"F1.opExtrude","SWEPT_FACE",FACE,{"disambiguationData":[OSD([sQuery(id+"F0.wireOp",EDGE,"E4.sketch_text.stroke-75")])]})])],"derivedFrom":makeQuery(id+"F5.opExtrude","CAP_EDGE",EDGE,{"disambiguationData":[OSD([subQ0])],"isStart":true})});}
            var Q59;
            {var subQ0=sQuery(id+"F4.wireOp",EDGE,"E14.0.2");Q59=makeQuery(id+"F11.opBoolean","SPLIT",EDGE,{"disambiguationData":[TD([makeQuery(id+"F1.opExtrude","SWEPT_FACE",FACE,{"disambiguationData":[OSD([sQuery(id+"F0.wireOp",EDGE,"E4.sketch_text.stroke-58")])]})])],"derivedFrom":makeQuery(id+"F5.opExtrude","CAP_EDGE",EDGE,{"disambiguationData":[OSD([subQ0])],"isStart":true})});}
            var Q60;
            {var subQ0=sQuery(id+"F4.wireOp",EDGE,"E14.0.2");Q60=makeQuery(id+"F11.opBoolean","SPLIT",EDGE,{"disambiguationData":[TD([makeQuery(id+"F1.opExtrude","SWEPT_FACE",FACE,{"disambiguationData":[OSD([sQuery(id+"F0.wireOp",EDGE,"E4.sketch_text.stroke-30")])]})])],"derivedFrom":makeQuery(id+"F5.opExtrude","CAP_EDGE",EDGE,{"disambiguationData":[OSD([subQ0])],"isStart":true})});}
            var Q61;
            {var subQ0=sQuery(id+"F4.wireOp",EDGE,"E14.0.2");Q61=makeQuery(id+"F11.opBoolean","SPLIT",EDGE,{"disambiguationData":[TD([makeQuery(id+"F1.opExtrude","SWEPT_FACE",FACE,{"disambiguationData":[OSD([sQuery(id+"F0.wireOp",EDGE,"E4.sketch_text.stroke-110")])]})])],"derivedFrom":makeQuery(id+"F5.opExtrude","CAP_EDGE",EDGE,{"disambiguationData":[OSD([subQ0])],"isStart":true})});}
            var Q62;
            {var subQ0=sQuery(id+"F4.wireOp",EDGE,"E14.0.2");Q62=makeQuery(id+"F11.opBoolean","SPLIT",EDGE,{"disambiguationData":[TD([makeQuery(id+"F1.opExtrude","SWEPT_FACE",FACE,{"disambiguationData":[OSD([sQuery(id+"F0.wireOp",EDGE,"E4.sketch_text.stroke-123")])]})])],"derivedFrom":makeQuery(id+"F5.opExtrude","CAP_EDGE",EDGE,{"disambiguationData":[OSD([subQ0])],"isStart":true})});}
            var Q63;
            {var subQ0=sQuery(id+"F4.wireOp",EDGE,"E14.0.2");Q63=makeQuery(id+"F11.opBoolean","SPLIT",EDGE,{"disambiguationData":[TD([makeQuery(id+"F1.opExtrude","SWEPT_FACE",FACE,{"disambiguationData":[OSD([sQuery(id+"F0.wireOp",EDGE,"E4.sketch_text.stroke-164")])]})])],"derivedFrom":makeQuery(id+"F5.opExtrude","CAP_EDGE",EDGE,{"disambiguationData":[OSD([subQ0])],"isStart":true})});}
            var Q64;
            {var subQ0=sQuery(id+"F4.wireOp",EDGE,"E14.0.2");Q64=makeQuery(id+"F11.opBoolean","SPLIT",EDGE,{"disambiguationData":[TD([makeQuery(id+"F1.opExtrude","SWEPT_FACE",FACE,{"disambiguationData":[OSD([sQuery(id+"F0.wireOp",EDGE,"E4.sketch_text.stroke-8")])]})])],"derivedFrom":makeQuery(id+"F5.opExtrude","CAP_EDGE",EDGE,{"disambiguationData":[OSD([subQ0])],"isStart":true})});}
            var Q65;
            Q65=makeQuery(id+"F5.opExtrude","CAP_EDGE",EDGE,{"disambiguationData":[OSD([sQuery(id+"F4.wireOp",EDGE,"E14.0.3")])],"isStart":true});
            var Q66;
            {var subQ0=sQuery(id+"F4.wireOp",EDGE,"E14.0.0");Q66=makeQuery(id+"F11.opBoolean","SPLIT",EDGE,{"disambiguationData":[TD([makeQuery(id+"F1.opExtrude","SWEPT_FACE",FACE,{"disambiguationData":[OSD([sQuery(id+"F0.wireOp",EDGE,"E4.sketch_text.stroke-2")])]})])],"derivedFrom":makeQuery(id+"F5.opExtrude","CAP_EDGE",EDGE,{"disambiguationData":[OSD([subQ0])],"isStart":true})});}
            fillet(context, id + "F14", {"entities" : qUnion([Q0, Q1, Q2, Q3, Q4, Q5, Q6, Q7, Q8, Q9, Q10, Q11, Q12, Q13, Q14, Q15, Q16, Q17, Q18, Q19, Q20, Q21, Q22, Q23, Q24, Q25, Q26, Q27, Q28, Q29, Q30, Q31, Q32, Q33, Q34, Q35, Q36, Q37, Q38, Q39, Q40, Q41, Q42, Q43, Q44, Q45, Q46, Q47, Q48, Q49, Q50, Q51, Q52, Q53, Q54, Q55, Q56, Q57, Q58, Q59, Q60, Q61, Q62, Q63, Q64, Q65, Q66]), "radius" : 2 * mm, "tangentPropagation" : true, "allowEdgeOverflow" : false});
        }
        {
            var Q0;
            {var subQ0=sQuery(id+"F4.wireOp",EDGE,"E14.0.0");var subQ1=sQuery(id+"F4.wireOp",EDGE,"E14.0.1");Q0=makeQuery(id+"F6.opFillet","BLEND_EDGE",EDGE,{"blendedFrom":[makeQuery(id+"F5.opExtrude","SWEPT_EDGE",EDGE,{"disambiguationData":[OSD([subQ0,subQ1])]}),makeQuery(id+"F5.opExtrude","CAP_FACE",FACE,{"disambiguationData":[OSD([subQ0,subQ1,sQuery(id+"F4.wireOp",EDGE,"E14.0.2"),sQuery(id+"F4.wireOp",EDGE,"E14.0.3")])],"isStart":true})],"blendedInto":[makeQuery(id+"F5.opExtrude","CAP_FACE",FACE,{"disambiguationData":[OSD([subQ0,subQ1,sQuery(id+"F4.wireOp",EDGE,"E14.0.2"),sQuery(id+"F4.wireOp",EDGE,"E14.0.3")])],"isStart":true})]});}
            var Q1;
            {var subQ0=sQuery(id+"F4.wireOp",EDGE,"E14.0.2");Q1=makeQuery(id+"F11.opBoolean","SPLIT",EDGE,{"disambiguationData":[TD([makeQuery(id+"F1.opExtrude","SWEPT_FACE",FACE,{"disambiguationData":[OSD([sQuery(id+"F0.wireOp",EDGE,"E4.sketch_text.stroke-160")])]})])],"derivedFrom":makeQuery(id+"F5.opExtrude","CAP_EDGE",EDGE,{"disambiguationData":[OSD([subQ0])],"isStart":true})});}
            var Q2;
            {var subQ0=sQuery(id+"F4.wireOp",EDGE,"E14.0.2");Q2=makeQuery(id+"F11.opBoolean","SPLIT",EDGE,{"disambiguationData":[TD([makeQuery(id+"F1.opExtrude","SWEPT_FACE",FACE,{"disambiguationData":[OSD([sQuery(id+"F0.wireOp",EDGE,"E4.sketch_text.stroke-54")])]})])],"derivedFrom":makeQuery(id+"F5.opExtrude","CAP_EDGE",EDGE,{"disambiguationData":[OSD([subQ0])],"isStart":true})});}
            var Q3;
            {var subQ0=sQuery(id+"F4.wireOp",EDGE,"E13.0.2");Q3=makeQuery(id+"F10.opBoolean","SPLIT",EDGE,{"disambiguationData":[TD([makeQuery(id+"F1.opExtrude","SWEPT_FACE",FACE,{"disambiguationData":[OSD([sQuery(id+"F0.wireOp",EDGE,"E3.sketch_text.stroke-30")])]})])],"derivedFrom":makeQuery(id+"F5.opExtrude","CAP_EDGE",EDGE,{"disambiguationData":[OSD([subQ0])],"isStart":true})});}
            var Q4;
            {var subQ0=sQuery(id+"F4.wireOp",EDGE,"E11.0.2");Q4=makeQuery(id+"F8.opBoolean","SPLIT",EDGE,{"disambiguationData":[TD([makeQuery(id+"F1.opExtrude","SWEPT_FACE",FACE,{"disambiguationData":[OSD([sQuery(id+"F0.wireOp",EDGE,"E1.sketch_text.stroke-30")])]})])],"derivedFrom":makeQuery(id+"F5.opExtrude","CAP_EDGE",EDGE,{"disambiguationData":[OSD([subQ0])],"isStart":true})});}
            var Q5;
            {var subQ0=sQuery(id+"F4.wireOp",EDGE,"E11.0.2");Q5=makeQuery(id+"F8.opBoolean","SPLIT",EDGE,{"disambiguationData":[TD([makeQuery(id+"F1.opExtrude","SWEPT_FACE",FACE,{"disambiguationData":[OSD([sQuery(id+"F0.wireOp",EDGE,"E1.sketch_text.stroke-131")])]})])],"derivedFrom":makeQuery(id+"F5.opExtrude","CAP_EDGE",EDGE,{"disambiguationData":[OSD([subQ0])],"isStart":true})});}
            var Q6;
            {var subQ0=sQuery(id+"F4.wireOp",EDGE,"E11.0.2");Q6=makeQuery(id+"F8.opBoolean","SPLIT",EDGE,{"disambiguationData":[TD([makeQuery(id+"F1.opExtrude","SWEPT_FACE",FACE,{"disambiguationData":[OSD([sQuery(id+"F0.wireOp",EDGE,"E1.sketch_text.stroke-156")])]})])],"derivedFrom":makeQuery(id+"F5.opExtrude","CAP_EDGE",EDGE,{"disambiguationData":[OSD([subQ0])],"isStart":true})});}
            fillet(context, id + "F15", {"entities" : qUnion([Q0, Q1, Q2, Q3, Q4, Q5, Q6]), "radius" : 1.9 * mm, "tangentPropagation" : true, "allowEdgeOverflow" : false});
        }
        {
            var Q0;
            Q0=makeQuery(id+"F5.opExtrude","CAP_FACE",FACE,{"disambiguationData":[OSD([sQuery(id+"F4.wireOp",EDGE,"E12.0.0"),sQuery(id+"F4.wireOp",EDGE,"E12.0.1"),sQuery(id+"F4.wireOp",EDGE,"E12.0.2"),sQuery(id+"F4.wireOp",EDGE,"E12.0.3")])],"isStart":false});
            var sketch = newSketch(context, id + "F16", { "sketchPlane" : qUnion([Q0])});
            skLineSegment(sketch, "E15.0.0", {"start": v(-61.56, -63.64) * mm, "end": v(2.44, -63.64) * mm});
            skArc(sketch, "E15.0.1", {"start": v(2.44, -63.64) * mm, "mid": v(5.27, -62.47) * mm, "end": v(6.44, -59.64) * mm});
            skLineSegment(sketch, "E15.0.2", {"start": v(6.44, -59.64) * mm, "end": v(6.44, -54.64) * mm});
            skArc(sketch, "E15.0.3", {"start": v(6.44, -54.64) * mm, "mid": v(5.27, -51.81) * mm, "end": v(2.44, -50.64) * mm});
            skLineSegment(sketch, "E15.0.4", {"start": v(2.44, -50.64) * mm, "end": v(-61.56, -50.64) * mm});
            skArc(sketch, "E15.0.5", {"start": v(-61.56, -50.64) * mm, "mid": v(-64.39, -51.81) * mm, "end": v(-65.56, -54.64) * mm});
            skLineSegment(sketch, "E15.0.6", {"start": v(-65.56, -54.64) * mm, "end": v(-65.56, -59.64) * mm});
            skArc(sketch, "E15.0.7", {"start": v(-65.56, -59.64) * mm, "mid": v(-64.39, -62.47) * mm, "end": v(-61.56, -63.64) * mm});
            skLineSegment(sketch, "E16.0.0", {"start": v(-20.95, -39.07) * mm, "end": v(43.73, -39.07) * mm});
            skArc(sketch, "E16.0.1", {"start": v(43.73, -39.07) * mm, "mid": v(46.55, -37.9) * mm, "end": v(47.73, -35.07) * mm});
            skLineSegment(sketch, "E16.0.2", {"start": v(47.73, -35.07) * mm, "end": v(47.73, -30.07) * mm});
            skArc(sketch, "E16.0.3", {"start": v(47.73, -30.07) * mm, "mid": v(46.55, -27.25) * mm, "end": v(43.73, -26.07) * mm});
            skLineSegment(sketch, "E16.0.4", {"start": v(43.73, -26.07) * mm, "end": v(-20.95, -26.07) * mm});
            skArc(sketch, "E16.0.5", {"start": v(-20.95, -26.07) * mm, "mid": v(-23.78, -27.25) * mm, "end": v(-24.95, -30.07) * mm});
            skLineSegment(sketch, "E16.0.6", {"start": v(-24.95, -30.07) * mm, "end": v(-24.95, -35.07) * mm});
            skArc(sketch, "E16.0.7", {"start": v(-24.95, -35.07) * mm, "mid": v(-23.78, -37.9) * mm, "end": v(-20.95, -39.07) * mm});
            skLineSegment(sketch, "E17.0.0", {"start": v(-64.8, -14.71) * mm, "end": v(42.87, -14.71) * mm});
            skArc(sketch, "E17.0.1", {"start": v(42.87, -14.71) * mm, "mid": v(45.7, -13.54) * mm, "end": v(46.87, -10.71) * mm});
            skLineSegment(sketch, "E17.0.2", {"start": v(46.87, -10.71) * mm, "end": v(46.87, -5.71) * mm});
            skArc(sketch, "E17.0.3", {"start": v(46.87, -5.71) * mm, "mid": v(45.7, -2.88) * mm, "end": v(42.87, -1.71) * mm});
            skLineSegment(sketch, "E17.0.4", {"start": v(42.87, -1.71) * mm, "end": v(-64.8, -1.71) * mm});
            skArc(sketch, "E17.0.5", {"start": v(-64.8, -1.71) * mm, "mid": v(-67.63, -2.88) * mm, "end": v(-68.8, -5.71) * mm});
            skLineSegment(sketch, "E17.0.6", {"start": v(-68.8, -5.71) * mm, "end": v(-68.8, -10.71) * mm});
            skArc(sketch, "E17.0.7", {"start": v(-68.8, -10.71) * mm, "mid": v(-67.63, -13.54) * mm, "end": v(-64.8, -14.71) * mm});
            skLineSegment(sketch, "E18.0.0", {"start": v(-61.39, 15.52) * mm, "end": v(6.87, 15.52) * mm});
            skArc(sketch, "E18.0.1", {"start": v(6.87, 15.52) * mm, "mid": v(9.7, 16.7) * mm, "end": v(10.87, 19.52) * mm});
            skLineSegment(sketch, "E18.0.2", {"start": v(10.87, 19.52) * mm, "end": v(10.87, 24.52) * mm});
            skArc(sketch, "E18.0.3", {"start": v(10.87, 24.52) * mm, "mid": v(9.7, 27.35) * mm, "end": v(6.87, 28.52) * mm});
            skLineSegment(sketch, "E18.0.4", {"start": v(6.87, 28.52) * mm, "end": v(-61.39, 28.52) * mm});
            skArc(sketch, "E18.0.5", {"start": v(-61.39, 28.52) * mm, "mid": v(-64.22, 27.35) * mm, "end": v(-65.39, 24.52) * mm});
            skLineSegment(sketch, "E18.0.6", {"start": v(-65.39, 24.52) * mm, "end": v(-65.39, 19.52) * mm});
            skArc(sketch, "E18.0.7", {"start": v(-65.39, 19.52) * mm, "mid": v(-64.22, 16.7) * mm, "end": v(-61.39, 15.52) * mm});
            skLineSegment(sketch, "E19.0.0", {"start": v(-60.88, 45) * mm, "end": v(5.85, 45) * mm});
            skArc(sketch, "E19.0.1", {"start": v(5.85, 45) * mm, "mid": v(8.68, 46.17) * mm, "end": v(9.85, 49) * mm});
            skLineSegment(sketch, "E19.0.2", {"start": v(9.85, 49) * mm, "end": v(9.85, 54) * mm});
            skArc(sketch, "E19.0.3", {"start": v(9.85, 54) * mm, "mid": v(8.68, 56.83) * mm, "end": v(5.85, 58) * mm});
            skLineSegment(sketch, "E19.0.4", {"start": v(5.85, 58) * mm, "end": v(-60.88, 58) * mm});
            skArc(sketch, "E19.0.5", {"start": v(-60.88, 58) * mm, "mid": v(-63.7, 56.83) * mm, "end": v(-64.88, 54) * mm});
            skLineSegment(sketch, "E19.0.6", {"start": v(-64.88, 54) * mm, "end": v(-64.88, 49) * mm});
            skArc(sketch, "E19.0.7", {"start": v(-64.88, 49) * mm, "mid": v(-63.7, 46.17) * mm, "end": v(-60.88, 45) * mm});
            skLineSegment(sketch, "E20.bottom", {"start": v(2.44, -59.64) * mm, "end": v(-3.06, -59.64) * mm});
            skLineSegment(sketch, "E20.top", {"start": v(2.44, -54.14) * mm, "end": v(-3.06, -54.14) * mm});
            skLineSegment(sketch, "E20.left", {"start": v(2.44, -59.64) * mm, "end": v(2.44, -54.14) * mm});
            skLineSegment(sketch, "E20.right", {"start": v(-3.06, -59.64) * mm, "end": v(-3.06, -54.14) * mm});
            skLineSegment(sketch, "E21.bottom", {"start": v(-61.56, -59.64) * mm, "end": v(-56.06, -59.64) * mm});
            skLineSegment(sketch, "E21.top", {"start": v(-61.56, -54.14) * mm, "end": v(-56.06, -54.14) * mm});
            skLineSegment(sketch, "E21.left", {"start": v(-61.56, -59.64) * mm, "end": v(-61.56, -54.14) * mm});
            skLineSegment(sketch, "E21.right", {"start": v(-56.06, -59.64) * mm, "end": v(-56.06, -54.14) * mm});
            skLineSegment(sketch, "E22.bottom", {"start": v(-20.95, -35.07) * mm, "end": v(-15.45, -35.07) * mm});
            skLineSegment(sketch, "E22.top", {"start": v(-20.95, -29.57) * mm, "end": v(-15.45, -29.57) * mm});
            skLineSegment(sketch, "E22.left", {"start": v(-20.95, -35.07) * mm, "end": v(-20.95, -29.57) * mm});
            skLineSegment(sketch, "E22.right", {"start": v(-15.45, -35.07) * mm, "end": v(-15.45, -29.57) * mm});
            skLineSegment(sketch, "E23.bottom", {"start": v(43.73, -35.07) * mm, "end": v(38.23, -35.07) * mm});
            skLineSegment(sketch, "E23.top", {"start": v(43.73, -29.57) * mm, "end": v(38.23, -29.57) * mm});
            skLineSegment(sketch, "E23.left", {"start": v(43.73, -35.07) * mm, "end": v(43.73, -29.57) * mm});
            skLineSegment(sketch, "E23.right", {"start": v(38.23, -35.07) * mm, "end": v(38.23, -29.57) * mm});
            skLineSegment(sketch, "E24.bottom", {"start": v(42.87, -10.71) * mm, "end": v(37.37, -10.71) * mm});
            skLineSegment(sketch, "E24.top", {"start": v(42.87, -5.21) * mm, "end": v(37.37, -5.21) * mm});
            skLineSegment(sketch, "E24.left", {"start": v(42.87, -10.71) * mm, "end": v(42.87, -5.21) * mm});
            skLineSegment(sketch, "E24.right", {"start": v(37.37, -10.71) * mm, "end": v(37.37, -5.21) * mm});
            skLineSegment(sketch, "E25.bottom", {"start": v(-64.8, -10.71) * mm, "end": v(-59.3, -10.71) * mm});
            skLineSegment(sketch, "E25.top", {"start": v(-64.8, -5.21) * mm, "end": v(-59.3, -5.21) * mm});
            skLineSegment(sketch, "E25.left", {"start": v(-64.8, -10.71) * mm, "end": v(-64.8, -5.21) * mm});
            skLineSegment(sketch, "E25.right", {"start": v(-59.3, -10.71) * mm, "end": v(-59.3, -5.21) * mm});
            skLineSegment(sketch, "E26.bottom", {"start": v(6.87, 19.52) * mm, "end": v(1.37, 19.52) * mm});
            skLineSegment(sketch, "E26.top", {"start": v(6.87, 25.02) * mm, "end": v(1.37, 25.02) * mm});
            skLineSegment(sketch, "E26.left", {"start": v(6.87, 19.52) * mm, "end": v(6.87, 25.02) * mm});
            skLineSegment(sketch, "E26.right", {"start": v(1.37, 19.52) * mm, "end": v(1.37, 25.02) * mm});
            skLineSegment(sketch, "E27.bottom", {"start": v(5.85, 49) * mm, "end": v(0.35, 49) * mm});
            skLineSegment(sketch, "E27.top", {"start": v(5.85, 54.5) * mm, "end": v(0.35, 54.5) * mm});
            skLineSegment(sketch, "E27.left", {"start": v(5.85, 49) * mm, "end": v(5.85, 54.5) * mm});
            skLineSegment(sketch, "E27.right", {"start": v(0.35, 49) * mm, "end": v(0.35, 54.5) * mm});
            skLineSegment(sketch, "E28.bottom", {"start": v(-61.39, 19.52) * mm, "end": v(-55.89, 19.52) * mm});
            skLineSegment(sketch, "E28.top", {"start": v(-61.39, 25.02) * mm, "end": v(-55.89, 25.02) * mm});
            skLineSegment(sketch, "E28.left", {"start": v(-61.39, 19.52) * mm, "end": v(-61.39, 25.02) * mm});
            skLineSegment(sketch, "E28.right", {"start": v(-55.89, 19.52) * mm, "end": v(-55.89, 25.02) * mm});
            skLineSegment(sketch, "E29.bottom", {"start": v(-60.88, 49) * mm, "end": v(-55.38, 49) * mm});
            skLineSegment(sketch, "E29.top", {"start": v(-60.88, 54.5) * mm, "end": v(-55.38, 54.5) * mm});
            skLineSegment(sketch, "E29.left", {"start": v(-60.88, 49) * mm, "end": v(-60.88, 54.5) * mm});
            skLineSegment(sketch, "E29.right", {"start": v(-55.38, 49) * mm, "end": v(-55.38, 54.5) * mm});
            skSolve(sketch);
        }
        {
            var Q0;
            Q0=makeQuery(id+"F16.imprint","IMPRINT",FACE,{"disambiguationData":[TD([[makeQuery(id+"F16.imprint","IMPRINT",EDGE,{"derivedFrom":sQuery(id+"F16.wireOp",EDGE,"E20.bottom")}),-1.0]])]});
            var Q1;
            Q1=makeQuery(id+"F16.imprint","IMPRINT",FACE,{"disambiguationData":[TD([[makeQuery(id+"F16.imprint","IMPRINT",EDGE,{"derivedFrom":sQuery(id+"F16.wireOp",EDGE,"E21.bottom")}),1.0]])]});
            var Q2;
            Q2=makeQuery(id+"F16.imprint","IMPRINT",FACE,{"disambiguationData":[TD([[makeQuery(id+"F16.imprint","IMPRINT",EDGE,{"derivedFrom":sQuery(id+"F16.wireOp",EDGE,"E22.bottom")}),1.0]])]});
            var Q3;
            Q3=makeQuery(id+"F16.imprint","IMPRINT",FACE,{"disambiguationData":[TD([[makeQuery(id+"F16.imprint","IMPRINT",EDGE,{"derivedFrom":sQuery(id+"F16.wireOp",EDGE,"E23.bottom")}),-1.0]])]});
            var Q4;
            Q4=makeQuery(id+"F16.imprint","IMPRINT",FACE,{"disambiguationData":[TD([[makeQuery(id+"F16.imprint","IMPRINT",EDGE,{"derivedFrom":sQuery(id+"F16.wireOp",EDGE,"E24.bottom")}),-1.0]])]});
            var Q5;
            Q5=makeQuery(id+"F16.imprint","IMPRINT",FACE,{"disambiguationData":[TD([[makeQuery(id+"F16.imprint","IMPRINT",EDGE,{"derivedFrom":sQuery(id+"F16.wireOp",EDGE,"E25.bottom")}),1.0]])]});
            var Q6;
            Q6=makeQuery(id+"F16.imprint","IMPRINT",FACE,{"disambiguationData":[TD([[makeQuery(id+"F16.imprint","IMPRINT",EDGE,{"derivedFrom":sQuery(id+"F16.wireOp",EDGE,"E28.bottom")}),1.0]])]});
            var Q7;
            Q7=makeQuery(id+"F16.imprint","IMPRINT",FACE,{"disambiguationData":[TD([[makeQuery(id+"F16.imprint","IMPRINT",EDGE,{"derivedFrom":sQuery(id+"F16.wireOp",EDGE,"E26.bottom")}),-1.0]])]});
            var Q8;
            Q8=makeQuery(id+"F16.imprint","IMPRINT",FACE,{"disambiguationData":[TD([[makeQuery(id+"F16.imprint","IMPRINT",EDGE,{"derivedFrom":sQuery(id+"F16.wireOp",EDGE,"E27.bottom")}),-1.0]])]});
            var Q9;
            Q9=makeQuery(id+"F16.imprint","IMPRINT",FACE,{"disambiguationData":[TD([[makeQuery(id+"F16.imprint","IMPRINT",EDGE,{"derivedFrom":sQuery(id+"F16.wireOp",EDGE,"E29.bottom")}),1.0]])]});
            extrude(context, id + "F17", {"entities" : qUnion([Q0, Q1, Q2, Q3, Q4, Q5, Q6, Q7, Q8, Q9]), "operationType" : NewBodyOperationType.REMOVE, "oppositeDirection" : true, "depth" : 4 * mm});
        }
    });
